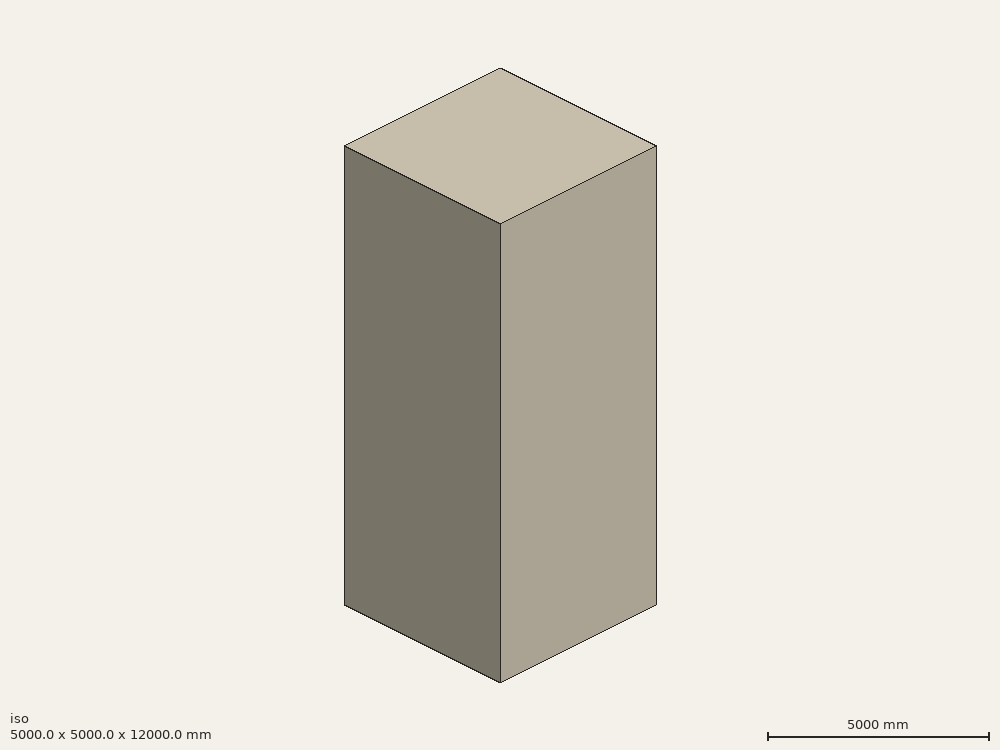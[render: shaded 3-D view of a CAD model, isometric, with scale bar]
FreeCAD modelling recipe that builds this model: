
FCSTD DOCUMENT  (FreeCAD 0.21R33694 (Git))
Label: revolveTester-7_scaled
License: All rights reserved
LicenseURL: http://en.wikipedia.org/wiki/All_rights_reserved
objects: App::DocumentObjectGroupPython×1248, Part::FeaturePython×2, App::Part×2, Sketcher::SketchObject×1, Part::Revolution×1, Part::Cylinder×1, Part::Cut×1
note: 6 computed .brp shape members not serialized (recipe doc carries the construction recipe); baked Part::Feature solids carry a one-line shape summary decoded from their .brp

FEATURE [App::DocumentObjectGroupPython] HALFPI  # scripted group (container) (typed FeaturePython)
  name = HALFPI
  value = pi/2.
FEATURE [App::DocumentObjectGroupPython] PI  # scripted group (container) (typed FeaturePython)
  name = PI
  value = 1.*pi
FEATURE [App::DocumentObjectGroupPython] TWOPI  # scripted group (container) (typed FeaturePython)
  name = TWOPI
  value = 2.*pi
FEATURE [App::DocumentObjectGroupPython] Constants  # scripted group (container) (typed FeaturePython)
  Group = -> [HALFPI,PI,TWOPI]
FEATURE [App::DocumentObjectGroupPython] Variables  # scripted group (container) (typed FeaturePython)
FEATURE [App::DocumentObjectGroupPython] Quantities  # scripted group (container) (typed FeaturePython)
FEATURE [App::DocumentObjectGroupPython] Isotopes  # scripted group (container) (typed FeaturePython)
FEATURE [App::DocumentObjectGroupPython] Elements  # scripted group (container) (typed FeaturePython)
FEATURE [App::DocumentObjectGroupPython] G4Isotopes  # scripted group (container) (typed FeaturePython)
FEATURE [App::DocumentObjectGroupPython] H_element  # scripted group (container) (typed FeaturePython)
  Z = 1
  atom_value = 1.008
  formula = H
  name = H_element
FEATURE [App::DocumentObjectGroupPython] He_element  # scripted group (container) (typed FeaturePython)
  Z = 2
  atom_value = 4.0026
  formula = He
  name = He_element
FEATURE [App::DocumentObjectGroupPython] Li_element  # scripted group (container) (typed FeaturePython)
  Z = 3
  atom_value = 6.94
  formula = Li
  name = Li_element
FEATURE [App::DocumentObjectGroupPython] Be_element  # scripted group (container) (typed FeaturePython)
  Z = 4
  atom_value = 9.01218
  formula = Be
  name = Be_element
FEATURE [App::DocumentObjectGroupPython] B_element  # scripted group (container) (typed FeaturePython)
  Z = 5
  atom_value = 10.81
  formula = B
  name = B_element
FEATURE [App::DocumentObjectGroupPython] C_element  # scripted group (container) (typed FeaturePython)
  Z = 6
  atom_value = 12.011
  formula = C
  name = C_element
FEATURE [App::DocumentObjectGroupPython] N_element  # scripted group (container) (typed FeaturePython)
  Z = 7
  atom_value = 14.007
  formula = N
  name = N_element
FEATURE [App::DocumentObjectGroupPython] O_element  # scripted group (container) (typed FeaturePython)
  Z = 8
  atom_value = 15.999
  formula = O
  name = O_element
FEATURE [App::DocumentObjectGroupPython] F_element  # scripted group (container) (typed FeaturePython)
  Z = 9
  atom_value = 18.9984
  formula = F
  name = F_element
FEATURE [App::DocumentObjectGroupPython] Ne_element  # scripted group (container) (typed FeaturePython)
  Z = 10
  atom_value = 20.1797
  formula = Ne
  name = Ne_element
FEATURE [App::DocumentObjectGroupPython] Na_element  # scripted group (container) (typed FeaturePython)
  Z = 11
  atom_value = 22.9898
  formula = Na
  name = Na_element
FEATURE [App::DocumentObjectGroupPython] Mg_element  # scripted group (container) (typed FeaturePython)
  Z = 12
  atom_value = 24.305
  formula = Mg
  name = Mg_element
FEATURE [App::DocumentObjectGroupPython] Al_element  # scripted group (container) (typed FeaturePython)
  Z = 13
  atom_value = 26.9815
  formula = Al
  name = Al_element
FEATURE [App::DocumentObjectGroupPython] Si_element  # scripted group (container) (typed FeaturePython)
  Z = 14
  atom_value = 28.085
  formula = Si
  name = Si_element
FEATURE [App::DocumentObjectGroupPython] P_element  # scripted group (container) (typed FeaturePython)
  Z = 15
  atom_value = 30.9738
  formula = P
  name = P_element
FEATURE [App::DocumentObjectGroupPython] S_element  # scripted group (container) (typed FeaturePython)
  Z = 16
  atom_value = 32.06
  formula = S
  name = S_element
FEATURE [App::DocumentObjectGroupPython] Cl_element  # scripted group (container) (typed FeaturePython)
  Z = 17
  atom_value = 35.45
  formula = Cl
  name = Cl_element
FEATURE [App::DocumentObjectGroupPython] Ar_element  # scripted group (container) (typed FeaturePython)
  Z = 18
  atom_value = 39.95
  formula = Ar
  name = Ar_element
FEATURE [App::DocumentObjectGroupPython] K_element  # scripted group (container) (typed FeaturePython)
  Z = 19
  atom_value = 39.0983
  formula = K
  name = K_element
FEATURE [App::DocumentObjectGroupPython] Ca_element  # scripted group (container) (typed FeaturePython)
  Z = 20
  atom_value = 40.078
  formula = Ca
  name = Ca_element
FEATURE [App::DocumentObjectGroupPython] Sc_element  # scripted group (container) (typed FeaturePython)
  Z = 21
  atom_value = 44.9559
  formula = Sc
  name = Sc_element
FEATURE [App::DocumentObjectGroupPython] Ti_element  # scripted group (container) (typed FeaturePython)
  Z = 22
  atom_value = 47.867
  formula = Ti
  name = Ti_element
FEATURE [App::DocumentObjectGroupPython] V_element  # scripted group (container) (typed FeaturePython)
  Z = 23
  atom_value = 50.9415
  formula = V
  name = V_element
FEATURE [App::DocumentObjectGroupPython] Cr_element  # scripted group (container) (typed FeaturePython)
  Z = 24
  atom_value = 51.9961
  formula = Cr
  name = Cr_element
FEATURE [App::DocumentObjectGroupPython] Mn_element  # scripted group (container) (typed FeaturePython)
  Z = 25
  atom_value = 54.938
  formula = Mn
  name = Mn_element
FEATURE [App::DocumentObjectGroupPython] Fe_element  # scripted group (container) (typed FeaturePython)
  Z = 26
  atom_value = 55.845
  formula = Fe
  name = Fe_element
FEATURE [App::DocumentObjectGroupPython] Co_element  # scripted group (container) (typed FeaturePython)
  Z = 27
  atom_value = 58.9332
  formula = Co
  name = Co_element
FEATURE [App::DocumentObjectGroupPython] Ni_element  # scripted group (container) (typed FeaturePython)
  Z = 28
  atom_value = 58.6934
  formula = Ni
  name = Ni_element
FEATURE [App::DocumentObjectGroupPython] Cu_element  # scripted group (container) (typed FeaturePython)
  Z = 29
  atom_value = 63.546
  formula = Cu
  name = Cu_element
FEATURE [App::DocumentObjectGroupPython] Zn_element  # scripted group (container) (typed FeaturePython)
  Z = 30
  atom_value = 65.38
  formula = Zn
  name = Zn_element
FEATURE [App::DocumentObjectGroupPython] Ga_element  # scripted group (container) (typed FeaturePython)
  Z = 31
  atom_value = 69.723
  formula = Ga
  name = Ga_element
FEATURE [App::DocumentObjectGroupPython] Ge_element  # scripted group (container) (typed FeaturePython)
  Z = 32
  atom_value = 72.63
  formula = Ge
  name = Ge_element
FEATURE [App::DocumentObjectGroupPython] As_element  # scripted group (container) (typed FeaturePython)
  Z = 33
  atom_value = 74.9216
  formula = As
  name = As_element
FEATURE [App::DocumentObjectGroupPython] Se_element  # scripted group (container) (typed FeaturePython)
  Z = 34
  atom_value = 78.971
  formula = Se
  name = Se_element
FEATURE [App::DocumentObjectGroupPython] Br_element  # scripted group (container) (typed FeaturePython)
  Z = 35
  atom_value = 79.904
  formula = Br
  name = Br_element
FEATURE [App::DocumentObjectGroupPython] Kr_element  # scripted group (container) (typed FeaturePython)
  Z = 36
  atom_value = 83.798
  formula = Kr
  name = Kr_element
FEATURE [App::DocumentObjectGroupPython] Rb_element  # scripted group (container) (typed FeaturePython)
  Z = 37
  atom_value = 85.4678
  formula = Rb
  name = Rb_element
FEATURE [App::DocumentObjectGroupPython] Sr_element  # scripted group (container) (typed FeaturePython)
  Z = 38
  atom_value = 87.62
  formula = Sr
  name = Sr_element
FEATURE [App::DocumentObjectGroupPython] Y_element  # scripted group (container) (typed FeaturePython)
  Z = 39
  atom_value = 88.9058
  formula = Y
  name = Y_element
FEATURE [App::DocumentObjectGroupPython] Zr_element  # scripted group (container) (typed FeaturePython)
  Z = 40
  atom_value = 91.224
  formula = Zr
  name = Zr_element
FEATURE [App::DocumentObjectGroupPython] Nb_element  # scripted group (container) (typed FeaturePython)
  Z = 41
  atom_value = 92.9064
  formula = Nb
  name = Nb_element
FEATURE [App::DocumentObjectGroupPython] Mo_element  # scripted group (container) (typed FeaturePython)
  Z = 42
  atom_value = 95.95
  formula = Mo
  name = Mo_element
FEATURE [App::DocumentObjectGroupPython] Tc_element  # scripted group (container) (typed FeaturePython)
  Z = 43
  atom_value = 97
  formula = Tc
  name = Tc_element
FEATURE [App::DocumentObjectGroupPython] Ru_element  # scripted group (container) (typed FeaturePython)
  Z = 44
  atom_value = 101.07
  formula = Ru
  name = Ru_element
FEATURE [App::DocumentObjectGroupPython] Rh_element  # scripted group (container) (typed FeaturePython)
  Z = 45
  atom_value = 102.905
  formula = Rh
  name = Rh_element
FEATURE [App::DocumentObjectGroupPython] Pd_element  # scripted group (container) (typed FeaturePython)
  Z = 46
  atom_value = 106.42
  formula = Pd
  name = Pd_element
FEATURE [App::DocumentObjectGroupPython] Ag_element  # scripted group (container) (typed FeaturePython)
  Z = 47
  atom_value = 107.868
  formula = Ag
  name = Ag_element
FEATURE [App::DocumentObjectGroupPython] Cd_element  # scripted group (container) (typed FeaturePython)
  Z = 48
  atom_value = 112.414
  formula = Cd
  name = Cd_element
FEATURE [App::DocumentObjectGroupPython] In_element  # scripted group (container) (typed FeaturePython)
  Z = 49
  atom_value = 114.818
  formula = In
  name = In_element
FEATURE [App::DocumentObjectGroupPython] Sn_element  # scripted group (container) (typed FeaturePython)
  Z = 50
  atom_value = 118.71
  formula = Sn
  name = Sn_element
FEATURE [App::DocumentObjectGroupPython] Sb_element  # scripted group (container) (typed FeaturePython)
  Z = 51
  atom_value = 121.76
  formula = Sb
  name = Sb_element
FEATURE [App::DocumentObjectGroupPython] Te_element  # scripted group (container) (typed FeaturePython)
  Z = 52
  atom_value = 127.6
  formula = Te
  name = Te_element
FEATURE [App::DocumentObjectGroupPython] I_element  # scripted group (container) (typed FeaturePython)
  Z = 53
  atom_value = 126.904
  formula = I
  name = I_element
FEATURE [App::DocumentObjectGroupPython] Xe_element  # scripted group (container) (typed FeaturePython)
  Z = 54
  atom_value = 131.293
  formula = Xe
  name = Xe_element
FEATURE [App::DocumentObjectGroupPython] Cs_element  # scripted group (container) (typed FeaturePython)
  Z = 55
  atom_value = 132.905
  formula = Cs
  name = Cs_element
FEATURE [App::DocumentObjectGroupPython] Ba_element  # scripted group (container) (typed FeaturePython)
  Z = 56
  atom_value = 137.327
  formula = Ba
  name = Ba_element
FEATURE [App::DocumentObjectGroupPython] La_element  # scripted group (container) (typed FeaturePython)
  Z = 57
  atom_value = 138.905
  formula = La
  name = La_element
FEATURE [App::DocumentObjectGroupPython] Ce_element  # scripted group (container) (typed FeaturePython)
  Z = 58
  atom_value = 140.116
  formula = Ce
  name = Ce_element
FEATURE [App::DocumentObjectGroupPython] Pr_element  # scripted group (container) (typed FeaturePython)
  Z = 59
  atom_value = 140.908
  formula = Pr
  name = Pr_element
FEATURE [App::DocumentObjectGroupPython] Nd_element  # scripted group (container) (typed FeaturePython)
  Z = 60
  atom_value = 144.242
  formula = Nd
  name = Nd_element
FEATURE [App::DocumentObjectGroupPython] Pm_element  # scripted group (container) (typed FeaturePython)
  Z = 61
  atom_value = 145
  formula = Pm
  name = Pm_element
FEATURE [App::DocumentObjectGroupPython] Sm_element  # scripted group (container) (typed FeaturePython)
  Z = 62
  atom_value = 150.36
  formula = Sm
  name = Sm_element
FEATURE [App::DocumentObjectGroupPython] Eu_element  # scripted group (container) (typed FeaturePython)
  Z = 63
  atom_value = 151.964
  formula = Eu
  name = Eu_element
FEATURE [App::DocumentObjectGroupPython] Gd_element  # scripted group (container) (typed FeaturePython)
  Z = 64
  atom_value = 157.25
  formula = Gd
  name = Gd_element
FEATURE [App::DocumentObjectGroupPython] Tb_element  # scripted group (container) (typed FeaturePython)
  Z = 65
  atom_value = 158.925
  formula = Tb
  name = Tb_element
FEATURE [App::DocumentObjectGroupPython] Dy_element  # scripted group (container) (typed FeaturePython)
  Z = 66
  atom_value = 162.5
  formula = Dy
  name = Dy_element
FEATURE [App::DocumentObjectGroupPython] Ho_element  # scripted group (container) (typed FeaturePython)
  Z = 67
  atom_value = 164.93
  formula = Ho
  name = Ho_element
FEATURE [App::DocumentObjectGroupPython] Er_element  # scripted group (container) (typed FeaturePython)
  Z = 68
  atom_value = 167.259
  formula = Er
  name = Er_element
FEATURE [App::DocumentObjectGroupPython] Tm_element  # scripted group (container) (typed FeaturePython)
  Z = 69
  atom_value = 168.934
  formula = Tm
  name = Tm_element
FEATURE [App::DocumentObjectGroupPython] Yb_element  # scripted group (container) (typed FeaturePython)
  Z = 70
  atom_value = 173.045
  formula = Yb
  name = Yb_element
FEATURE [App::DocumentObjectGroupPython] Lu_element  # scripted group (container) (typed FeaturePython)
  Z = 71
  atom_value = 174.967
  formula = Lu
  name = Lu_element
FEATURE [App::DocumentObjectGroupPython] Hf_element  # scripted group (container) (typed FeaturePython)
  Z = 72
  atom_value = 178.49
  formula = Hf
  name = Hf_element
FEATURE [App::DocumentObjectGroupPython] Ta_element  # scripted group (container) (typed FeaturePython)
  Z = 73
  atom_value = 180.948
  formula = Ta
  name = Ta_element
FEATURE [App::DocumentObjectGroupPython] W_element  # scripted group (container) (typed FeaturePython)
  Z = 74
  atom_value = 183.84
  formula = W
  name = W_element
FEATURE [App::DocumentObjectGroupPython] Re_element  # scripted group (container) (typed FeaturePython)
  Z = 75
  atom_value = 186.207
  formula = Re
  name = Re_element
FEATURE [App::DocumentObjectGroupPython] Os_element  # scripted group (container) (typed FeaturePython)
  Z = 76
  atom_value = 190.23
  formula = Os
  name = Os_element
FEATURE [App::DocumentObjectGroupPython] Ir_element  # scripted group (container) (typed FeaturePython)
  Z = 77
  atom_value = 192.217
  formula = Ir
  name = Ir_element
FEATURE [App::DocumentObjectGroupPython] Pt_element  # scripted group (container) (typed FeaturePython)
  Z = 78
  atom_value = 195.084
  formula = Pt
  name = Pt_element
FEATURE [App::DocumentObjectGroupPython] Au_element  # scripted group (container) (typed FeaturePython)
  Z = 79
  atom_value = 196.967
  formula = Au
  name = Au_element
FEATURE [App::DocumentObjectGroupPython] Hg_element  # scripted group (container) (typed FeaturePython)
  Z = 80
  atom_value = 200.592
  formula = Hg
  name = Hg_element
FEATURE [App::DocumentObjectGroupPython] Tl_element  # scripted group (container) (typed FeaturePython)
  Z = 81
  atom_value = 204.38
  formula = Tl
  name = Tl_element
FEATURE [App::DocumentObjectGroupPython] Pb_element  # scripted group (container) (typed FeaturePython)
  Z = 82
  atom_value = 207.2
  formula = Pb
  name = Pb_element
FEATURE [App::DocumentObjectGroupPython] Bi_element  # scripted group (container) (typed FeaturePython)
  Z = 83
  atom_value = 208.98
  formula = Bi
  name = Bi_element
FEATURE [App::DocumentObjectGroupPython] Po_element  # scripted group (container) (typed FeaturePython)
  Z = 84
  atom_value = 209
  formula = Po
  name = Po_element
FEATURE [App::DocumentObjectGroupPython] At_element  # scripted group (container) (typed FeaturePython)
  Z = 85
  atom_value = 210
  formula = At
  name = At_element
FEATURE [App::DocumentObjectGroupPython] Rn_element  # scripted group (container) (typed FeaturePython)
  Z = 86
  atom_value = 222
  formula = Rn
  name = Rn_element
FEATURE [App::DocumentObjectGroupPython] Fr_element  # scripted group (container) (typed FeaturePython)
  Z = 87
  atom_value = 223
  formula = Fr
  name = Fr_element
FEATURE [App::DocumentObjectGroupPython] Ra_element  # scripted group (container) (typed FeaturePython)
  Z = 88
  atom_value = 226
  formula = Ra
  name = Ra_element
FEATURE [App::DocumentObjectGroupPython] Ac_element  # scripted group (container) (typed FeaturePython)
  Z = 89
  atom_value = 227
  formula = Ac
  name = Ac_element
FEATURE [App::DocumentObjectGroupPython] Th_element  # scripted group (container) (typed FeaturePython)
  Z = 90
  atom_value = 232.038
  formula = Th
  name = Th_element
FEATURE [App::DocumentObjectGroupPython] Pa_element  # scripted group (container) (typed FeaturePython)
  Z = 91
  atom_value = 231.036
  formula = Pa
  name = Pa_element
FEATURE [App::DocumentObjectGroupPython] U_element  # scripted group (container) (typed FeaturePython)
  Z = 92
  atom_value = 238.029
  formula = U
  name = U_element
FEATURE [App::DocumentObjectGroupPython] Np_element  # scripted group (container) (typed FeaturePython)
  Z = 93
  atom_value = 237
  formula = Np
  name = Np_element
FEATURE [App::DocumentObjectGroupPython] Pu_element  # scripted group (container) (typed FeaturePython)
  Z = 94
  atom_value = 244
  formula = Pu
  name = Pu_element
FEATURE [App::DocumentObjectGroupPython] Am_element  # scripted group (container) (typed FeaturePython)
  Z = 95
  atom_value = 243
  formula = Am
  name = Am_element
FEATURE [App::DocumentObjectGroupPython] Cm_element  # scripted group (container) (typed FeaturePython)
  Z = 96
  atom_value = 247
  formula = Cm
  name = Cm_element
FEATURE [App::DocumentObjectGroupPython] Bk_element  # scripted group (container) (typed FeaturePython)
  Z = 97
  atom_value = 247
  formula = Bk
  name = Bk_element
FEATURE [App::DocumentObjectGroupPython] Cf_element  # scripted group (container) (typed FeaturePython)
  Z = 98
  atom_value = 251
  formula = Cf
  name = Cf_element
FEATURE [App::DocumentObjectGroupPython] G4Elements  # scripted group (container) (typed FeaturePython)
  Group = -> [H_element,He_element,Li_element,Be_element,B_element,C_element,N_element,O_element,F_element,Ne_element,Na_element,Mg_element,Al_element,Si_element,P_element,S_element,Cl_element,Ar_element,K_element,Ca_element,Sc_element,Ti_element,V_element,Cr_element,Mn_element,Fe_element,Co_element,Ni_element,Cu_element,Zn_element,Ga_element,Ge_element,As_element,Se_element,Br_element,Kr_element,Rb_element,+61 more]
FEATURE [App::DocumentObjectGroupPython] H_element001  label="H_element : 0.101"  # scripted group (container) (typed FeaturePython)
  n = 0.101327
FEATURE [App::DocumentObjectGroupPython] C_element001  label="C_element : 0.775"  # scripted group (container) (typed FeaturePython)
  n = 0.7755
FEATURE [App::DocumentObjectGroupPython] N_element001  label="N_element : 0.035"  # scripted group (container) (typed FeaturePython)
  n = 0.035057
FEATURE [App::DocumentObjectGroupPython] O_element001  label="O_element : 0.052"  # scripted group (container) (typed FeaturePython)
  n = 0.0523159
FEATURE [App::DocumentObjectGroupPython] F_element001  label="F_element : 0.017"  # scripted group (container) (typed FeaturePython)
  n = 0.017422
FEATURE [App::DocumentObjectGroupPython] Ca_element001  label="Ca_element : 0.018"  # scripted group (container) (typed FeaturePython)
  n = 0.018378
FEATURE [App::DocumentObjectGroupPython] G4_A_150_TISSUE  label="G4_A-150_TISSUE"  # scripted group (container) (typed FeaturePython)
  Dunit = g/cm3
  Dvalue = 1.127
  Group = -> [H_element001,C_element001,N_element001,O_element001,F_element001,Ca_element001]
  conduct = 2
  density = 1
  expand = 3
  formula = G4_A-150_TISSUE
  name = G4_A-150_TISSUE
  specific = 4
FEATURE [App::DocumentObjectGroupPython] C_element002  label="C_element : 3"  # scripted group (container) (typed FeaturePython)
  n = 3
  ref = C_element
FEATURE [App::DocumentObjectGroupPython] H_element002  label="H_element : 6"  # scripted group (container) (typed FeaturePython)
  n = 6
  ref = H_element
FEATURE [App::DocumentObjectGroupPython] O_element002  label="O_element : 1"  # scripted group (container) (typed FeaturePython)
  n = 1
  ref = O_element
FEATURE [App::DocumentObjectGroupPython] G4_ACETONE  # scripted group (container) (typed FeaturePython)
  Dunit = g/cm3
  Dvalue = 0.7899
  Group = -> [C_element002,H_element002,O_element002]
  conduct = 2
  density = 1
  expand = 3
  formula = G4_ACETONE
  name = G4_ACETONE
  specific = 4
FEATURE [App::DocumentObjectGroupPython] C_element003  label="C_element : 2"  # scripted group (container) (typed FeaturePython)
  n = 2
  ref = C_element
FEATURE [App::DocumentObjectGroupPython] H_element003  label="H_element : 2"  # scripted group (container) (typed FeaturePython)
  n = 2
  ref = H_element
FEATURE [App::DocumentObjectGroupPython] G4_ACETYLENE  # scripted group (container) (typed FeaturePython)
  Dunit = g/cm3
  Dvalue = 0.0010967
  Group = -> [C_element003,H_element003]
  conduct = 2
  density = 1
  expand = 3
  formula = G4_ACETYLENE
  name = G4_ACETYLENE
  specific = 4
FEATURE [App::DocumentObjectGroupPython] C_element004  label="C_element : 5"  # scripted group (container) (typed FeaturePython)
  n = 5
  ref = C_element
FEATURE [App::DocumentObjectGroupPython] H_element004  label="H_element : 5"  # scripted group (container) (typed FeaturePython)
  n = 5
  ref = H_element
FEATURE [App::DocumentObjectGroupPython] N_element002  label="N_element : 5"  # scripted group (container) (typed FeaturePython)
  n = 5
  ref = N_element
FEATURE [App::DocumentObjectGroupPython] G4_ADENINE  # scripted group (container) (typed FeaturePython)
  Dunit = g/cm3
  Dvalue = 1.6
  Group = -> [C_element004,H_element004,N_element002]
  conduct = 2
  density = 1
  expand = 3
  formula = G4_ADENINE
  name = G4_ADENINE
  specific = 4
FEATURE [App::DocumentObjectGroupPython] H_element005  label="H_element : 0.114"  # scripted group (container) (typed FeaturePython)
  n = 0.114
FEATURE [App::DocumentObjectGroupPython] C_element005  label="C_element : 0.598"  # scripted group (container) (typed FeaturePython)
  n = 0.598
FEATURE [App::DocumentObjectGroupPython] N_element003  label="N_element : 0.007"  # scripted group (container) (typed FeaturePython)
  n = 0.007
FEATURE [App::DocumentObjectGroupPython] O_element003  label="O_element : 0.278"  # scripted group (container) (typed FeaturePython)
  n = 0.278
FEATURE [App::DocumentObjectGroupPython] Na_element001  label="Na_element : 0.001"  # scripted group (container) (typed FeaturePython)
  n = 0.001
FEATURE [App::DocumentObjectGroupPython] S_element001  label="S_element : 0.001"  # scripted group (container) (typed FeaturePython)
  n = 0.001
FEATURE [App::DocumentObjectGroupPython] Cl_element001  label="Cl_element : 0.001"  # scripted group (container) (typed FeaturePython)
  n = 0.001
FEATURE [App::DocumentObjectGroupPython] G4_ADIPOSE_TISSUE_ICRP  # scripted group (container) (typed FeaturePython)
  Dunit = g/cm3
  Dvalue = 0.95
  Group = -> [H_element005,C_element005,N_element003,O_element003,Na_element001,S_element001,Cl_element001]
  conduct = 2
  density = 1
  expand = 3
  formula = G4_ADIPOSE_TISSUE_ICRP
  name = G4_ADIPOSE_TISSUE_ICRP
  specific = 4
FEATURE [App::DocumentObjectGroupPython] C_element006  label="C_element : 0.000"  # scripted group (container) (typed FeaturePython)
  n = 0.000124
FEATURE [App::DocumentObjectGroupPython] N_element004  label="N_element : 0.755"  # scripted group (container) (typed FeaturePython)
  n = 0.755268
FEATURE [App::DocumentObjectGroupPython] O_element004  label="O_element : 0.232"  # scripted group (container) (typed FeaturePython)
  n = 0.231781
FEATURE [App::DocumentObjectGroupPython] Ar_element001  label="Ar_element : 0.013"  # scripted group (container) (typed FeaturePython)
  n = 0.012827
FEATURE [App::DocumentObjectGroupPython] G4_AIR  # scripted group (container) (typed FeaturePython)
  Dunit = g/cm3
  Dvalue = 0.00120479
  Group = -> [C_element006,N_element004,O_element004,Ar_element001]
  conduct = 2
  density = 1
  expand = 3
  formula = G4_AIR
  name = G4_AIR
  specific = 4
FEATURE [App::DocumentObjectGroupPython] C_element007  label="C_element : 006"  # scripted group (container) (typed FeaturePython)
  n = 3
  ref = C_element
FEATURE [App::DocumentObjectGroupPython] H_element006  label="H_element : 7"  # scripted group (container) (typed FeaturePython)
  n = 7
  ref = H_element
FEATURE [App::DocumentObjectGroupPython] N_element005  label="N_element : 1"  # scripted group (container) (typed FeaturePython)
  n = 1
  ref = N_element
FEATURE [App::DocumentObjectGroupPython] O_element005  label="O_element : 2"  # scripted group (container) (typed FeaturePython)
  n = 2
  ref = O_element
FEATURE [App::DocumentObjectGroupPython] G4_ALANINE  # scripted group (container) (typed FeaturePython)
  Dunit = g/cm3
  Dvalue = 1.42
  Group = -> [C_element007,H_element006,N_element005,O_element005]
  conduct = 2
  density = 1
  expand = 3
  formula = G4_ALANINE
  name = G4_ALANINE
  specific = 4
FEATURE [App::DocumentObjectGroupPython] Al_element001  label="Al_element : 2"  # scripted group (container) (typed FeaturePython)
  n = 2
  ref = Al_element
FEATURE [App::DocumentObjectGroupPython] O_element006  label="O_element : 3"  # scripted group (container) (typed FeaturePython)
  n = 3
  ref = O_element
FEATURE [App::DocumentObjectGroupPython] G4_ALUMINUM_OXIDE  # scripted group (container) (typed FeaturePython)
  Dunit = g/cm3
  Dvalue = 3.97
  Group = -> [Al_element001,O_element006]
  conduct = 2
  density = 1
  expand = 3
  formula = G4_ALUMINUM_OXIDE
  name = G4_ALUMINUM_OXIDE
  specific = 4
FEATURE [App::DocumentObjectGroupPython] H_element007  label="H_element : 0.106"  # scripted group (container) (typed FeaturePython)
  n = 0.10593
FEATURE [App::DocumentObjectGroupPython] C_element008  label="C_element : 0.789"  # scripted group (container) (typed FeaturePython)
  n = 0.788974
FEATURE [App::DocumentObjectGroupPython] O_element007  label="O_element : 0.105"  # scripted group (container) (typed FeaturePython)
  n = 0.105096
FEATURE [App::DocumentObjectGroupPython] G4_AMBER  # scripted group (container) (typed FeaturePython)
  Dunit = g/cm3
  Dvalue = 1.1
  Group = -> [H_element007,C_element008,O_element007]
  conduct = 2
  density = 1
  expand = 3
  formula = G4_AMBER
  name = G4_AMBER
  specific = 4
FEATURE [App::DocumentObjectGroupPython] N_element006  label="N_element : 006"  # scripted group (container) (typed FeaturePython)
  n = 1
  ref = N_element
FEATURE [App::DocumentObjectGroupPython] H_element008  label="H_element : 3"  # scripted group (container) (typed FeaturePython)
  n = 3
  ref = H_element
FEATURE [App::DocumentObjectGroupPython] G4_AMMONIA  # scripted group (container) (typed FeaturePython)
  Dunit = g/cm3
  Dvalue = 0.000826019
  Group = -> [N_element006,H_element008]
  conduct = 2
  density = 1
  expand = 3
  formula = G4_AMMONIA
  name = G4_AMMONIA
  specific = 4
FEATURE [App::DocumentObjectGroupPython] C_element009  label="C_element : 6"  # scripted group (container) (typed FeaturePython)
  n = 6
  ref = C_element
FEATURE [App::DocumentObjectGroupPython] H_element009  label="H_element : 008"  # scripted group (container) (typed FeaturePython)
  n = 7
  ref = H_element
FEATURE [App::DocumentObjectGroupPython] N_element007  label="N_element : 007"  # scripted group (container) (typed FeaturePython)
  n = 1
  ref = N_element
FEATURE [App::DocumentObjectGroupPython] G4_ANILINE  # scripted group (container) (typed FeaturePython)
  Dunit = g/cm3
  Dvalue = 1.0235
  Group = -> [C_element009,H_element009,N_element007]
  conduct = 2
  density = 1
  expand = 3
  formula = G4_ANILINE
  name = G4_ANILINE
  specific = 4
FEATURE [App::DocumentObjectGroupPython] C_element010  label="C_element : 14"  # scripted group (container) (typed FeaturePython)
  n = 14
  ref = C_element
FEATURE [App::DocumentObjectGroupPython] H_element010  label="H_element : 10"  # scripted group (container) (typed FeaturePython)
  n = 10
  ref = H_element
FEATURE [App::DocumentObjectGroupPython] G4_ANTHRACENE  # scripted group (container) (typed FeaturePython)
  Dunit = g/cm3
  Dvalue = 1.283
  Group = -> [C_element010,H_element010]
  conduct = 2
  density = 1
  expand = 3
  formula = G4_ANTHRACENE
  name = G4_ANTHRACENE
  specific = 4
FEATURE [App::DocumentObjectGroupPython] H_element011  label="H_element : 0.065"  # scripted group (container) (typed FeaturePython)
  n = 0.0654709
FEATURE [App::DocumentObjectGroupPython] C_element011  label="C_element : 0.537"  # scripted group (container) (typed FeaturePython)
  n = 0.536944
FEATURE [App::DocumentObjectGroupPython] N_element008  label="N_element : 0.021"  # scripted group (container) (typed FeaturePython)
  n = 0.0215
FEATURE [App::DocumentObjectGroupPython] O_element008  label="O_element : 0.032"  # scripted group (container) (typed FeaturePython)
  n = 0.032085
FEATURE [App::DocumentObjectGroupPython] F_element002  label="F_element : 0.167"  # scripted group (container) (typed FeaturePython)
  n = 0.167411
FEATURE [App::DocumentObjectGroupPython] Ca_element002  label="Ca_element : 0.177"  # scripted group (container) (typed FeaturePython)
  n = 0.176589
FEATURE [App::DocumentObjectGroupPython] G4_B_100_BONE  label="G4_B-100_BONE"  # scripted group (container) (typed FeaturePython)
  Dunit = g/cm3
  Dvalue = 1.45
  Group = -> [H_element011,C_element011,N_element008,O_element008,F_element002,Ca_element002]
  conduct = 2
  density = 1
  expand = 3
  formula = G4_B-100_BONE
  name = G4_B-100_BONE
  specific = 4
FEATURE [App::DocumentObjectGroupPython] H_element012  label="H_element : 0.057"  # scripted group (container) (typed FeaturePython)
  n = 0.057441
FEATURE [App::DocumentObjectGroupPython] C_element012  label="C_element : 0.790"  # scripted group (container) (typed FeaturePython)
  n = 0.774591
FEATURE [App::DocumentObjectGroupPython] O_element009  label="O_element : 0.168"  # scripted group (container) (typed FeaturePython)
  n = 0.167968
FEATURE [App::DocumentObjectGroupPython] G4_BAKELITE  # scripted group (container) (typed FeaturePython)
  Dunit = g/cm3
  Dvalue = 1.25
  Group = -> [H_element012,C_element012,O_element009]
  conduct = 2
  density = 1
  expand = 3
  formula = G4_BAKELITE
  name = G4_BAKELITE
  specific = 4
FEATURE [App::DocumentObjectGroupPython] Ba_element001  label="Ba_element : 1"  # scripted group (container) (typed FeaturePython)
  n = 1
  ref = Ba_element
FEATURE [App::DocumentObjectGroupPython] F_element003  label="F_element : 2"  # scripted group (container) (typed FeaturePython)
  n = 2
  ref = F_element
FEATURE [App::DocumentObjectGroupPython] G4_BARIUM_FLUORIDE  # scripted group (container) (typed FeaturePython)
  Dunit = g/cm3
  Dvalue = 4.89
  Group = -> [Ba_element001,F_element003]
  conduct = 2
  density = 1
  expand = 3
  formula = G4_BARIUM_FLUORIDE
  name = G4_BARIUM_FLUORIDE
  specific = 4
FEATURE [App::DocumentObjectGroupPython] Ba_element002  label="Ba_element : 002"  # scripted group (container) (typed FeaturePython)
  n = 1
  ref = Ba_element
FEATURE [App::DocumentObjectGroupPython] S_element002  label="S_element : 1"  # scripted group (container) (typed FeaturePython)
  n = 1
  ref = S_element
FEATURE [App::DocumentObjectGroupPython] O_element010  label="O_element : 4"  # scripted group (container) (typed FeaturePython)
  n = 4
  ref = O_element
FEATURE [App::DocumentObjectGroupPython] G4_BARIUM_SULFATE  # scripted group (container) (typed FeaturePython)
  Dunit = g/cm3
  Dvalue = 4.5
  Group = -> [Ba_element002,S_element002,O_element010]
  conduct = 2
  density = 1
  expand = 3
  formula = G4_BARIUM_SULFATE
  name = G4_BARIUM_SULFATE
  specific = 4
FEATURE [App::DocumentObjectGroupPython] C_element013  label="C_element : 007"  # scripted group (container) (typed FeaturePython)
  n = 6
  ref = C_element
FEATURE [App::DocumentObjectGroupPython] H_element013  label="H_element : 009"  # scripted group (container) (typed FeaturePython)
  n = 6
  ref = H_element
FEATURE [App::DocumentObjectGroupPython] G4_BENZENE  # scripted group (container) (typed FeaturePython)
  Dunit = g/cm3
  Dvalue = 0.87865
  Group = -> [C_element013,H_element013]
  conduct = 2
  density = 1
  expand = 3
  formula = G4_BENZENE
  name = G4_BENZENE
  specific = 4
FEATURE [App::DocumentObjectGroupPython] Be_element001  label="Be_element : 1"  # scripted group (container) (typed FeaturePython)
  n = 1
  ref = Be_element
FEATURE [App::DocumentObjectGroupPython] O_element011  label="O_element : 005"  # scripted group (container) (typed FeaturePython)
  n = 1
  ref = O_element
FEATURE [App::DocumentObjectGroupPython] G4_BERYLLIUM_OXIDE  # scripted group (container) (typed FeaturePython)
  Dunit = g/cm3
  Dvalue = 3.01
  Group = -> [Be_element001,O_element011]
  conduct = 2
  density = 1
  expand = 3
  formula = G4_BERYLLIUM_OXIDE
  name = G4_BERYLLIUM_OXIDE
  specific = 4
FEATURE [App::DocumentObjectGroupPython] Bi_element001  label="Bi_element : 4"  # scripted group (container) (typed FeaturePython)
  n = 4
  ref = Bi_element
FEATURE [App::DocumentObjectGroupPython] Ge_element001  label="Ge_element : 3"  # scripted group (container) (typed FeaturePython)
  n = 3
  ref = Ge_element
FEATURE [App::DocumentObjectGroupPython] O_element012  label="O_element : 12"  # scripted group (container) (typed FeaturePython)
  n = 12
  ref = O_element
FEATURE [App::DocumentObjectGroupPython] G4_BGO  # scripted group (container) (typed FeaturePython)
  Dunit = g/cm3
  Dvalue = 7.13
  Group = -> [Bi_element001,Ge_element001,O_element012]
  conduct = 2
  density = 1
  expand = 3
  formula = G4_BGO
  name = G4_BGO
  specific = 4
FEATURE [App::DocumentObjectGroupPython] H_element014  label="H_element : 0.102"  # scripted group (container) (typed FeaturePython)
  n = 0.102
FEATURE [App::DocumentObjectGroupPython] C_element014  label="C_element : 0.110"  # scripted group (container) (typed FeaturePython)
  n = 0.11
FEATURE [App::DocumentObjectGroupPython] N_element009  label="N_element : 0.033"  # scripted group (container) (typed FeaturePython)
  n = 0.033
FEATURE [App::DocumentObjectGroupPython] O_element013  label="O_element : 0.745"  # scripted group (container) (typed FeaturePython)
  n = 0.745
FEATURE [App::DocumentObjectGroupPython] Na_element002  label="Na_element : 0.002"  # scripted group (container) (typed FeaturePython)
  n = 0.001
FEATURE [App::DocumentObjectGroupPython] P_element001  label="P_element : 0.001"  # scripted group (container) (typed FeaturePython)
  n = 0.001
FEATURE [App::DocumentObjectGroupPython] S_element003  label="S_element : 0.002"  # scripted group (container) (typed FeaturePython)
  n = 0.002
FEATURE [App::DocumentObjectGroupPython] Cl_element002  label="Cl_element : 0.003"  # scripted group (container) (typed FeaturePython)
  n = 0.003
FEATURE [App::DocumentObjectGroupPython] K_element001  label="K_element : 0.002"  # scripted group (container) (typed FeaturePython)
  n = 0.002
FEATURE [App::DocumentObjectGroupPython] Fe_element001  label="Fe_element : 0.001"  # scripted group (container) (typed FeaturePython)
  n = 0.001
FEATURE [App::DocumentObjectGroupPython] G4_BLOOD_ICRP  # scripted group (container) (typed FeaturePython)
  Dunit = g/cm3
  Dvalue = 1.06
  Group = -> [H_element014,C_element014,N_element009,O_element013,Na_element002,P_element001,S_element003,Cl_element002,K_element001,Fe_element001]
  conduct = 2
  density = 1
  expand = 3
  formula = G4_BLOOD_ICRP
  name = G4_BLOOD_ICRP
  specific = 4
FEATURE [App::DocumentObjectGroupPython] H_element015  label="H_element : 0.064"  # scripted group (container) (typed FeaturePython)
  n = 0.064
FEATURE [App::DocumentObjectGroupPython] C_element015  label="C_element : 0.278"  # scripted group (container) (typed FeaturePython)
  n = 0.278
FEATURE [App::DocumentObjectGroupPython] N_element010  label="N_element : 0.027"  # scripted group (container) (typed FeaturePython)
  n = 0.027
FEATURE [App::DocumentObjectGroupPython] O_element014  label="O_element : 0.410"  # scripted group (container) (typed FeaturePython)
  n = 0.41
FEATURE [App::DocumentObjectGroupPython] Mg_element001  label="Mg_element : 0.002"  # scripted group (container) (typed FeaturePython)
  n = 0.002
FEATURE [App::DocumentObjectGroupPython] P_element002  label="P_element : 0.070"  # scripted group (container) (typed FeaturePython)
  n = 0.07
FEATURE [App::DocumentObjectGroupPython] S_element004  label="S_element : 0.003"  # scripted group (container) (typed FeaturePython)
  n = 0.002
FEATURE [App::DocumentObjectGroupPython] Ca_element003  label="Ca_element : 0.147"  # scripted group (container) (typed FeaturePython)
  n = 0.147
FEATURE [App::DocumentObjectGroupPython] G4_BONE_COMPACT_ICRU  # scripted group (container) (typed FeaturePython)
  Dunit = g/cm3
  Dvalue = 1.85
  Group = -> [H_element015,C_element015,N_element010,O_element014,Mg_element001,P_element002,S_element004,Ca_element003]
  conduct = 2
  density = 1
  expand = 3
  formula = G4_BONE_COMPACT_ICRU
  name = G4_BONE_COMPACT_ICRU
  specific = 4
FEATURE [App::DocumentObjectGroupPython] H_element016  label="H_element : 0.034"  # scripted group (container) (typed FeaturePython)
  n = 0.034
FEATURE [App::DocumentObjectGroupPython] C_element016  label="C_element : 0.155"  # scripted group (container) (typed FeaturePython)
  n = 0.155
FEATURE [App::DocumentObjectGroupPython] N_element011  label="N_element : 0.042"  # scripted group (container) (typed FeaturePython)
  n = 0.042
FEATURE [App::DocumentObjectGroupPython] O_element015  label="O_element : 0.435"  # scripted group (container) (typed FeaturePython)
  n = 0.435
FEATURE [App::DocumentObjectGroupPython] Na_element003  label="Na_element : 0.003"  # scripted group (container) (typed FeaturePython)
  n = 0.001
FEATURE [App::DocumentObjectGroupPython] Mg_element002  label="Mg_element : 0.003"  # scripted group (container) (typed FeaturePython)
  n = 0.002
FEATURE [App::DocumentObjectGroupPython] P_element003  label="P_element : 0.103"  # scripted group (container) (typed FeaturePython)
  n = 0.103
FEATURE [App::DocumentObjectGroupPython] S_element005  label="S_element : 0.004"  # scripted group (container) (typed FeaturePython)
  n = 0.003
FEATURE [App::DocumentObjectGroupPython] Ca_element004  label="Ca_element : 0.225"  # scripted group (container) (typed FeaturePython)
  n = 0.225
FEATURE [App::DocumentObjectGroupPython] G4_BONE_CORTICAL_ICRP  # scripted group (container) (typed FeaturePython)
  Dunit = g/cm3
  Dvalue = 1.92
  Group = -> [H_element016,C_element016,N_element011,O_element015,Na_element003,Mg_element002,P_element003,S_element005,Ca_element004]
  conduct = 2
  density = 1
  expand = 3
  formula = G4_BONE_CORTICAL_ICRP
  name = G4_BONE_CORTICAL_ICRP
  specific = 4
FEATURE [App::DocumentObjectGroupPython] B_element001  label="B_element : 4"  # scripted group (container) (typed FeaturePython)
  n = 4
  ref = B_element
FEATURE [App::DocumentObjectGroupPython] C_element017  label="C_element : 1"  # scripted group (container) (typed FeaturePython)
  n = 1
  ref = C_element
FEATURE [App::DocumentObjectGroupPython] G4_BORON_CARBIDE  # scripted group (container) (typed FeaturePython)
  Dunit = g/cm3
  Dvalue = 2.52
  Group = -> [B_element001,C_element017]
  conduct = 2
  density = 1
  expand = 3
  formula = G4_BORON_CARBIDE
  name = G4_BORON_CARBIDE
  specific = 4
FEATURE [App::DocumentObjectGroupPython] B_element002  label="B_element : 2"  # scripted group (container) (typed FeaturePython)
  n = 2
  ref = B_element
FEATURE [App::DocumentObjectGroupPython] O_element016  label="O_element : 006"  # scripted group (container) (typed FeaturePython)
  n = 3
  ref = O_element
FEATURE [App::DocumentObjectGroupPython] G4_BORON_OXIDE  # scripted group (container) (typed FeaturePython)
  Dunit = g/cm3
  Dvalue = 1.812
  Group = -> [B_element002,O_element016]
  conduct = 2
  density = 1
  expand = 3
  formula = G4_BORON_OXIDE
  name = G4_BORON_OXIDE
  specific = 4
FEATURE [App::DocumentObjectGroupPython] H_element017  label="H_element : 0.107"  # scripted group (container) (typed FeaturePython)
  n = 0.107
FEATURE [App::DocumentObjectGroupPython] C_element018  label="C_element : 0.145"  # scripted group (container) (typed FeaturePython)
  n = 0.145
FEATURE [App::DocumentObjectGroupPython] N_element012  label="N_element : 0.022"  # scripted group (container) (typed FeaturePython)
  n = 0.022
FEATURE [App::DocumentObjectGroupPython] O_element017  label="O_element : 0.712"  # scripted group (container) (typed FeaturePython)
  n = 0.712
FEATURE [App::DocumentObjectGroupPython] Na_element004  label="Na_element : 0.004"  # scripted group (container) (typed FeaturePython)
  n = 0.002
FEATURE [App::DocumentObjectGroupPython] P_element004  label="P_element : 0.004"  # scripted group (container) (typed FeaturePython)
  n = 0.004
FEATURE [App::DocumentObjectGroupPython] S_element006  label="S_element : 0.005"  # scripted group (container) (typed FeaturePython)
  n = 0.002
FEATURE [App::DocumentObjectGroupPython] Cl_element003  label="Cl_element : 0.004"  # scripted group (container) (typed FeaturePython)
  n = 0.003
FEATURE [App::DocumentObjectGroupPython] K_element002  label="K_element : 0.003"  # scripted group (container) (typed FeaturePython)
  n = 0.003
FEATURE [App::DocumentObjectGroupPython] G4_BRAIN_ICRP  # scripted group (container) (typed FeaturePython)
  Dunit = g/cm3
  Dvalue = 1.04
  Group = -> [H_element017,C_element018,N_element012,O_element017,Na_element004,P_element004,S_element006,Cl_element003,K_element002]
  conduct = 2
  density = 1
  expand = 3
  formula = G4_BRAIN_ICRP
  name = G4_BRAIN_ICRP
  specific = 4
FEATURE [App::DocumentObjectGroupPython] C_element019  label="C_element : 4"  # scripted group (container) (typed FeaturePython)
  n = 4
  ref = C_element
FEATURE [App::DocumentObjectGroupPython] H_element018  label="H_element : 010"  # scripted group (container) (typed FeaturePython)
  n = 10
  ref = H_element
FEATURE [App::DocumentObjectGroupPython] G4_BUTANE  # scripted group (container) (typed FeaturePython)
  Dunit = g/cm3
  Dvalue = 0.00249343
  Group = -> [C_element019,H_element018]
  conduct = 2
  density = 1
  expand = 3
  formula = G4_BUTANE
  name = G4_BUTANE
  specific = 4
FEATURE [App::DocumentObjectGroupPython] C_element020  label="C_element : 008"  # scripted group (container) (typed FeaturePython)
  n = 4
  ref = C_element
FEATURE [App::DocumentObjectGroupPython] H_element019  label="H_element : 011"  # scripted group (container) (typed FeaturePython)
  n = 10
  ref = H_element
FEATURE [App::DocumentObjectGroupPython] O_element018  label="O_element : 007"  # scripted group (container) (typed FeaturePython)
  n = 1
  ref = O_element
FEATURE [App::DocumentObjectGroupPython] G4_N_BUTYL_ALCOHOL  label="G4_N-BUTYL_ALCOHOL"  # scripted group (container) (typed FeaturePython)
  Dunit = g/cm3
  Dvalue = 0.8098
  Group = -> [C_element020,H_element019,O_element018]
  conduct = 2
  density = 1
  expand = 3
  formula = G4_N-BUTYL_ALCOHOL
  name = G4_N-BUTYL_ALCOHOL
  specific = 4
FEATURE [App::DocumentObjectGroupPython] H_element020  label="H_element : 0.025"  # scripted group (container) (typed FeaturePython)
  n = 0.02468
FEATURE [App::DocumentObjectGroupPython] C_element021  label="C_element : 0.502"  # scripted group (container) (typed FeaturePython)
  n = 0.501611
FEATURE [App::DocumentObjectGroupPython] O_element019  label="O_element : 0.005"  # scripted group (container) (typed FeaturePython)
  n = 0.004527
FEATURE [App::DocumentObjectGroupPython] F_element004  label="F_element : 0.465"  # scripted group (container) (typed FeaturePython)
  n = 0.465209
FEATURE [App::DocumentObjectGroupPython] Si_element001  label="Si_element : 0.004"  # scripted group (container) (typed FeaturePython)
  n = 0.003973
FEATURE [App::DocumentObjectGroupPython] G4_C_552  label="G4_C-552"  # scripted group (container) (typed FeaturePython)
  Dunit = g/cm3
  Dvalue = 1.76
  Group = -> [H_element020,C_element021,O_element019,F_element004,Si_element001]
  conduct = 2
  density = 1
  expand = 3
  formula = G4_C-552
  name = G4_C-552
  specific = 4
FEATURE [App::DocumentObjectGroupPython] Cd_element001  label="Cd_element : 1"  # scripted group (container) (typed FeaturePython)
  n = 1
  ref = Cd_element
FEATURE [App::DocumentObjectGroupPython] Te_element001  label="Te_element : 1"  # scripted group (container) (typed FeaturePython)
  n = 1
  ref = Te_element
FEATURE [App::DocumentObjectGroupPython] G4_CADMIUM_TELLURIDE  # scripted group (container) (typed FeaturePython)
  Dunit = g/cm3
  Dvalue = 6.2
  Group = -> [Cd_element001,Te_element001]
  conduct = 2
  density = 1
  expand = 3
  formula = G4_CADMIUM_TELLURIDE
  name = G4_CADMIUM_TELLURIDE
  specific = 4
FEATURE [App::DocumentObjectGroupPython] Cd_element002  label="Cd_element : 002"  # scripted group (container) (typed FeaturePython)
  n = 1
  ref = Cd_element
FEATURE [App::DocumentObjectGroupPython] W_element001  label="W_element : 1"  # scripted group (container) (typed FeaturePython)
  n = 1
  ref = W_element
FEATURE [App::DocumentObjectGroupPython] O_element020  label="O_element : 008"  # scripted group (container) (typed FeaturePython)
  n = 4
  ref = O_element
FEATURE [App::DocumentObjectGroupPython] G4_CADMIUM_TUNGSTATE  # scripted group (container) (typed FeaturePython)
  Dunit = g/cm3
  Dvalue = 7.9
  Group = -> [Cd_element002,W_element001,O_element020]
  conduct = 2
  density = 1
  expand = 3
  formula = G4_CADMIUM_TUNGSTATE
  name = G4_CADMIUM_TUNGSTATE
  specific = 4
FEATURE [App::DocumentObjectGroupPython] Ca_element005  label="Ca_element : 1"  # scripted group (container) (typed FeaturePython)
  n = 1
  ref = Ca_element
FEATURE [App::DocumentObjectGroupPython] C_element022  label="C_element : 009"  # scripted group (container) (typed FeaturePython)
  n = 1
  ref = C_element
FEATURE [App::DocumentObjectGroupPython] O_element021  label="O_element : 009"  # scripted group (container) (typed FeaturePython)
  n = 3
  ref = O_element
FEATURE [App::DocumentObjectGroupPython] G4_CALCIUM_CARBONATE  # scripted group (container) (typed FeaturePython)
  Dunit = g/cm3
  Dvalue = 2.8
  Group = -> [Ca_element005,C_element022,O_element021]
  conduct = 2
  density = 1
  expand = 3
  formula = G4_CALCIUM_CARBONATE
  name = G4_CALCIUM_CARBONATE
  specific = 4
FEATURE [App::DocumentObjectGroupPython] Ca_element006  label="Ca_element : 002"  # scripted group (container) (typed FeaturePython)
  n = 1
  ref = Ca_element
FEATURE [App::DocumentObjectGroupPython] F_element005  label="F_element : 003"  # scripted group (container) (typed FeaturePython)
  n = 2
  ref = F_element
FEATURE [App::DocumentObjectGroupPython] G4_CALCIUM_FLUORIDE  # scripted group (container) (typed FeaturePython)
  Dunit = g/cm3
  Dvalue = 3.18
  Group = -> [Ca_element006,F_element005]
  conduct = 2
  density = 1
  expand = 3
  formula = G4_CALCIUM_FLUORIDE
  name = G4_CALCIUM_FLUORIDE
  specific = 4
FEATURE [App::DocumentObjectGroupPython] Ca_element007  label="Ca_element : 003"  # scripted group (container) (typed FeaturePython)
  n = 1
  ref = Ca_element
FEATURE [App::DocumentObjectGroupPython] O_element022  label="O_element : 010"  # scripted group (container) (typed FeaturePython)
  n = 1
  ref = O_element
FEATURE [App::DocumentObjectGroupPython] G4_CALCIUM_OXIDE  # scripted group (container) (typed FeaturePython)
  Dunit = g/cm3
  Dvalue = 3.3
  Group = -> [Ca_element007,O_element022]
  conduct = 2
  density = 1
  expand = 3
  formula = G4_CALCIUM_OXIDE
  name = G4_CALCIUM_OXIDE
  specific = 4
FEATURE [App::DocumentObjectGroupPython] Ca_element008  label="Ca_element : 004"  # scripted group (container) (typed FeaturePython)
  n = 1
  ref = Ca_element
FEATURE [App::DocumentObjectGroupPython] S_element007  label="S_element : 002"  # scripted group (container) (typed FeaturePython)
  n = 1
  ref = S_element
FEATURE [App::DocumentObjectGroupPython] O_element023  label="O_element : 011"  # scripted group (container) (typed FeaturePython)
  n = 4
  ref = O_element
FEATURE [App::DocumentObjectGroupPython] G4_CALCIUM_SULFATE  # scripted group (container) (typed FeaturePython)
  Dunit = g/cm3
  Dvalue = 2.96
  Group = -> [Ca_element008,S_element007,O_element023]
  conduct = 2
  density = 1
  expand = 3
  formula = G4_CALCIUM_SULFATE
  name = G4_CALCIUM_SULFATE
  specific = 4
FEATURE [App::DocumentObjectGroupPython] Ca_element009  label="Ca_element : 005"  # scripted group (container) (typed FeaturePython)
  n = 1
  ref = Ca_element
FEATURE [App::DocumentObjectGroupPython] W_element002  label="W_element : 002"  # scripted group (container) (typed FeaturePython)
  n = 1
  ref = W_element
FEATURE [App::DocumentObjectGroupPython] O_element024  label="O_element : 012"  # scripted group (container) (typed FeaturePython)
  n = 4
  ref = O_element
FEATURE [App::DocumentObjectGroupPython] G4_CALCIUM_TUNGSTATE  # scripted group (container) (typed FeaturePython)
  Dunit = g/cm3
  Dvalue = 6.062
  Group = -> [Ca_element009,W_element002,O_element024]
  conduct = 2
  density = 1
  expand = 3
  formula = G4_CALCIUM_TUNGSTATE
  name = G4_CALCIUM_TUNGSTATE
  specific = 4
FEATURE [App::DocumentObjectGroupPython] C_element023  label="C_element : 010"  # scripted group (container) (typed FeaturePython)
  n = 1
  ref = C_element
FEATURE [App::DocumentObjectGroupPython] O_element025  label="O_element : 013"  # scripted group (container) (typed FeaturePython)
  n = 2
  ref = O_element
FEATURE [App::DocumentObjectGroupPython] G4_CARBON_DIOXIDE  # scripted group (container) (typed FeaturePython)
  Dunit = g/cm3
  Dvalue = 0.00184212
  Group = -> [C_element023,O_element025]
  conduct = 2
  density = 1
  expand = 3
  formula = G4_CARBON_DIOXIDE
  name = G4_CARBON_DIOXIDE
  specific = 4
FEATURE [App::DocumentObjectGroupPython] C_element024  label="C_element : 011"  # scripted group (container) (typed FeaturePython)
  n = 1
  ref = C_element
FEATURE [App::DocumentObjectGroupPython] Cl_element004  label="Cl_element : 4"  # scripted group (container) (typed FeaturePython)
  n = 4
  ref = Cl_element
FEATURE [App::DocumentObjectGroupPython] G4_CARBON_TETRACHLORIDE  # scripted group (container) (typed FeaturePython)
  Dunit = g/cm3
  Dvalue = 1.594
  Group = -> [C_element024,Cl_element004]
  conduct = 2
  density = 1
  expand = 3
  formula = G4_CARBON_TETRACHLORIDE
  name = G4_CARBON_TETRACHLORIDE
  specific = 4
FEATURE [App::DocumentObjectGroupPython] C_element025  label="C_element : 012"  # scripted group (container) (typed FeaturePython)
  n = 6
  ref = C_element
FEATURE [App::DocumentObjectGroupPython] H_element021  label="H_element : 012"  # scripted group (container) (typed FeaturePython)
  n = 10
  ref = H_element
FEATURE [App::DocumentObjectGroupPython] O_element026  label="O_element : 5"  # scripted group (container) (typed FeaturePython)
  n = 5
  ref = O_element
FEATURE [App::DocumentObjectGroupPython] G4_CELLULOSE_CELLOPHANE  # scripted group (container) (typed FeaturePython)
  Dunit = g/cm3
  Dvalue = 1.42
  Group = -> [C_element025,H_element021,O_element026]
  conduct = 2
  density = 1
  expand = 3
  formula = G4_CELLULOSE_CELLOPHANE
  name = G4_CELLULOSE_CELLOPHANE
  specific = 4
FEATURE [App::DocumentObjectGroupPython] H_element022  label="H_element : 0.067"  # scripted group (container) (typed FeaturePython)
  n = 0.067125
FEATURE [App::DocumentObjectGroupPython] C_element026  label="C_element : 0.545"  # scripted group (container) (typed FeaturePython)
  n = 0.545403
FEATURE [App::DocumentObjectGroupPython] O_element027  label="O_element : 0.387"  # scripted group (container) (typed FeaturePython)
  n = 0.387472
FEATURE [App::DocumentObjectGroupPython] G4_CELLULOSE_BUTYRATE  # scripted group (container) (typed FeaturePython)
  Dunit = g/cm3
  Dvalue = 1.2
  Group = -> [H_element022,C_element026,O_element027]
  conduct = 2
  density = 1
  expand = 3
  formula = G4_CELLULOSE_BUTYRATE
  name = G4_CELLULOSE_BUTYRATE
  specific = 4
FEATURE [App::DocumentObjectGroupPython] H_element023  label="H_element : 0.029"  # scripted group (container) (typed FeaturePython)
  n = 0.029216
FEATURE [App::DocumentObjectGroupPython] C_element027  label="C_element : 0.271"  # scripted group (container) (typed FeaturePython)
  n = 0.271296
FEATURE [App::DocumentObjectGroupPython] N_element013  label="N_element : 0.121"  # scripted group (container) (typed FeaturePython)
  n = 0.121276
FEATURE [App::DocumentObjectGroupPython] O_element028  label="O_element : 0.578"  # scripted group (container) (typed FeaturePython)
  n = 0.578212
FEATURE [App::DocumentObjectGroupPython] G4_CELLULOSE_NITRATE  # scripted group (container) (typed FeaturePython)
  Dunit = g/cm3
  Dvalue = 1.49
  Group = -> [H_element023,C_element027,N_element013,O_element028]
  conduct = 2
  density = 1
  expand = 3
  formula = G4_CELLULOSE_NITRATE
  name = G4_CELLULOSE_NITRATE
  specific = 4
FEATURE [App::DocumentObjectGroupPython] H_element024  label="H_element : 0.108"  # scripted group (container) (typed FeaturePython)
  n = 0.107596
FEATURE [App::DocumentObjectGroupPython] N_element014  label="N_element : 0.001"  # scripted group (container) (typed FeaturePython)
  n = 0.0008
FEATURE [App::DocumentObjectGroupPython] O_element029  label="O_element : 0.875"  # scripted group (container) (typed FeaturePython)
  n = 0.874976
FEATURE [App::DocumentObjectGroupPython] S_element008  label="S_element : 0.015"  # scripted group (container) (typed FeaturePython)
  n = 0.014627
FEATURE [App::DocumentObjectGroupPython] Ce_element001  label="Ce_element : 0.002"  # scripted group (container) (typed FeaturePython)
  n = 0.002001
FEATURE [App::DocumentObjectGroupPython] G4_CERIC_SULFATE  # scripted group (container) (typed FeaturePython)
  Dunit = g/cm3
  Dvalue = 1.03
  Group = -> [H_element024,N_element014,O_element029,S_element008,Ce_element001]
  conduct = 2
  density = 1
  expand = 3
  formula = G4_CERIC_SULFATE
  name = G4_CERIC_SULFATE
  specific = 4
FEATURE [App::DocumentObjectGroupPython] Cs_element001  label="Cs_element : 1"  # scripted group (container) (typed FeaturePython)
  n = 1
  ref = Cs_element
FEATURE [App::DocumentObjectGroupPython] F_element006  label="F_element : 1"  # scripted group (container) (typed FeaturePython)
  n = 1
  ref = F_element
FEATURE [App::DocumentObjectGroupPython] G4_CESIUM_FLUORIDE  # scripted group (container) (typed FeaturePython)
  Dunit = g/cm3
  Dvalue = 4.115
  Group = -> [Cs_element001,F_element006]
  conduct = 2
  density = 1
  expand = 3
  formula = G4_CESIUM_FLUORIDE
  name = G4_CESIUM_FLUORIDE
  specific = 4
FEATURE [App::DocumentObjectGroupPython] Cs_element002  label="Cs_element : 002"  # scripted group (container) (typed FeaturePython)
  n = 1
  ref = Cs_element
FEATURE [App::DocumentObjectGroupPython] I_element001  label="I_element : 1"  # scripted group (container) (typed FeaturePython)
  n = 1
  ref = I_element
FEATURE [App::DocumentObjectGroupPython] G4_CESIUM_IODIDE  # scripted group (container) (typed FeaturePython)
  Dunit = g/cm3
  Dvalue = 4.51
  Group = -> [Cs_element002,I_element001]
  conduct = 2
  density = 1
  expand = 3
  formula = G4_CESIUM_IODIDE
  name = G4_CESIUM_IODIDE
  specific = 4
FEATURE [App::DocumentObjectGroupPython] C_element028  label="C_element : 013"  # scripted group (container) (typed FeaturePython)
  n = 6
  ref = C_element
FEATURE [App::DocumentObjectGroupPython] H_element025  label="H_element : 013"  # scripted group (container) (typed FeaturePython)
  n = 5
  ref = H_element
FEATURE [App::DocumentObjectGroupPython] Cl_element005  label="Cl_element : 1"  # scripted group (container) (typed FeaturePython)
  n = 1
  ref = Cl_element
FEATURE [App::DocumentObjectGroupPython] G4_CHLOROBENZENE  # scripted group (container) (typed FeaturePython)
  Dunit = g/cm3
  Dvalue = 1.1058
  Group = -> [C_element028,H_element025,Cl_element005]
  conduct = 2
  density = 1
  expand = 3
  formula = G4_CHLOROBENZENE
  name = G4_CHLOROBENZENE
  specific = 4
FEATURE [App::DocumentObjectGroupPython] C_element029  label="C_element : 014"  # scripted group (container) (typed FeaturePython)
  n = 1
  ref = C_element
FEATURE [App::DocumentObjectGroupPython] H_element026  label="H_element : 1"  # scripted group (container) (typed FeaturePython)
  n = 1
  ref = H_element
FEATURE [App::DocumentObjectGroupPython] Cl_element006  label="Cl_element : 3"  # scripted group (container) (typed FeaturePython)
  n = 3
  ref = Cl_element
FEATURE [App::DocumentObjectGroupPython] G4_CHLOROFORM  # scripted group (container) (typed FeaturePython)
  Dunit = g/cm3
  Dvalue = 1.4832
  Group = -> [C_element029,H_element026,Cl_element006]
  conduct = 2
  density = 1
  expand = 3
  formula = G4_CHLOROFORM
  name = G4_CHLOROFORM
  specific = 4
FEATURE [App::DocumentObjectGroupPython] H_element027  label="H_element : 0.010"  # scripted group (container) (typed FeaturePython)
  n = 0.01
FEATURE [App::DocumentObjectGroupPython] C_element030  label="C_element : 0.001"  # scripted group (container) (typed FeaturePython)
  n = 0.001
FEATURE [App::DocumentObjectGroupPython] O_element030  label="O_element : 0.529"  # scripted group (container) (typed FeaturePython)
  n = 0.529107
FEATURE [App::DocumentObjectGroupPython] Na_element005  label="Na_element : 0.016"  # scripted group (container) (typed FeaturePython)
  n = 0.016
FEATURE [App::DocumentObjectGroupPython] Mg_element003  label="Mg_element : 0.004"  # scripted group (container) (typed FeaturePython)
  n = 0.002
FEATURE [App::DocumentObjectGroupPython] Al_element002  label="Al_element : 0.034"  # scripted group (container) (typed FeaturePython)
  n = 0.033872
FEATURE [App::DocumentObjectGroupPython] Si_element002  label="Si_element : 0.337"  # scripted group (container) (typed FeaturePython)
  n = 0.337021
FEATURE [App::DocumentObjectGroupPython] K_element003  label="K_element : 0.013"  # scripted group (container) (typed FeaturePython)
  n = 0.013
FEATURE [App::DocumentObjectGroupPython] Ca_element010  label="Ca_element : 0.044"  # scripted group (container) (typed FeaturePython)
  n = 0.044
FEATURE [App::DocumentObjectGroupPython] Fe_element002  label="Fe_element : 0.014"  # scripted group (container) (typed FeaturePython)
  n = 0.014
FEATURE [App::DocumentObjectGroupPython] G4_CONCRETE  # scripted group (container) (typed FeaturePython)
  Dunit = g/cm3
  Dvalue = 2.3
  Group = -> [H_element027,C_element030,O_element030,Na_element005,Mg_element003,Al_element002,Si_element002,K_element003,Ca_element010,Fe_element002]
  conduct = 2
  density = 1
  expand = 3
  formula = G4_CONCRETE
  name = G4_CONCRETE
  specific = 4
FEATURE [App::DocumentObjectGroupPython] C_element031  label="C_element : 015"  # scripted group (container) (typed FeaturePython)
  n = 6
  ref = C_element
FEATURE [App::DocumentObjectGroupPython] H_element028  label="H_element : 12"  # scripted group (container) (typed FeaturePython)
  n = 12
  ref = H_element
FEATURE [App::DocumentObjectGroupPython] G4_CYCLOHEXANE  # scripted group (container) (typed FeaturePython)
  Dunit = g/cm3
  Dvalue = 0.779
  Group = -> [C_element031,H_element028]
  conduct = 2
  density = 1
  expand = 3
  formula = G4_CYCLOHEXANE
  name = G4_CYCLOHEXANE
  specific = 4
FEATURE [App::DocumentObjectGroupPython] C_element032  label="C_element : 016"  # scripted group (container) (typed FeaturePython)
  n = 6
  ref = C_element
FEATURE [App::DocumentObjectGroupPython] H_element029  label="H_element : 4"  # scripted group (container) (typed FeaturePython)
  n = 4
  ref = H_element
FEATURE [App::DocumentObjectGroupPython] Cl_element007  label="Cl_element : 2"  # scripted group (container) (typed FeaturePython)
  n = 2
  ref = Cl_element
FEATURE [App::DocumentObjectGroupPython] G4_1_2_DICHLOROBENZENE  label="G4_1.2-DICHLOROBENZENE"  # scripted group (container) (typed FeaturePython)
  Dunit = g/cm3
  Dvalue = 1.3048
  Group = -> [C_element032,H_element029,Cl_element007]
  conduct = 2
  density = 1
  expand = 3
  formula = G4_1.2-DICHLOROBENZENE
  name = G4_1.2-DICHLOROBENZENE
  specific = 4
FEATURE [App::DocumentObjectGroupPython] C_element033  label="C_element : 017"  # scripted group (container) (typed FeaturePython)
  n = 4
  ref = C_element
FEATURE [App::DocumentObjectGroupPython] H_element030  label="H_element : 8"  # scripted group (container) (typed FeaturePython)
  n = 8
  ref = H_element
FEATURE [App::DocumentObjectGroupPython] O_element031  label="O_element : 014"  # scripted group (container) (typed FeaturePython)
  n = 1
  ref = O_element
FEATURE [App::DocumentObjectGroupPython] Cl_element008  label="Cl_element : 005"  # scripted group (container) (typed FeaturePython)
  n = 2
  ref = Cl_element
FEATURE [App::DocumentObjectGroupPython] G4_DICHLORODIETHYL_ETHER  # scripted group (container) (typed FeaturePython)
  Dunit = g/cm3
  Dvalue = 1.2199
  Group = -> [C_element033,H_element030,O_element031,Cl_element008]
  conduct = 2
  density = 1
  expand = 3
  formula = G4_DICHLORODIETHYL_ETHER
  name = G4_DICHLORODIETHYL_ETHER
  specific = 4
FEATURE [App::DocumentObjectGroupPython] C_element034  label="C_element : 018"  # scripted group (container) (typed FeaturePython)
  n = 2
  ref = C_element
FEATURE [App::DocumentObjectGroupPython] H_element031  label="H_element : 014"  # scripted group (container) (typed FeaturePython)
  n = 4
  ref = H_element
FEATURE [App::DocumentObjectGroupPython] Cl_element009  label="Cl_element : 006"  # scripted group (container) (typed FeaturePython)
  n = 2
  ref = Cl_element
FEATURE [App::DocumentObjectGroupPython] G4_1_2_DICHLOROETHANE  label="G4_1.2-DICHLOROETHANE"  # scripted group (container) (typed FeaturePython)
  Dunit = g/cm3
  Dvalue = 1.2351
  Group = -> [C_element034,H_element031,Cl_element009]
  conduct = 2
  density = 1
  expand = 3
  formula = G4_1.2-DICHLOROETHANE
  name = G4_1.2-DICHLOROETHANE
  specific = 4
FEATURE [App::DocumentObjectGroupPython] C_element035  label="C_element : 019"  # scripted group (container) (typed FeaturePython)
  n = 4
  ref = C_element
FEATURE [App::DocumentObjectGroupPython] H_element032  label="H_element : 015"  # scripted group (container) (typed FeaturePython)
  n = 10
  ref = H_element
FEATURE [App::DocumentObjectGroupPython] O_element032  label="O_element : 015"  # scripted group (container) (typed FeaturePython)
  n = 1
  ref = O_element
FEATURE [App::DocumentObjectGroupPython] G4_DIETHYL_ETHER  # scripted group (container) (typed FeaturePython)
  Dunit = g/cm3
  Dvalue = 0.71378
  Group = -> [C_element035,H_element032,O_element032]
  conduct = 2
  density = 1
  expand = 3
  formula = G4_DIETHYL_ETHER
  name = G4_DIETHYL_ETHER
  specific = 4
FEATURE [App::DocumentObjectGroupPython] C_element036  label="C_element : 020"  # scripted group (container) (typed FeaturePython)
  n = 3
  ref = C_element
FEATURE [App::DocumentObjectGroupPython] H_element033  label="H_element : 016"  # scripted group (container) (typed FeaturePython)
  n = 7
  ref = H_element
FEATURE [App::DocumentObjectGroupPython] N_element015  label="N_element : 008"  # scripted group (container) (typed FeaturePython)
  n = 1
  ref = N_element
FEATURE [App::DocumentObjectGroupPython] O_element033  label="O_element : 016"  # scripted group (container) (typed FeaturePython)
  n = 1
  ref = O_element
FEATURE [App::DocumentObjectGroupPython] G4_N_N_DIMETHYL_FORMAMIDE  label="G4_N.N-DIMETHYL_FORMAMIDE"  # scripted group (container) (typed FeaturePython)
  Dunit = g/cm3
  Dvalue = 0.9487
  Group = -> [C_element036,H_element033,N_element015,O_element033]
  conduct = 2
  density = 1
  expand = 3
  formula = G4_N.N-DIMETHYL_FORMAMIDE
  name = G4_N.N-DIMETHYL_FORMAMIDE
  specific = 4
FEATURE [App::DocumentObjectGroupPython] C_element037  label="C_element : 021"  # scripted group (container) (typed FeaturePython)
  n = 2
  ref = C_element
FEATURE [App::DocumentObjectGroupPython] H_element034  label="H_element : 017"  # scripted group (container) (typed FeaturePython)
  n = 6
  ref = H_element
FEATURE [App::DocumentObjectGroupPython] O_element034  label="O_element : 017"  # scripted group (container) (typed FeaturePython)
  n = 1
  ref = O_element
FEATURE [App::DocumentObjectGroupPython] S_element009  label="S_element : 003"  # scripted group (container) (typed FeaturePython)
  n = 1
  ref = S_element
FEATURE [App::DocumentObjectGroupPython] G4_DIMETHYL_SULFOXIDE  # scripted group (container) (typed FeaturePython)
  Dunit = g/cm3
  Dvalue = 1.1014
  Group = -> [C_element037,H_element034,O_element034,S_element009]
  conduct = 2
  density = 1
  expand = 3
  formula = G4_DIMETHYL_SULFOXIDE
  name = G4_DIMETHYL_SULFOXIDE
  specific = 4
FEATURE [App::DocumentObjectGroupPython] C_element038  label="C_element : 022"  # scripted group (container) (typed FeaturePython)
  n = 2
  ref = C_element
FEATURE [App::DocumentObjectGroupPython] H_element035  label="H_element : 018"  # scripted group (container) (typed FeaturePython)
  n = 6
  ref = H_element
FEATURE [App::DocumentObjectGroupPython] G4_ETHANE  # scripted group (container) (typed FeaturePython)
  Dunit = g/cm3
  Dvalue = 0.00125324
  Group = -> [C_element038,H_element035]
  conduct = 2
  density = 1
  expand = 3
  formula = G4_ETHANE
  name = G4_ETHANE
  specific = 4
FEATURE [App::DocumentObjectGroupPython] C_element039  label="C_element : 023"  # scripted group (container) (typed FeaturePython)
  n = 2
  ref = C_element
FEATURE [App::DocumentObjectGroupPython] H_element036  label="H_element : 019"  # scripted group (container) (typed FeaturePython)
  n = 6
  ref = H_element
FEATURE [App::DocumentObjectGroupPython] O_element035  label="O_element : 018"  # scripted group (container) (typed FeaturePython)
  n = 1
  ref = O_element
FEATURE [App::DocumentObjectGroupPython] G4_ETHYL_ALCOHOL  # scripted group (container) (typed FeaturePython)
  Dunit = g/cm3
  Dvalue = 0.7893
  Group = -> [C_element039,H_element036,O_element035]
  conduct = 2
  density = 1
  expand = 3
  formula = G4_ETHYL_ALCOHOL
  name = G4_ETHYL_ALCOHOL
  specific = 4
FEATURE [App::DocumentObjectGroupPython] H_element037  label="H_element : 0.090"  # scripted group (container) (typed FeaturePython)
  n = 0.090027
FEATURE [App::DocumentObjectGroupPython] C_element040  label="C_element : 0.585"  # scripted group (container) (typed FeaturePython)
  n = 0.585182
FEATURE [App::DocumentObjectGroupPython] O_element036  label="O_element : 0.325"  # scripted group (container) (typed FeaturePython)
  n = 0.324791
FEATURE [App::DocumentObjectGroupPython] G4_ETHYL_CELLULOSE  # scripted group (container) (typed FeaturePython)
  Dunit = g/cm3
  Dvalue = 1.13
  Group = -> [H_element037,C_element040,O_element036]
  conduct = 2
  density = 1
  expand = 3
  formula = G4_ETHYL_CELLULOSE
  name = G4_ETHYL_CELLULOSE
  specific = 4
FEATURE [App::DocumentObjectGroupPython] C_element041  label="C_element : 024"  # scripted group (container) (typed FeaturePython)
  n = 2
  ref = C_element
FEATURE [App::DocumentObjectGroupPython] H_element038  label="H_element : 020"  # scripted group (container) (typed FeaturePython)
  n = 4
  ref = H_element
FEATURE [App::DocumentObjectGroupPython] G4_ETHYLENE  # scripted group (container) (typed FeaturePython)
  Dunit = g/cm3
  Dvalue = 0.00117497
  Group = -> [C_element041,H_element038]
  conduct = 2
  density = 1
  expand = 3
  formula = G4_ETHYLENE
  name = G4_ETHYLENE
  specific = 4
FEATURE [App::DocumentObjectGroupPython] H_element039  label="H_element : 0.096"  # scripted group (container) (typed FeaturePython)
  n = 0.096
FEATURE [App::DocumentObjectGroupPython] C_element042  label="C_element : 0.195"  # scripted group (container) (typed FeaturePython)
  n = 0.195
FEATURE [App::DocumentObjectGroupPython] N_element016  label="N_element : 0.057"  # scripted group (container) (typed FeaturePython)
  n = 0.057
FEATURE [App::DocumentObjectGroupPython] O_element037  label="O_element : 0.646"  # scripted group (container) (typed FeaturePython)
  n = 0.646
FEATURE [App::DocumentObjectGroupPython] Na_element006  label="Na_element : 0.017"  # scripted group (container) (typed FeaturePython)
  n = 0.001
FEATURE [App::DocumentObjectGroupPython] P_element005  label="P_element : 0.104"  # scripted group (container) (typed FeaturePython)
  n = 0.001
FEATURE [App::DocumentObjectGroupPython] S_element010  label="S_element : 0.016"  # scripted group (container) (typed FeaturePython)
  n = 0.003
FEATURE [App::DocumentObjectGroupPython] Cl_element010  label="Cl_element : 0.005"  # scripted group (container) (typed FeaturePython)
  n = 0.001
FEATURE [App::DocumentObjectGroupPython] G4_EYE_LENS_ICRP  # scripted group (container) (typed FeaturePython)
  Dunit = g/cm3
  Dvalue = 1.07
  Group = -> [H_element039,C_element042,N_element016,O_element037,Na_element006,P_element005,S_element010,Cl_element010]
  conduct = 2
  density = 1
  expand = 3
  formula = G4_EYE_LENS_ICRP
  name = G4_EYE_LENS_ICRP
  specific = 4
FEATURE [App::DocumentObjectGroupPython] Fe_element003  label="Fe_element : 2"  # scripted group (container) (typed FeaturePython)
  n = 2
  ref = Fe_element
FEATURE [App::DocumentObjectGroupPython] O_element038  label="O_element : 019"  # scripted group (container) (typed FeaturePython)
  n = 3
  ref = O_element
FEATURE [App::DocumentObjectGroupPython] G4_FERRIC_OXIDE  # scripted group (container) (typed FeaturePython)
  Dunit = g/cm3
  Dvalue = 5.2
  Group = -> [Fe_element003,O_element038]
  conduct = 2
  density = 1
  expand = 3
  formula = G4_FERRIC_OXIDE
  name = G4_FERRIC_OXIDE
  specific = 4
FEATURE [App::DocumentObjectGroupPython] Fe_element004  label="Fe_element : 1"  # scripted group (container) (typed FeaturePython)
  n = 1
  ref = Fe_element
FEATURE [App::DocumentObjectGroupPython] B_element003  label="B_element : 1"  # scripted group (container) (typed FeaturePython)
  n = 1
  ref = B_element
FEATURE [App::DocumentObjectGroupPython] G4_FERROBORIDE  # scripted group (container) (typed FeaturePython)
  Dunit = g/cm3
  Dvalue = 7.15
  Group = -> [Fe_element004,B_element003]
  conduct = 2
  density = 1
  expand = 3
  formula = G4_FERROBORIDE
  name = G4_FERROBORIDE
  specific = 4
FEATURE [App::DocumentObjectGroupPython] Fe_element005  label="Fe_element : 003"  # scripted group (container) (typed FeaturePython)
  n = 1
  ref = Fe_element
FEATURE [App::DocumentObjectGroupPython] O_element039  label="O_element : 020"  # scripted group (container) (typed FeaturePython)
  n = 1
  ref = O_element
FEATURE [App::DocumentObjectGroupPython] G4_FERROUS_OXIDE  # scripted group (container) (typed FeaturePython)
  Dunit = g/cm3
  Dvalue = 5.7
  Group = -> [Fe_element005,O_element039]
  conduct = 2
  density = 1
  expand = 3
  formula = G4_FERROUS_OXIDE
  name = G4_FERROUS_OXIDE
  specific = 4
FEATURE [App::DocumentObjectGroupPython] H_element040  label="H_element : 0.115"  # scripted group (container) (typed FeaturePython)
  n = 0.108259
FEATURE [App::DocumentObjectGroupPython] N_element017  label="N_element : 0.000"  # scripted group (container) (typed FeaturePython)
  n = 2.7e-05
FEATURE [App::DocumentObjectGroupPython] O_element040  label="O_element : 0.879"  # scripted group (container) (typed FeaturePython)
  n = 0.878636
FEATURE [App::DocumentObjectGroupPython] Na_element007  label="Na_element : 0.000"  # scripted group (container) (typed FeaturePython)
  n = 2.2e-05
FEATURE [App::DocumentObjectGroupPython] S_element011  label="S_element : 0.013"  # scripted group (container) (typed FeaturePython)
  n = 0.012968
FEATURE [App::DocumentObjectGroupPython] Cl_element011  label="Cl_element : 0.000"  # scripted group (container) (typed FeaturePython)
  n = 3.4e-05
FEATURE [App::DocumentObjectGroupPython] Fe_element006  label="Fe_element : 0.000"  # scripted group (container) (typed FeaturePython)
  n = 5.4e-05
FEATURE [App::DocumentObjectGroupPython] G4_FERROUS_SULFATE  # scripted group (container) (typed FeaturePython)
  Dunit = g/cm3
  Dvalue = 1.024
  Group = -> [H_element040,N_element017,O_element040,Na_element007,S_element011,Cl_element011,Fe_element006]
  conduct = 2
  density = 1
  expand = 3
  formula = G4_FERROUS_SULFATE
  name = G4_FERROUS_SULFATE
  specific = 4
FEATURE [App::DocumentObjectGroupPython] C_element043  label="C_element : 0.099"  # scripted group (container) (typed FeaturePython)
  n = 0.099335
FEATURE [App::DocumentObjectGroupPython] F_element007  label="F_element : 0.314"  # scripted group (container) (typed FeaturePython)
  n = 0.314247
FEATURE [App::DocumentObjectGroupPython] Cl_element012  label="Cl_element : 0.586"  # scripted group (container) (typed FeaturePython)
  n = 0.586418
FEATURE [App::DocumentObjectGroupPython] G4_FREON_12  label="G4_FREON-12"  # scripted group (container) (typed FeaturePython)
  Dunit = g/cm3
  Dvalue = 1.12
  Group = -> [C_element043,F_element007,Cl_element012]
  conduct = 2
  density = 1
  expand = 3
  formula = G4_FREON-12
  name = G4_FREON-12
  specific = 4
FEATURE [App::DocumentObjectGroupPython] C_element044  label="C_element : 0.057"  # scripted group (container) (typed FeaturePython)
  n = 0.057245
FEATURE [App::DocumentObjectGroupPython] F_element008  label="F_element : 0.181"  # scripted group (container) (typed FeaturePython)
  n = 0.181096
FEATURE [App::DocumentObjectGroupPython] Br_element001  label="Br_element : 0.762"  # scripted group (container) (typed FeaturePython)
  n = 0.761659
FEATURE [App::DocumentObjectGroupPython] G4_FREON_12B2  label="G4_FREON-12B2"  # scripted group (container) (typed FeaturePython)
  Dunit = g/cm3
  Dvalue = 1.8
  Group = -> [C_element044,F_element008,Br_element001]
  conduct = 2
  density = 1
  expand = 3
  formula = G4_FREON-12B2
  name = G4_FREON-12B2
  specific = 4
FEATURE [App::DocumentObjectGroupPython] C_element045  label="C_element : 0.115"  # scripted group (container) (typed FeaturePython)
  n = 0.114983
FEATURE [App::DocumentObjectGroupPython] F_element009  label="F_element : 0.546"  # scripted group (container) (typed FeaturePython)
  n = 0.545621
FEATURE [App::DocumentObjectGroupPython] Cl_element013  label="Cl_element : 0.339"  # scripted group (container) (typed FeaturePython)
  n = 0.339396
FEATURE [App::DocumentObjectGroupPython] G4_FREON_13  label="G4_FREON-13"  # scripted group (container) (typed FeaturePython)
  Dunit = g/cm3
  Dvalue = 0.95
  Group = -> [C_element045,F_element009,Cl_element013]
  conduct = 2
  density = 1
  expand = 3
  formula = G4_FREON-13
  name = G4_FREON-13
  specific = 4
FEATURE [App::DocumentObjectGroupPython] C_element046  label="C_element : 025"  # scripted group (container) (typed FeaturePython)
  n = 1
  ref = C_element
FEATURE [App::DocumentObjectGroupPython] F_element010  label="F_element : 3"  # scripted group (container) (typed FeaturePython)
  n = 3
  ref = F_element
FEATURE [App::DocumentObjectGroupPython] Br_element002  label="Br_element : 1"  # scripted group (container) (typed FeaturePython)
  n = 1
  ref = Br_element
FEATURE [App::DocumentObjectGroupPython] G4_FREON_13B1  label="G4_FREON-13B1"  # scripted group (container) (typed FeaturePython)
  Dunit = g/cm3
  Dvalue = 1.5
  Group = -> [C_element046,F_element010,Br_element002]
  conduct = 2
  density = 1
  expand = 3
  formula = G4_FREON-13B1
  name = G4_FREON-13B1
  specific = 4
FEATURE [App::DocumentObjectGroupPython] C_element047  label="C_element : 0.061"  # scripted group (container) (typed FeaturePython)
  n = 0.061309
FEATURE [App::DocumentObjectGroupPython] F_element011  label="F_element : 0.291"  # scripted group (container) (typed FeaturePython)
  n = 0.290924
FEATURE [App::DocumentObjectGroupPython] I_element002  label="I_element : 0.648"  # scripted group (container) (typed FeaturePython)
  n = 0.647767
FEATURE [App::DocumentObjectGroupPython] G4_FREON_13I1  label="G4_FREON-13I1"  # scripted group (container) (typed FeaturePython)
  Dunit = g/cm3
  Dvalue = 1.8
  Group = -> [C_element047,F_element011,I_element002]
  conduct = 2
  density = 1
  expand = 3
  formula = G4_FREON-13I1
  name = G4_FREON-13I1
  specific = 4
FEATURE [App::DocumentObjectGroupPython] Gd_element001  label="Gd_element : 2"  # scripted group (container) (typed FeaturePython)
  n = 2
  ref = Gd_element
FEATURE [App::DocumentObjectGroupPython] O_element041  label="O_element : 021"  # scripted group (container) (typed FeaturePython)
  n = 2
  ref = O_element
FEATURE [App::DocumentObjectGroupPython] S_element012  label="S_element : 004"  # scripted group (container) (typed FeaturePython)
  n = 1
  ref = S_element
FEATURE [App::DocumentObjectGroupPython] G4_GADOLINIUM_OXYSULFIDE  # scripted group (container) (typed FeaturePython)
  Dunit = g/cm3
  Dvalue = 7.44
  Group = -> [Gd_element001,O_element041,S_element012]
  conduct = 2
  density = 1
  expand = 3
  formula = G4_GADOLINIUM_OXYSULFIDE
  name = G4_GADOLINIUM_OXYSULFIDE
  specific = 4
FEATURE [App::DocumentObjectGroupPython] Ga_element001  label="Ga_element : 1"  # scripted group (container) (typed FeaturePython)
  n = 1
  ref = Ga_element
FEATURE [App::DocumentObjectGroupPython] As_element001  label="As_element : 1"  # scripted group (container) (typed FeaturePython)
  n = 1
  ref = As_element
FEATURE [App::DocumentObjectGroupPython] G4_GALLIUM_ARSENIDE  # scripted group (container) (typed FeaturePython)
  Dunit = g/cm3
  Dvalue = 5.31
  Group = -> [Ga_element001,As_element001]
  conduct = 2
  density = 1
  expand = 3
  formula = G4_GALLIUM_ARSENIDE
  name = G4_GALLIUM_ARSENIDE
  specific = 4
FEATURE [App::DocumentObjectGroupPython] H_element041  label="H_element : 0.081"  # scripted group (container) (typed FeaturePython)
  n = 0.08118
FEATURE [App::DocumentObjectGroupPython] C_element048  label="C_element : 0.416"  # scripted group (container) (typed FeaturePython)
  n = 0.41606
FEATURE [App::DocumentObjectGroupPython] N_element018  label="N_element : 0.111"  # scripted group (container) (typed FeaturePython)
  n = 0.11124
FEATURE [App::DocumentObjectGroupPython] O_element042  label="O_element : 0.381"  # scripted group (container) (typed FeaturePython)
  n = 0.38064
FEATURE [App::DocumentObjectGroupPython] S_element013  label="S_element : 0.011"  # scripted group (container) (typed FeaturePython)
  n = 0.01088
FEATURE [App::DocumentObjectGroupPython] G4_GEL_PHOTO_EMULSION  # scripted group (container) (typed FeaturePython)
  Dunit = g/cm3
  Dvalue = 1.2914
  Group = -> [H_element041,C_element048,N_element018,O_element042,S_element013]
  conduct = 2
  density = 1
  expand = 3
  formula = G4_GEL_PHOTO_EMULSION
  name = G4_GEL_PHOTO_EMULSION
  specific = 4
FEATURE [App::DocumentObjectGroupPython] B_element004  label="B_element : 0.040"  # scripted group (container) (typed FeaturePython)
  n = 0.0400639
FEATURE [App::DocumentObjectGroupPython] O_element043  label="O_element : 0.540"  # scripted group (container) (typed FeaturePython)
  n = 0.539561
FEATURE [App::DocumentObjectGroupPython] Na_element008  label="Na_element : 0.028"  # scripted group (container) (typed FeaturePython)
  n = 0.0281909
FEATURE [App::DocumentObjectGroupPython] Al_element003  label="Al_element : 0.012"  # scripted group (container) (typed FeaturePython)
  n = 0.011644
FEATURE [App::DocumentObjectGroupPython] Si_element003  label="Si_element : 0.377"  # scripted group (container) (typed FeaturePython)
  n = 0.377219
FEATURE [App::DocumentObjectGroupPython] K_element004  label="K_element : 0.014"  # scripted group (container) (typed FeaturePython)
  n = 0.00332099
FEATURE [App::DocumentObjectGroupPython] G4_Pyrex_Glass  # scripted group (container) (typed FeaturePython)
  Dunit = g/cm3
  Dvalue = 2.23
  Group = -> [B_element004,O_element043,Na_element008,Al_element003,Si_element003,K_element004]
  conduct = 2
  density = 1
  expand = 3
  formula = G4_Pyrex_Glass
  name = G4_Pyrex_Glass
  specific = 4
FEATURE [App::DocumentObjectGroupPython] O_element044  label="O_element : 0.156"  # scripted group (container) (typed FeaturePython)
  n = 0.156453
FEATURE [App::DocumentObjectGroupPython] Si_element004  label="Si_element : 0.081"  # scripted group (container) (typed FeaturePython)
  n = 0.080866
FEATURE [App::DocumentObjectGroupPython] Ti_element001  label="Ti_element : 0.008"  # scripted group (container) (typed FeaturePython)
  n = 0.008092
FEATURE [App::DocumentObjectGroupPython] As_element002  label="As_element : 0.003"  # scripted group (container) (typed FeaturePython)
  n = 0.002651
FEATURE [App::DocumentObjectGroupPython] Pb_element001  label="Pb_element : 0.752"  # scripted group (container) (typed FeaturePython)
  n = 0.751938
FEATURE [App::DocumentObjectGroupPython] G4_GLASS_LEAD  # scripted group (container) (typed FeaturePython)
  Dunit = g/cm3
  Dvalue = 6.22
  Group = -> [O_element044,Si_element004,Ti_element001,As_element002,Pb_element001]
  conduct = 2
  density = 1
  expand = 3
  formula = G4_GLASS_LEAD
  name = G4_GLASS_LEAD
  specific = 4
FEATURE [App::DocumentObjectGroupPython] O_element045  label="O_element : 0.460"  # scripted group (container) (typed FeaturePython)
  n = 0.4598
FEATURE [App::DocumentObjectGroupPython] Na_element009  label="Na_element : 0.096"  # scripted group (container) (typed FeaturePython)
  n = 0.0964411
FEATURE [App::DocumentObjectGroupPython] Si_element005  label="Si_element : 0.378"  # scripted group (container) (typed FeaturePython)
  n = 0.336553
FEATURE [App::DocumentObjectGroupPython] Ca_element011  label="Ca_element : 0.107"  # scripted group (container) (typed FeaturePython)
  n = 0.107205
FEATURE [App::DocumentObjectGroupPython] G4_GLASS_PLATE  # scripted group (container) (typed FeaturePython)
  Dunit = g/cm3
  Dvalue = 2.4
  Group = -> [O_element045,Na_element009,Si_element005,Ca_element011]
  conduct = 2
  density = 1
  expand = 3
  formula = G4_GLASS_PLATE
  name = G4_GLASS_PLATE
  specific = 4
FEATURE [App::DocumentObjectGroupPython] C_element049  label="C_element : 026"  # scripted group (container) (typed FeaturePython)
  n = 5
  ref = C_element
FEATURE [App::DocumentObjectGroupPython] H_element042  label="H_element : 021"  # scripted group (container) (typed FeaturePython)
  n = 10
  ref = H_element
FEATURE [App::DocumentObjectGroupPython] N_element019  label="N_element : 2"  # scripted group (container) (typed FeaturePython)
  n = 2
  ref = N_element
FEATURE [App::DocumentObjectGroupPython] O_element046  label="O_element : 022"  # scripted group (container) (typed FeaturePython)
  n = 3
  ref = O_element
FEATURE [App::DocumentObjectGroupPython] G4_GLUTAMINE  # scripted group (container) (typed FeaturePython)
  Dunit = g/cm3
  Dvalue = 1.46
  Group = -> [C_element049,H_element042,N_element019,O_element046]
  conduct = 2
  density = 1
  expand = 3
  formula = G4_GLUTAMINE
  name = G4_GLUTAMINE
  specific = 4
FEATURE [App::DocumentObjectGroupPython] C_element050  label="C_element : 027"  # scripted group (container) (typed FeaturePython)
  n = 3
  ref = C_element
FEATURE [App::DocumentObjectGroupPython] H_element043  label="H_element : 022"  # scripted group (container) (typed FeaturePython)
  n = 8
  ref = H_element
FEATURE [App::DocumentObjectGroupPython] O_element047  label="O_element : 023"  # scripted group (container) (typed FeaturePython)
  n = 3
  ref = O_element
FEATURE [App::DocumentObjectGroupPython] G4_GLYCEROL  # scripted group (container) (typed FeaturePython)
  Dunit = g/cm3
  Dvalue = 1.2613
  Group = -> [C_element050,H_element043,O_element047]
  conduct = 2
  density = 1
  expand = 3
  formula = G4_GLYCEROL
  name = G4_GLYCEROL
  specific = 4
FEATURE [App::DocumentObjectGroupPython] C_element051  label="C_element : 028"  # scripted group (container) (typed FeaturePython)
  n = 5
  ref = C_element
FEATURE [App::DocumentObjectGroupPython] H_element044  label="H_element : 023"  # scripted group (container) (typed FeaturePython)
  n = 5
  ref = H_element
FEATURE [App::DocumentObjectGroupPython] N_element020  label="N_element : 009"  # scripted group (container) (typed FeaturePython)
  n = 5
  ref = N_element
FEATURE [App::DocumentObjectGroupPython] O_element048  label="O_element : 024"  # scripted group (container) (typed FeaturePython)
  n = 1
  ref = O_element
FEATURE [App::DocumentObjectGroupPython] G4_GUANINE  # scripted group (container) (typed FeaturePython)
  Dunit = g/cm3
  Dvalue = 2.2
  Group = -> [C_element051,H_element044,N_element020,O_element048]
  conduct = 2
  density = 1
  expand = 3
  formula = G4_GUANINE
  name = G4_GUANINE
  specific = 4
FEATURE [App::DocumentObjectGroupPython] Ca_element012  label="Ca_element : 006"  # scripted group (container) (typed FeaturePython)
  n = 1
  ref = Ca_element
FEATURE [App::DocumentObjectGroupPython] S_element014  label="S_element : 005"  # scripted group (container) (typed FeaturePython)
  n = 1
  ref = S_element
FEATURE [App::DocumentObjectGroupPython] O_element049  label="O_element : 6"  # scripted group (container) (typed FeaturePython)
  n = 6
  ref = O_element
FEATURE [App::DocumentObjectGroupPython] H_element045  label="H_element : 024"  # scripted group (container) (typed FeaturePython)
  n = 4
  ref = H_element
FEATURE [App::DocumentObjectGroupPython] G4_GYPSUM  # scripted group (container) (typed FeaturePython)
  Dunit = g/cm3
  Dvalue = 2.32
  Group = -> [Ca_element012,S_element014,O_element049,H_element045]
  conduct = 2
  density = 1
  expand = 3
  formula = G4_GYPSUM
  name = G4_GYPSUM
  specific = 4
FEATURE [App::DocumentObjectGroupPython] C_element052  label="C_element : 7"  # scripted group (container) (typed FeaturePython)
  n = 7
  ref = C_element
FEATURE [App::DocumentObjectGroupPython] H_element046  label="H_element : 16"  # scripted group (container) (typed FeaturePython)
  n = 16
  ref = H_element
FEATURE [App::DocumentObjectGroupPython] G4_N_HEPTANE  label="G4_N-HEPTANE"  # scripted group (container) (typed FeaturePython)
  Dunit = g/cm3
  Dvalue = 0.68376
  Group = -> [C_element052,H_element046]
  conduct = 2
  density = 1
  expand = 3
  formula = G4_N-HEPTANE
  name = G4_N-HEPTANE
  specific = 4
FEATURE [App::DocumentObjectGroupPython] C_element053  label="C_element : 029"  # scripted group (container) (typed FeaturePython)
  n = 6
  ref = C_element
FEATURE [App::DocumentObjectGroupPython] H_element047  label="H_element : 14"  # scripted group (container) (typed FeaturePython)
  n = 14
  ref = H_element
FEATURE [App::DocumentObjectGroupPython] G4_N_HEXANE  label="G4_N-HEXANE"  # scripted group (container) (typed FeaturePython)
  Dunit = g/cm3
  Dvalue = 0.6603
  Group = -> [C_element053,H_element047]
  conduct = 2
  density = 1
  expand = 3
  formula = G4_N-HEXANE
  name = G4_N-HEXANE
  specific = 4
FEATURE [App::DocumentObjectGroupPython] C_element054  label="C_element : 22"  # scripted group (container) (typed FeaturePython)
  n = 22
  ref = C_element
FEATURE [App::DocumentObjectGroupPython] H_element048  label="H_element : 025"  # scripted group (container) (typed FeaturePython)
  n = 10
  ref = H_element
FEATURE [App::DocumentObjectGroupPython] N_element021  label="N_element : 010"  # scripted group (container) (typed FeaturePython)
  n = 2
  ref = N_element
FEATURE [App::DocumentObjectGroupPython] O_element050  label="O_element : 025"  # scripted group (container) (typed FeaturePython)
  n = 5
  ref = O_element
FEATURE [App::DocumentObjectGroupPython] G4_KAPTON  # scripted group (container) (typed FeaturePython)
  Dunit = g/cm3
  Dvalue = 1.42
  Group = -> [C_element054,H_element048,N_element021,O_element050]
  conduct = 2
  density = 1
  expand = 3
  formula = G4_KAPTON
  name = G4_KAPTON
  specific = 4
FEATURE [App::DocumentObjectGroupPython] La_element001  label="La_element : 1"  # scripted group (container) (typed FeaturePython)
  n = 1
  ref = La_element
FEATURE [App::DocumentObjectGroupPython] Br_element003  label="Br_element : 002"  # scripted group (container) (typed FeaturePython)
  n = 1
  ref = Br_element
FEATURE [App::DocumentObjectGroupPython] O_element051  label="O_element : 026"  # scripted group (container) (typed FeaturePython)
  n = 1
  ref = O_element
FEATURE [App::DocumentObjectGroupPython] G4_LANTHANUM_OXYBROMIDE  # scripted group (container) (typed FeaturePython)
  Dunit = g/cm3
  Dvalue = 6.28
  Group = -> [La_element001,Br_element003,O_element051]
  conduct = 2
  density = 1
  expand = 3
  formula = G4_LANTHANUM_OXYBROMIDE
  name = G4_LANTHANUM_OXYBROMIDE
  specific = 4
FEATURE [App::DocumentObjectGroupPython] La_element002  label="La_element : 2"  # scripted group (container) (typed FeaturePython)
  n = 2
  ref = La_element
FEATURE [App::DocumentObjectGroupPython] O_element052  label="O_element : 027"  # scripted group (container) (typed FeaturePython)
  n = 2
  ref = O_element
FEATURE [App::DocumentObjectGroupPython] S_element015  label="S_element : 006"  # scripted group (container) (typed FeaturePython)
  n = 1
  ref = S_element
FEATURE [App::DocumentObjectGroupPython] G4_LANTHANUM_OXYSULFIDE  # scripted group (container) (typed FeaturePython)
  Dunit = g/cm3
  Dvalue = 5.86
  Group = -> [La_element002,O_element052,S_element015]
  conduct = 2
  density = 1
  expand = 3
  formula = G4_LANTHANUM_OXYSULFIDE
  name = G4_LANTHANUM_OXYSULFIDE
  specific = 4
FEATURE [App::DocumentObjectGroupPython] O_element053  label="O_element : 0.072"  # scripted group (container) (typed FeaturePython)
  n = 0.071682
FEATURE [App::DocumentObjectGroupPython] Pb_element002  label="Pb_element : 0.928"  # scripted group (container) (typed FeaturePython)
  n = 0.928318
FEATURE [App::DocumentObjectGroupPython] G4_LEAD_OXIDE  # scripted group (container) (typed FeaturePython)
  Dunit = g/cm3
  Dvalue = 9.53
  Group = -> [O_element053,Pb_element002]
  conduct = 2
  density = 1
  expand = 3
  formula = G4_LEAD_OXIDE
  name = G4_LEAD_OXIDE
  specific = 4
FEATURE [App::DocumentObjectGroupPython] Li_element001  label="Li_element : 1"  # scripted group (container) (typed FeaturePython)
  n = 1
  ref = Li_element
FEATURE [App::DocumentObjectGroupPython] N_element022  label="N_element : 011"  # scripted group (container) (typed FeaturePython)
  n = 1
  ref = N_element
FEATURE [App::DocumentObjectGroupPython] H_element049  label="H_element : 026"  # scripted group (container) (typed FeaturePython)
  n = 2
  ref = H_element
FEATURE [App::DocumentObjectGroupPython] G4_LITHIUM_AMIDE  # scripted group (container) (typed FeaturePython)
  Dunit = g/cm3
  Dvalue = 1.178
  Group = -> [Li_element001,N_element022,H_element049]
  conduct = 2
  density = 1
  expand = 3
  formula = G4_LITHIUM_AMIDE
  name = G4_LITHIUM_AMIDE
  specific = 4
FEATURE [App::DocumentObjectGroupPython] Li_element002  label="Li_element : 2"  # scripted group (container) (typed FeaturePython)
  n = 2
  ref = Li_element
FEATURE [App::DocumentObjectGroupPython] C_element055  label="C_element : 030"  # scripted group (container) (typed FeaturePython)
  n = 1
  ref = C_element
FEATURE [App::DocumentObjectGroupPython] O_element054  label="O_element : 028"  # scripted group (container) (typed FeaturePython)
  n = 3
  ref = O_element
FEATURE [App::DocumentObjectGroupPython] G4_LITHIUM_CARBONATE  # scripted group (container) (typed FeaturePython)
  Dunit = g/cm3
  Dvalue = 2.11
  Group = -> [Li_element002,C_element055,O_element054]
  conduct = 2
  density = 1
  expand = 3
  formula = G4_LITHIUM_CARBONATE
  name = G4_LITHIUM_CARBONATE
  specific = 4
FEATURE [App::DocumentObjectGroupPython] Li_element003  label="Li_element : 003"  # scripted group (container) (typed FeaturePython)
  n = 1
  ref = Li_element
FEATURE [App::DocumentObjectGroupPython] F_element012  label="F_element : 004"  # scripted group (container) (typed FeaturePython)
  n = 1
  ref = F_element
FEATURE [App::DocumentObjectGroupPython] G4_LITHIUM_FLUORIDE  # scripted group (container) (typed FeaturePython)
  Dunit = g/cm3
  Dvalue = 2.635
  Group = -> [Li_element003,F_element012]
  conduct = 2
  density = 1
  expand = 3
  formula = G4_LITHIUM_FLUORIDE
  name = G4_LITHIUM_FLUORIDE
  specific = 4
FEATURE [App::DocumentObjectGroupPython] Li_element004  label="Li_element : 004"  # scripted group (container) (typed FeaturePython)
  n = 1
  ref = Li_element
FEATURE [App::DocumentObjectGroupPython] H_element050  label="H_element : 027"  # scripted group (container) (typed FeaturePython)
  n = 1
  ref = H_element
FEATURE [App::DocumentObjectGroupPython] G4_LITHIUM_HYDRIDE  # scripted group (container) (typed FeaturePython)
  Dunit = g/cm3
  Dvalue = 0.82
  Group = -> [Li_element004,H_element050]
  conduct = 2
  density = 1
  expand = 3
  formula = G4_LITHIUM_HYDRIDE
  name = G4_LITHIUM_HYDRIDE
  specific = 4
FEATURE [App::DocumentObjectGroupPython] Li_element005  label="Li_element : 005"  # scripted group (container) (typed FeaturePython)
  n = 1
  ref = Li_element
FEATURE [App::DocumentObjectGroupPython] I_element003  label="I_element : 002"  # scripted group (container) (typed FeaturePython)
  n = 1
  ref = I_element
FEATURE [App::DocumentObjectGroupPython] G4_LITHIUM_IODIDE  # scripted group (container) (typed FeaturePython)
  Dunit = g/cm3
  Dvalue = 3.494
  Group = -> [Li_element005,I_element003]
  conduct = 2
  density = 1
  expand = 3
  formula = G4_LITHIUM_IODIDE
  name = G4_LITHIUM_IODIDE
  specific = 4
FEATURE [App::DocumentObjectGroupPython] Li_element006  label="Li_element : 006"  # scripted group (container) (typed FeaturePython)
  n = 2
  ref = Li_element
FEATURE [App::DocumentObjectGroupPython] O_element055  label="O_element : 029"  # scripted group (container) (typed FeaturePython)
  n = 1
  ref = O_element
FEATURE [App::DocumentObjectGroupPython] G4_LITHIUM_OXIDE  # scripted group (container) (typed FeaturePython)
  Dunit = g/cm3
  Dvalue = 2.013
  Group = -> [Li_element006,O_element055]
  conduct = 2
  density = 1
  expand = 3
  formula = G4_LITHIUM_OXIDE
  name = G4_LITHIUM_OXIDE
  specific = 4
FEATURE [App::DocumentObjectGroupPython] Li_element007  label="Li_element : 007"  # scripted group (container) (typed FeaturePython)
  n = 2
  ref = Li_element
FEATURE [App::DocumentObjectGroupPython] B_element005  label="B_element : 005"  # scripted group (container) (typed FeaturePython)
  n = 4
  ref = B_element
FEATURE [App::DocumentObjectGroupPython] O_element056  label="O_element : 7"  # scripted group (container) (typed FeaturePython)
  n = 7
  ref = O_element
FEATURE [App::DocumentObjectGroupPython] G4_LITHIUM_TETRABORATE  # scripted group (container) (typed FeaturePython)
  Dunit = g/cm3
  Dvalue = 2.44
  Group = -> [Li_element007,B_element005,O_element056]
  conduct = 2
  density = 1
  expand = 3
  formula = G4_LITHIUM_TETRABORATE
  name = G4_LITHIUM_TETRABORATE
  specific = 4
FEATURE [App::DocumentObjectGroupPython] H_element051  label="H_element : 0.105"  # scripted group (container) (typed FeaturePython)
  n = 0.105
FEATURE [App::DocumentObjectGroupPython] C_element056  label="C_element : 0.083"  # scripted group (container) (typed FeaturePython)
  n = 0.083
FEATURE [App::DocumentObjectGroupPython] N_element023  label="N_element : 0.023"  # scripted group (container) (typed FeaturePython)
  n = 0.023
FEATURE [App::DocumentObjectGroupPython] O_element057  label="O_element : 0.779"  # scripted group (container) (typed FeaturePython)
  n = 0.779
FEATURE [App::DocumentObjectGroupPython] Na_element010  label="Na_element : 0.097"  # scripted group (container) (typed FeaturePython)
  n = 0.002
FEATURE [App::DocumentObjectGroupPython] P_element006  label="P_element : 0.105"  # scripted group (container) (typed FeaturePython)
  n = 0.001
FEATURE [App::DocumentObjectGroupPython] S_element016  label="S_element : 0.017"  # scripted group (container) (typed FeaturePython)
  n = 0.002
FEATURE [App::DocumentObjectGroupPython] Cl_element014  label="Cl_element : 0.587"  # scripted group (container) (typed FeaturePython)
  n = 0.003
FEATURE [App::DocumentObjectGroupPython] K_element005  label="K_element : 0.015"  # scripted group (container) (typed FeaturePython)
  n = 0.002
FEATURE [App::DocumentObjectGroupPython] G4_LUNG_ICRP  # scripted group (container) (typed FeaturePython)
  Dunit = g/cm3
  Dvalue = 1.04
  Group = -> [H_element051,C_element056,N_element023,O_element057,Na_element010,P_element006,S_element016,Cl_element014,K_element005]
  conduct = 2
  density = 1
  expand = 3
  formula = G4_LUNG_ICRP
  name = G4_LUNG_ICRP
  specific = 4
FEATURE [App::DocumentObjectGroupPython] H_element052  label="H_element : 0.116"  # scripted group (container) (typed FeaturePython)
  n = 0.114318
FEATURE [App::DocumentObjectGroupPython] C_element057  label="C_element : 0.656"  # scripted group (container) (typed FeaturePython)
  n = 0.655824
FEATURE [App::DocumentObjectGroupPython] O_element058  label="O_element : 0.092"  # scripted group (container) (typed FeaturePython)
  n = 0.0921831
FEATURE [App::DocumentObjectGroupPython] Mg_element004  label="Mg_element : 0.135"  # scripted group (container) (typed FeaturePython)
  n = 0.134792
FEATURE [App::DocumentObjectGroupPython] Ca_element013  label="Ca_element : 0.003"  # scripted group (container) (typed FeaturePython)
  n = 0.002883
FEATURE [App::DocumentObjectGroupPython] G4_M3_WAX  # scripted group (container) (typed FeaturePython)
  Dunit = g/cm3
  Dvalue = 1.05
  Group = -> [H_element052,C_element057,O_element058,Mg_element004,Ca_element013]
  conduct = 2
  density = 1
  expand = 3
  formula = G4_M3_WAX
  name = G4_M3_WAX
  specific = 4
FEATURE [App::DocumentObjectGroupPython] Mg_element005  label="Mg_element : 1"  # scripted group (container) (typed FeaturePython)
  n = 1
  ref = Mg_element
FEATURE [App::DocumentObjectGroupPython] C_element058  label="C_element : 031"  # scripted group (container) (typed FeaturePython)
  n = 1
  ref = C_element
FEATURE [App::DocumentObjectGroupPython] O_element059  label="O_element : 030"  # scripted group (container) (typed FeaturePython)
  n = 3
  ref = O_element
FEATURE [App::DocumentObjectGroupPython] G4_MAGNESIUM_CARBONATE  # scripted group (container) (typed FeaturePython)
  Dunit = g/cm3
  Dvalue = 2.958
  Group = -> [Mg_element005,C_element058,O_element059]
  conduct = 2
  density = 1
  expand = 3
  formula = G4_MAGNESIUM_CARBONATE
  name = G4_MAGNESIUM_CARBONATE
  specific = 4
FEATURE [App::DocumentObjectGroupPython] Mg_element006  label="Mg_element : 002"  # scripted group (container) (typed FeaturePython)
  n = 1
  ref = Mg_element
FEATURE [App::DocumentObjectGroupPython] F_element013  label="F_element : 005"  # scripted group (container) (typed FeaturePython)
  n = 2
  ref = F_element
FEATURE [App::DocumentObjectGroupPython] G4_MAGNESIUM_FLUORIDE  # scripted group (container) (typed FeaturePython)
  Dunit = g/cm3
  Dvalue = 3
  Group = -> [Mg_element006,F_element013]
  conduct = 2
  density = 1
  expand = 3
  formula = G4_MAGNESIUM_FLUORIDE
  name = G4_MAGNESIUM_FLUORIDE
  specific = 4
FEATURE [App::DocumentObjectGroupPython] Mg_element007  label="Mg_element : 003"  # scripted group (container) (typed FeaturePython)
  n = 1
  ref = Mg_element
FEATURE [App::DocumentObjectGroupPython] O_element060  label="O_element : 031"  # scripted group (container) (typed FeaturePython)
  n = 1
  ref = O_element
FEATURE [App::DocumentObjectGroupPython] G4_MAGNESIUM_OXIDE  # scripted group (container) (typed FeaturePython)
  Dunit = g/cm3
  Dvalue = 3.58
  Group = -> [Mg_element007,O_element060]
  conduct = 2
  density = 1
  expand = 3
  formula = G4_MAGNESIUM_OXIDE
  name = G4_MAGNESIUM_OXIDE
  specific = 4
FEATURE [App::DocumentObjectGroupPython] Mg_element008  label="Mg_element : 004"  # scripted group (container) (typed FeaturePython)
  n = 1
  ref = Mg_element
FEATURE [App::DocumentObjectGroupPython] B_element006  label="B_element : 006"  # scripted group (container) (typed FeaturePython)
  n = 4
  ref = B_element
FEATURE [App::DocumentObjectGroupPython] O_element061  label="O_element : 032"  # scripted group (container) (typed FeaturePython)
  n = 7
  ref = O_element
FEATURE [App::DocumentObjectGroupPython] G4_MAGNESIUM_TETRABORATE  # scripted group (container) (typed FeaturePython)
  Dunit = g/cm3
  Dvalue = 2.53
  Group = -> [Mg_element008,B_element006,O_element061]
  conduct = 2
  density = 1
  expand = 3
  formula = G4_MAGNESIUM_TETRABORATE
  name = G4_MAGNESIUM_TETRABORATE
  specific = 4
FEATURE [App::DocumentObjectGroupPython] Hg_element001  label="Hg_element : 1"  # scripted group (container) (typed FeaturePython)
  n = 1
  ref = Hg_element
FEATURE [App::DocumentObjectGroupPython] I_element004  label="I_element : 2"  # scripted group (container) (typed FeaturePython)
  n = 2
  ref = I_element
FEATURE [App::DocumentObjectGroupPython] G4_MERCURIC_IODIDE  # scripted group (container) (typed FeaturePython)
  Dunit = g/cm3
  Dvalue = 6.36
  Group = -> [Hg_element001,I_element004]
  conduct = 2
  density = 1
  expand = 3
  formula = G4_MERCURIC_IODIDE
  name = G4_MERCURIC_IODIDE
  specific = 4
FEATURE [App::DocumentObjectGroupPython] C_element059  label="C_element : 032"  # scripted group (container) (typed FeaturePython)
  n = 1
  ref = C_element
FEATURE [App::DocumentObjectGroupPython] H_element053  label="H_element : 028"  # scripted group (container) (typed FeaturePython)
  n = 4
  ref = H_element
FEATURE [App::DocumentObjectGroupPython] G4_METHANE  # scripted group (container) (typed FeaturePython)
  Dunit = g/cm3
  Dvalue = 0.000667151
  Group = -> [C_element059,H_element053]
  conduct = 2
  density = 1
  expand = 3
  formula = G4_METHANE
  name = G4_METHANE
  specific = 4
FEATURE [App::DocumentObjectGroupPython] C_element060  label="C_element : 033"  # scripted group (container) (typed FeaturePython)
  n = 1
  ref = C_element
FEATURE [App::DocumentObjectGroupPython] H_element054  label="H_element : 029"  # scripted group (container) (typed FeaturePython)
  n = 4
  ref = H_element
FEATURE [App::DocumentObjectGroupPython] O_element062  label="O_element : 033"  # scripted group (container) (typed FeaturePython)
  n = 1
  ref = O_element
FEATURE [App::DocumentObjectGroupPython] G4_METHANOL  # scripted group (container) (typed FeaturePython)
  Dunit = g/cm3
  Dvalue = 0.7914
  Group = -> [C_element060,H_element054,O_element062]
  conduct = 2
  density = 1
  expand = 3
  formula = G4_METHANOL
  name = G4_METHANOL
  specific = 4
FEATURE [App::DocumentObjectGroupPython] H_element055  label="H_element : 0.134"  # scripted group (container) (typed FeaturePython)
  n = 0.13404
FEATURE [App::DocumentObjectGroupPython] C_element061  label="C_element : 0.778"  # scripted group (container) (typed FeaturePython)
  n = 0.77796
FEATURE [App::DocumentObjectGroupPython] O_element063  label="O_element : 0.035"  # scripted group (container) (typed FeaturePython)
  n = 0.03502
FEATURE [App::DocumentObjectGroupPython] Mg_element009  label="Mg_element : 0.039"  # scripted group (container) (typed FeaturePython)
  n = 0.038594
FEATURE [App::DocumentObjectGroupPython] Ti_element002  label="Ti_element : 0.014"  # scripted group (container) (typed FeaturePython)
  n = 0.014386
FEATURE [App::DocumentObjectGroupPython] G4_MIX_D_WAX  # scripted group (container) (typed FeaturePython)
  Dunit = g/cm3
  Dvalue = 0.99
  Group = -> [H_element055,C_element061,O_element063,Mg_element009,Ti_element002]
  conduct = 2
  density = 1
  expand = 3
  formula = G4_MIX_D_WAX
  name = G4_MIX_D_WAX
  specific = 4
FEATURE [App::DocumentObjectGroupPython] H_element056  label="H_element : 0.135"  # scripted group (container) (typed FeaturePython)
  n = 0.081192
FEATURE [App::DocumentObjectGroupPython] C_element062  label="C_element : 0.583"  # scripted group (container) (typed FeaturePython)
  n = 0.583442
FEATURE [App::DocumentObjectGroupPython] N_element024  label="N_element : 0.018"  # scripted group (container) (typed FeaturePython)
  n = 0.017798
FEATURE [App::DocumentObjectGroupPython] O_element064  label="O_element : 0.186"  # scripted group (container) (typed FeaturePython)
  n = 0.186381
FEATURE [App::DocumentObjectGroupPython] Mg_element010  label="Mg_element : 0.130"  # scripted group (container) (typed FeaturePython)
  n = 0.130287
FEATURE [App::DocumentObjectGroupPython] Cl_element015  label="Cl_element : 0.588"  # scripted group (container) (typed FeaturePython)
  n = 0.0009
FEATURE [App::DocumentObjectGroupPython] G4_MS20_TISSUE  # scripted group (container) (typed FeaturePython)
  Dunit = g/cm3
  Dvalue = 1
  Group = -> [H_element056,C_element062,N_element024,O_element064,Mg_element010,Cl_element015]
  conduct = 2
  density = 1
  expand = 3
  formula = G4_MS20_TISSUE
  name = G4_MS20_TISSUE
  specific = 4
FEATURE [App::DocumentObjectGroupPython] H_element057  label="H_element : 0.136"  # scripted group (container) (typed FeaturePython)
  n = 0.102
FEATURE [App::DocumentObjectGroupPython] C_element063  label="C_element : 0.143"  # scripted group (container) (typed FeaturePython)
  n = 0.143
FEATURE [App::DocumentObjectGroupPython] N_element025  label="N_element : 0.034"  # scripted group (container) (typed FeaturePython)
  n = 0.034
FEATURE [App::DocumentObjectGroupPython] O_element065  label="O_element : 0.710"  # scripted group (container) (typed FeaturePython)
  n = 0.71
FEATURE [App::DocumentObjectGroupPython] Na_element011  label="Na_element : 0.098"  # scripted group (container) (typed FeaturePython)
  n = 0.001
FEATURE [App::DocumentObjectGroupPython] P_element007  label="P_element : 0.002"  # scripted group (container) (typed FeaturePython)
  n = 0.002
FEATURE [App::DocumentObjectGroupPython] S_element017  label="S_element : 0.018"  # scripted group (container) (typed FeaturePython)
  n = 0.003
FEATURE [App::DocumentObjectGroupPython] Cl_element016  label="Cl_element : 0.589"  # scripted group (container) (typed FeaturePython)
  n = 0.001
FEATURE [App::DocumentObjectGroupPython] K_element006  label="K_element : 0.004"  # scripted group (container) (typed FeaturePython)
  n = 0.004
FEATURE [App::DocumentObjectGroupPython] G4_MUSCLE_SKELETAL_ICRP  # scripted group (container) (typed FeaturePython)
  Dunit = g/cm3
  Dvalue = 1.05
  Group = -> [H_element057,C_element063,N_element025,O_element065,Na_element011,P_element007,S_element017,Cl_element016,K_element006]
  conduct = 2
  density = 1
  expand = 3
  formula = G4_MUSCLE_SKELETAL_ICRP
  name = G4_MUSCLE_SKELETAL_ICRP
  specific = 4
FEATURE [App::DocumentObjectGroupPython] H_element058  label="H_element : 0.137"  # scripted group (container) (typed FeaturePython)
  n = 0.102102
FEATURE [App::DocumentObjectGroupPython] C_element064  label="C_element : 0.123"  # scripted group (container) (typed FeaturePython)
  n = 0.123123
FEATURE [App::DocumentObjectGroupPython] N_element026  label="N_element : 0.756"  # scripted group (container) (typed FeaturePython)
  n = 0.035035
FEATURE [App::DocumentObjectGroupPython] O_element066  label="O_element : 0.730"  # scripted group (container) (typed FeaturePython)
  n = 0.72973
FEATURE [App::DocumentObjectGroupPython] Na_element012  label="Na_element : 0.099"  # scripted group (container) (typed FeaturePython)
  n = 0.001001
FEATURE [App::DocumentObjectGroupPython] P_element008  label="P_element : 0.106"  # scripted group (container) (typed FeaturePython)
  n = 0.002002
FEATURE [App::DocumentObjectGroupPython] S_element018  label="S_element : 0.019"  # scripted group (container) (typed FeaturePython)
  n = 0.004004
FEATURE [App::DocumentObjectGroupPython] K_element007  label="K_element : 0.016"  # scripted group (container) (typed FeaturePython)
  n = 0.003003
FEATURE [App::DocumentObjectGroupPython] G4_MUSCLE_STRIATED_ICRU  # scripted group (container) (typed FeaturePython)
  Dunit = g/cm3
  Dvalue = 1.04
  Group = -> [H_element058,C_element064,N_element026,O_element066,Na_element012,P_element008,S_element018,K_element007]
  conduct = 2
  density = 1
  expand = 3
  formula = G4_MUSCLE_STRIATED_ICRU
  name = G4_MUSCLE_STRIATED_ICRU
  specific = 4
FEATURE [App::DocumentObjectGroupPython] H_element059  label="H_element : 0.098"  # scripted group (container) (typed FeaturePython)
  n = 0.0982341
FEATURE [App::DocumentObjectGroupPython] C_element065  label="C_element : 0.156"  # scripted group (container) (typed FeaturePython)
  n = 0.156214
FEATURE [App::DocumentObjectGroupPython] N_element027  label="N_element : 0.757"  # scripted group (container) (typed FeaturePython)
  n = 0.035451
FEATURE [App::DocumentObjectGroupPython] O_element067  label="O_element : 0.880"  # scripted group (container) (typed FeaturePython)
  n = 0.710101
FEATURE [App::DocumentObjectGroupPython] G4_MUSCLE_WITH_SUCROSE  # scripted group (container) (typed FeaturePython)
  Dunit = g/cm3
  Dvalue = 1.11
  Group = -> [H_element059,C_element065,N_element027,O_element067]
  conduct = 2
  density = 1
  expand = 3
  formula = G4_MUSCLE_WITH_SUCROSE
  name = G4_MUSCLE_WITH_SUCROSE
  specific = 4
FEATURE [App::DocumentObjectGroupPython] H_element060  label="H_element : 0.138"  # scripted group (container) (typed FeaturePython)
  n = 0.101969
FEATURE [App::DocumentObjectGroupPython] C_element066  label="C_element : 0.120"  # scripted group (container) (typed FeaturePython)
  n = 0.120058
FEATURE [App::DocumentObjectGroupPython] N_element028  label="N_element : 0.758"  # scripted group (container) (typed FeaturePython)
  n = 0.035451
FEATURE [App::DocumentObjectGroupPython] O_element068  label="O_element : 0.743"  # scripted group (container) (typed FeaturePython)
  n = 0.742522
FEATURE [App::DocumentObjectGroupPython] G4_MUSCLE_WITHOUT_SUCROSE  # scripted group (container) (typed FeaturePython)
  Dunit = g/cm3
  Dvalue = 1.07
  Group = -> [H_element060,C_element066,N_element028,O_element068]
  conduct = 2
  density = 1
  expand = 3
  formula = G4_MUSCLE_WITHOUT_SUCROSE
  name = G4_MUSCLE_WITHOUT_SUCROSE
  specific = 4
FEATURE [App::DocumentObjectGroupPython] C_element067  label="C_element : 10"  # scripted group (container) (typed FeaturePython)
  n = 10
  ref = C_element
FEATURE [App::DocumentObjectGroupPython] H_element061  label="H_element : 030"  # scripted group (container) (typed FeaturePython)
  n = 8
  ref = H_element
FEATURE [App::DocumentObjectGroupPython] G4_NAPHTHALENE  # scripted group (container) (typed FeaturePython)
  Dunit = g/cm3
  Dvalue = 1.145
  Group = -> [C_element067,H_element061]
  conduct = 2
  density = 1
  expand = 3
  formula = G4_NAPHTHALENE
  name = G4_NAPHTHALENE
  specific = 4
FEATURE [App::DocumentObjectGroupPython] C_element068  label="C_element : 034"  # scripted group (container) (typed FeaturePython)
  n = 6
  ref = C_element
FEATURE [App::DocumentObjectGroupPython] H_element062  label="H_element : 031"  # scripted group (container) (typed FeaturePython)
  n = 5
  ref = H_element
FEATURE [App::DocumentObjectGroupPython] N_element029  label="N_element : 012"  # scripted group (container) (typed FeaturePython)
  n = 1
  ref = N_element
FEATURE [App::DocumentObjectGroupPython] O_element069  label="O_element : 034"  # scripted group (container) (typed FeaturePython)
  n = 2
  ref = O_element
FEATURE [App::DocumentObjectGroupPython] G4_NITROBENZENE  # scripted group (container) (typed FeaturePython)
  Dunit = g/cm3
  Dvalue = 1.19867
  Group = -> [C_element068,H_element062,N_element029,O_element069]
  conduct = 2
  density = 1
  expand = 3
  formula = G4_NITROBENZENE
  name = G4_NITROBENZENE
  specific = 4
FEATURE [App::DocumentObjectGroupPython] N_element030  label="N_element : 013"  # scripted group (container) (typed FeaturePython)
  n = 2
  ref = N_element
FEATURE [App::DocumentObjectGroupPython] O_element070  label="O_element : 035"  # scripted group (container) (typed FeaturePython)
  n = 1
  ref = O_element
FEATURE [App::DocumentObjectGroupPython] G4_NITROUS_OXIDE  # scripted group (container) (typed FeaturePython)
  Dunit = g/cm3
  Dvalue = 0.00183094
  Group = -> [N_element030,O_element070]
  conduct = 2
  density = 1
  expand = 3
  formula = G4_NITROUS_OXIDE
  name = G4_NITROUS_OXIDE
  specific = 4
FEATURE [App::DocumentObjectGroupPython] H_element063  label="H_element : 0.104"  # scripted group (container) (typed FeaturePython)
  n = 0.103509
FEATURE [App::DocumentObjectGroupPython] C_element069  label="C_element : 0.648"  # scripted group (container) (typed FeaturePython)
  n = 0.648416
FEATURE [App::DocumentObjectGroupPython] N_element031  label="N_element : 0.100"  # scripted group (container) (typed FeaturePython)
  n = 0.0995361
FEATURE [App::DocumentObjectGroupPython] O_element071  label="O_element : 0.149"  # scripted group (container) (typed FeaturePython)
  n = 0.148539
FEATURE [App::DocumentObjectGroupPython] G4_NYLON_8062  label="G4_NYLON-8062"  # scripted group (container) (typed FeaturePython)
  Dunit = g/cm3
  Dvalue = 1.08
  Group = -> [H_element063,C_element069,N_element031,O_element071]
  conduct = 2
  density = 1
  expand = 3
  formula = G4_NYLON-8062
  name = G4_NYLON-8062
  specific = 4
FEATURE [App::DocumentObjectGroupPython] C_element070  label="C_element : 035"  # scripted group (container) (typed FeaturePython)
  n = 6
  ref = C_element
FEATURE [App::DocumentObjectGroupPython] H_element064  label="H_element : 11"  # scripted group (container) (typed FeaturePython)
  n = 11
  ref = H_element
FEATURE [App::DocumentObjectGroupPython] N_element032  label="N_element : 014"  # scripted group (container) (typed FeaturePython)
  n = 1
  ref = N_element
FEATURE [App::DocumentObjectGroupPython] O_element072  label="O_element : 036"  # scripted group (container) (typed FeaturePython)
  n = 1
  ref = O_element
FEATURE [App::DocumentObjectGroupPython] G4_NYLON_6_6  label="G4_NYLON-6-6"  # scripted group (container) (typed FeaturePython)
  Dunit = g/cm3
  Dvalue = 1.14
  Group = -> [C_element070,H_element064,N_element032,O_element072]
  conduct = 2
  density = 1
  expand = 3
  formula = G4_NYLON-6-6
  name = G4_NYLON-6-6
  specific = 4
FEATURE [App::DocumentObjectGroupPython] H_element065  label="H_element : 0.139"  # scripted group (container) (typed FeaturePython)
  n = 0.107062
FEATURE [App::DocumentObjectGroupPython] C_element071  label="C_element : 0.680"  # scripted group (container) (typed FeaturePython)
  n = 0.680449
FEATURE [App::DocumentObjectGroupPython] N_element033  label="N_element : 0.099"  # scripted group (container) (typed FeaturePython)
  n = 0.099189
FEATURE [App::DocumentObjectGroupPython] O_element073  label="O_element : 0.113"  # scripted group (container) (typed FeaturePython)
  n = 0.1133
FEATURE [App::DocumentObjectGroupPython] G4_NYLON_6_10  label="G4_NYLON-6-10"  # scripted group (container) (typed FeaturePython)
  Dunit = g/cm3
  Dvalue = 1.14
  Group = -> [H_element065,C_element071,N_element033,O_element073]
  conduct = 2
  density = 1
  expand = 3
  formula = G4_NYLON-6-10
  name = G4_NYLON-6-10
  specific = 4
FEATURE [App::DocumentObjectGroupPython] H_element066  label="H_element : 0.140"  # scripted group (container) (typed FeaturePython)
  n = 0.115476
FEATURE [App::DocumentObjectGroupPython] C_element072  label="C_element : 0.721"  # scripted group (container) (typed FeaturePython)
  n = 0.720818
FEATURE [App::DocumentObjectGroupPython] N_element034  label="N_element : 0.076"  # scripted group (container) (typed FeaturePython)
  n = 0.0764169
FEATURE [App::DocumentObjectGroupPython] O_element074  label="O_element : 0.087"  # scripted group (container) (typed FeaturePython)
  n = 0.0872889
FEATURE [App::DocumentObjectGroupPython] G4_NYLON_11_RILSAN  label="G4_NYLON-11_RILSAN"  # scripted group (container) (typed FeaturePython)
  Dunit = g/cm3
  Dvalue = 1.425
  Group = -> [H_element066,C_element072,N_element034,O_element074]
  conduct = 2
  density = 1
  expand = 3
  formula = G4_NYLON-11_RILSAN
  name = G4_NYLON-11_RILSAN
  specific = 4
FEATURE [App::DocumentObjectGroupPython] C_element073  label="C_element : 8"  # scripted group (container) (typed FeaturePython)
  n = 8
  ref = C_element
FEATURE [App::DocumentObjectGroupPython] H_element067  label="H_element : 18"  # scripted group (container) (typed FeaturePython)
  n = 18
  ref = H_element
FEATURE [App::DocumentObjectGroupPython] G4_OCTANE  # scripted group (container) (typed FeaturePython)
  Dunit = g/cm3
  Dvalue = 0.7026
  Group = -> [C_element073,H_element067]
  conduct = 2
  density = 1
  expand = 3
  formula = G4_OCTANE
  name = G4_OCTANE
  specific = 4
FEATURE [App::DocumentObjectGroupPython] C_element074  label="C_element : 25"  # scripted group (container) (typed FeaturePython)
  n = 25
  ref = C_element
FEATURE [App::DocumentObjectGroupPython] H_element068  label="H_element : 52"  # scripted group (container) (typed FeaturePython)
  n = 52
  ref = H_element
FEATURE [App::DocumentObjectGroupPython] G4_PARAFFIN  # scripted group (container) (typed FeaturePython)
  Dunit = g/cm3
  Dvalue = 0.93
  Group = -> [C_element074,H_element068]
  conduct = 2
  density = 1
  expand = 3
  formula = G4_PARAFFIN
  name = G4_PARAFFIN
  specific = 4
FEATURE [App::DocumentObjectGroupPython] C_element075  label="C_element : 036"  # scripted group (container) (typed FeaturePython)
  n = 5
  ref = C_element
FEATURE [App::DocumentObjectGroupPython] H_element069  label="H_element : 032"  # scripted group (container) (typed FeaturePython)
  n = 12
  ref = H_element
FEATURE [App::DocumentObjectGroupPython] G4_N_PENTANE  label="G4_N-PENTANE"  # scripted group (container) (typed FeaturePython)
  Dunit = g/cm3
  Dvalue = 0.6262
  Group = -> [C_element075,H_element069]
  conduct = 2
  density = 1
  expand = 3
  formula = G4_N-PENTANE
  name = G4_N-PENTANE
  specific = 4
FEATURE [App::DocumentObjectGroupPython] H_element070  label="H_element : 0.014"  # scripted group (container) (typed FeaturePython)
  n = 0.0141
FEATURE [App::DocumentObjectGroupPython] C_element076  label="C_element : 0.072"  # scripted group (container) (typed FeaturePython)
  n = 0.072261
FEATURE [App::DocumentObjectGroupPython] N_element035  label="N_element : 0.019"  # scripted group (container) (typed FeaturePython)
  n = 0.01932
FEATURE [App::DocumentObjectGroupPython] O_element075  label="O_element : 0.066"  # scripted group (container) (typed FeaturePython)
  n = 0.066101
FEATURE [App::DocumentObjectGroupPython] S_element019  label="S_element : 0.020"  # scripted group (container) (typed FeaturePython)
  n = 0.00189
FEATURE [App::DocumentObjectGroupPython] Br_element004  label="Br_element : 0.349"  # scripted group (container) (typed FeaturePython)
  n = 0.349103
FEATURE [App::DocumentObjectGroupPython] Ag_element001  label="Ag_element : 0.474"  # scripted group (container) (typed FeaturePython)
  n = 0.474105
FEATURE [App::DocumentObjectGroupPython] I_element005  label="I_element : 0.003"  # scripted group (container) (typed FeaturePython)
  n = 0.00312
FEATURE [App::DocumentObjectGroupPython] G4_PHOTO_EMULSION  # scripted group (container) (typed FeaturePython)
  Dunit = g/cm3
  Dvalue = 3.815
  Group = -> [H_element070,C_element076,N_element035,O_element075,S_element019,Br_element004,Ag_element001,I_element005]
  conduct = 2
  density = 1
  expand = 3
  formula = G4_PHOTO_EMULSION
  name = G4_PHOTO_EMULSION
  specific = 4
FEATURE [App::DocumentObjectGroupPython] C_element077  label="C_element : 9"  # scripted group (container) (typed FeaturePython)
  n = 9
  ref = C_element
FEATURE [App::DocumentObjectGroupPython] H_element071  label="H_element : 033"  # scripted group (container) (typed FeaturePython)
  n = 10
  ref = H_element
FEATURE [App::DocumentObjectGroupPython] G4_PLASTIC_SC_VINYLTOLUENE  # scripted group (container) (typed FeaturePython)
  Dunit = g/cm3
  Dvalue = 1.032
  Group = -> [C_element077,H_element071]
  conduct = 2
  density = 1
  expand = 3
  formula = G4_PLASTIC_SC_VINYLTOLUENE
  name = G4_PLASTIC_SC_VINYLTOLUENE
  specific = 4
FEATURE [App::DocumentObjectGroupPython] Pu_element001  label="Pu_element : 1"  # scripted group (container) (typed FeaturePython)
  n = 1
  ref = Pu_element
FEATURE [App::DocumentObjectGroupPython] O_element076  label="O_element : 037"  # scripted group (container) (typed FeaturePython)
  n = 2
  ref = O_element
FEATURE [App::DocumentObjectGroupPython] G4_PLUTONIUM_DIOXIDE  # scripted group (container) (typed FeaturePython)
  Dunit = g/cm3
  Dvalue = 11.46
  Group = -> [Pu_element001,O_element076]
  conduct = 2
  density = 1
  expand = 3
  formula = G4_PLUTONIUM_DIOXIDE
  name = G4_PLUTONIUM_DIOXIDE
  specific = 4
FEATURE [App::DocumentObjectGroupPython] C_element078  label="C_element : 037"  # scripted group (container) (typed FeaturePython)
  n = 3
  ref = C_element
FEATURE [App::DocumentObjectGroupPython] H_element072  label="H_element : 034"  # scripted group (container) (typed FeaturePython)
  n = 3
  ref = H_element
FEATURE [App::DocumentObjectGroupPython] N_element036  label="N_element : 015"  # scripted group (container) (typed FeaturePython)
  n = 1
  ref = N_element
FEATURE [App::DocumentObjectGroupPython] G4_POLYACRYLONITRILE  # scripted group (container) (typed FeaturePython)
  Dunit = g/cm3
  Dvalue = 1.17
  Group = -> [C_element078,H_element072,N_element036]
  conduct = 2
  density = 1
  expand = 3
  formula = G4_POLYACRYLONITRILE
  name = G4_POLYACRYLONITRILE
  specific = 4
FEATURE [App::DocumentObjectGroupPython] C_element079  label="C_element : 16"  # scripted group (container) (typed FeaturePython)
  n = 16
  ref = C_element
FEATURE [App::DocumentObjectGroupPython] H_element073  label="H_element : 035"  # scripted group (container) (typed FeaturePython)
  n = 14
  ref = H_element
FEATURE [App::DocumentObjectGroupPython] O_element077  label="O_element : 038"  # scripted group (container) (typed FeaturePython)
  n = 3
  ref = O_element
FEATURE [App::DocumentObjectGroupPython] G4_POLYCARBONATE  # scripted group (container) (typed FeaturePython)
  Dunit = g/cm3
  Dvalue = 1.2
  Group = -> [C_element079,H_element073,O_element077]
  conduct = 2
  density = 1
  expand = 3
  formula = G4_POLYCARBONATE
  name = G4_POLYCARBONATE
  specific = 4
FEATURE [App::DocumentObjectGroupPython] C_element080  label="C_element : 038"  # scripted group (container) (typed FeaturePython)
  n = 8
  ref = C_element
FEATURE [App::DocumentObjectGroupPython] H_element074  label="H_element : 036"  # scripted group (container) (typed FeaturePython)
  n = 7
  ref = H_element
FEATURE [App::DocumentObjectGroupPython] Cl_element017  label="Cl_element : 007"  # scripted group (container) (typed FeaturePython)
  n = 1
  ref = Cl_element
FEATURE [App::DocumentObjectGroupPython] G4_POLYCHLOROSTYRENE  # scripted group (container) (typed FeaturePython)
  Dunit = g/cm3
  Dvalue = 1.3
  Group = -> [C_element080,H_element074,Cl_element017]
  conduct = 2
  density = 1
  expand = 3
  formula = G4_POLYCHLOROSTYRENE
  name = G4_POLYCHLOROSTYRENE
  specific = 4
FEATURE [App::DocumentObjectGroupPython] C_element081  label="C_element : 039"  # scripted group (container) (typed FeaturePython)
  n = 1
  ref = C_element
FEATURE [App::DocumentObjectGroupPython] H_element075  label="H_element : 037"  # scripted group (container) (typed FeaturePython)
  n = 2
  ref = H_element
FEATURE [App::DocumentObjectGroupPython] G4_POLYETHYLENE  # scripted group (container) (typed FeaturePython)
  Dunit = g/cm3
  Dvalue = 0.94
  Group = -> [C_element081,H_element075]
  conduct = 2
  density = 1
  expand = 3
  formula = G4_POLYETHYLENE
  name = G4_POLYETHYLENE
  specific = 4
FEATURE [App::DocumentObjectGroupPython] C_element082  label="C_element : 040"  # scripted group (container) (typed FeaturePython)
  n = 10
  ref = C_element
FEATURE [App::DocumentObjectGroupPython] H_element076  label="H_element : 038"  # scripted group (container) (typed FeaturePython)
  n = 8
  ref = H_element
FEATURE [App::DocumentObjectGroupPython] O_element078  label="O_element : 039"  # scripted group (container) (typed FeaturePython)
  n = 4
  ref = O_element
FEATURE [App::DocumentObjectGroupPython] G4_MYLAR  # scripted group (container) (typed FeaturePython)
  Dunit = g/cm3
  Dvalue = 1.4
  Group = -> [C_element082,H_element076,O_element078]
  conduct = 2
  density = 1
  expand = 3
  formula = G4_MYLAR
  name = G4_MYLAR
  specific = 4
FEATURE [App::DocumentObjectGroupPython] C_element083  label="C_element : 041"  # scripted group (container) (typed FeaturePython)
  n = 5
  ref = C_element
FEATURE [App::DocumentObjectGroupPython] H_element077  label="H_element : 039"  # scripted group (container) (typed FeaturePython)
  n = 8
  ref = H_element
FEATURE [App::DocumentObjectGroupPython] O_element079  label="O_element : 040"  # scripted group (container) (typed FeaturePython)
  n = 2
  ref = O_element
FEATURE [App::DocumentObjectGroupPython] G4_PLEXIGLASS  # scripted group (container) (typed FeaturePython)
  Dunit = g/cm3
  Dvalue = 1.19
  Group = -> [C_element083,H_element077,O_element079]
  conduct = 2
  density = 1
  expand = 3
  formula = G4_PLEXIGLASS
  name = G4_PLEXIGLASS
  specific = 4
FEATURE [App::DocumentObjectGroupPython] C_element084  label="C_element : 042"  # scripted group (container) (typed FeaturePython)
  n = 1
  ref = C_element
FEATURE [App::DocumentObjectGroupPython] H_element078  label="H_element : 040"  # scripted group (container) (typed FeaturePython)
  n = 2
  ref = H_element
FEATURE [App::DocumentObjectGroupPython] O_element080  label="O_element : 041"  # scripted group (container) (typed FeaturePython)
  n = 1
  ref = O_element
FEATURE [App::DocumentObjectGroupPython] G4_POLYOXYMETHYLENE  # scripted group (container) (typed FeaturePython)
  Dunit = g/cm3
  Dvalue = 1.425
  Group = -> [C_element084,H_element078,O_element080]
  conduct = 2
  density = 1
  expand = 3
  formula = G4_POLYOXYMETHYLENE
  name = G4_POLYOXYMETHYLENE
  specific = 4
FEATURE [App::DocumentObjectGroupPython] C_element085  label="C_element : 043"  # scripted group (container) (typed FeaturePython)
  n = 2
  ref = C_element
FEATURE [App::DocumentObjectGroupPython] H_element079  label="H_element : 041"  # scripted group (container) (typed FeaturePython)
  n = 4
  ref = H_element
FEATURE [App::DocumentObjectGroupPython] G4_POLYPROPYLENE  # scripted group (container) (typed FeaturePython)
  Dunit = g/cm3
  Dvalue = 0.9
  Group = -> [C_element085,H_element079]
  conduct = 2
  density = 1
  expand = 3
  formula = G4_POLYPROPYLENE
  name = G4_POLYPROPYLENE
  specific = 4
FEATURE [App::DocumentObjectGroupPython] C_element086  label="C_element : 044"  # scripted group (container) (typed FeaturePython)
  n = 8
  ref = C_element
FEATURE [App::DocumentObjectGroupPython] H_element080  label="H_element : 042"  # scripted group (container) (typed FeaturePython)
  n = 8
  ref = H_element
FEATURE [App::DocumentObjectGroupPython] G4_POLYSTYRENE  # scripted group (container) (typed FeaturePython)
  Dunit = g/cm3
  Dvalue = 1.06
  Group = -> [C_element086,H_element080]
  conduct = 2
  density = 1
  expand = 3
  formula = G4_POLYSTYRENE
  name = G4_POLYSTYRENE
  specific = 4
FEATURE [App::DocumentObjectGroupPython] C_element087  label="C_element : 045"  # scripted group (container) (typed FeaturePython)
  n = 2
  ref = C_element
FEATURE [App::DocumentObjectGroupPython] F_element014  label="F_element : 4"  # scripted group (container) (typed FeaturePython)
  n = 4
  ref = F_element
FEATURE [App::DocumentObjectGroupPython] G4_TEFLON  # scripted group (container) (typed FeaturePython)
  Dunit = g/cm3
  Dvalue = 2.2
  Group = -> [C_element087,F_element014]
  conduct = 2
  density = 1
  expand = 3
  formula = G4_TEFLON
  name = G4_TEFLON
  specific = 4
FEATURE [App::DocumentObjectGroupPython] C_element088  label="C_element : 046"  # scripted group (container) (typed FeaturePython)
  n = 2
  ref = C_element
FEATURE [App::DocumentObjectGroupPython] F_element015  label="F_element : 006"  # scripted group (container) (typed FeaturePython)
  n = 3
  ref = F_element
FEATURE [App::DocumentObjectGroupPython] Cl_element018  label="Cl_element : 008"  # scripted group (container) (typed FeaturePython)
  n = 1
  ref = Cl_element
FEATURE [App::DocumentObjectGroupPython] G4_POLYTRIFLUOROCHLOROETHYLENE  # scripted group (container) (typed FeaturePython)
  Dunit = g/cm3
  Dvalue = 2.1
  Group = -> [C_element088,F_element015,Cl_element018]
  conduct = 2
  density = 1
  expand = 3
  formula = G4_POLYTRIFLUOROCHLOROETHYLENE
  name = G4_POLYTRIFLUOROCHLOROETHYLENE
  specific = 4
FEATURE [App::DocumentObjectGroupPython] C_element089  label="C_element : 047"  # scripted group (container) (typed FeaturePython)
  n = 4
  ref = C_element
FEATURE [App::DocumentObjectGroupPython] H_element081  label="H_element : 043"  # scripted group (container) (typed FeaturePython)
  n = 6
  ref = H_element
FEATURE [App::DocumentObjectGroupPython] O_element081  label="O_element : 042"  # scripted group (container) (typed FeaturePython)
  n = 2
  ref = O_element
FEATURE [App::DocumentObjectGroupPython] G4_POLYVINYL_ACETATE  # scripted group (container) (typed FeaturePython)
  Dunit = g/cm3
  Dvalue = 1.19
  Group = -> [C_element089,H_element081,O_element081]
  conduct = 2
  density = 1
  expand = 3
  formula = G4_POLYVINYL_ACETATE
  name = G4_POLYVINYL_ACETATE
  specific = 4
FEATURE [App::DocumentObjectGroupPython] C_element090  label="C_element : 048"  # scripted group (container) (typed FeaturePython)
  n = 2
  ref = C_element
FEATURE [App::DocumentObjectGroupPython] H_element082  label="H_element : 044"  # scripted group (container) (typed FeaturePython)
  n = 4
  ref = H_element
FEATURE [App::DocumentObjectGroupPython] O_element082  label="O_element : 043"  # scripted group (container) (typed FeaturePython)
  n = 1
  ref = O_element
FEATURE [App::DocumentObjectGroupPython] G4_POLYVINYL_ALCOHOL  # scripted group (container) (typed FeaturePython)
  Dunit = g/cm3
  Dvalue = 1.3
  Group = -> [C_element090,H_element082,O_element082]
  conduct = 2
  density = 1
  expand = 3
  formula = G4_POLYVINYL_ALCOHOL
  name = G4_POLYVINYL_ALCOHOL
  specific = 4
FEATURE [App::DocumentObjectGroupPython] C_element091  label="C_element : 049"  # scripted group (container) (typed FeaturePython)
  n = 8
  ref = C_element
FEATURE [App::DocumentObjectGroupPython] H_element083  label="H_element : 045"  # scripted group (container) (typed FeaturePython)
  n = 14
  ref = H_element
FEATURE [App::DocumentObjectGroupPython] O_element083  label="O_element : 044"  # scripted group (container) (typed FeaturePython)
  n = 2
  ref = O_element
FEATURE [App::DocumentObjectGroupPython] G4_POLYVINYL_BUTYRAL  # scripted group (container) (typed FeaturePython)
  Dunit = g/cm3
  Dvalue = 1.12
  Group = -> [C_element091,H_element083,O_element083]
  conduct = 2
  density = 1
  expand = 3
  formula = G4_POLYVINYL_BUTYRAL
  name = G4_POLYVINYL_BUTYRAL
  specific = 4
FEATURE [App::DocumentObjectGroupPython] C_element092  label="C_element : 050"  # scripted group (container) (typed FeaturePython)
  n = 2
  ref = C_element
FEATURE [App::DocumentObjectGroupPython] H_element084  label="H_element : 046"  # scripted group (container) (typed FeaturePython)
  n = 3
  ref = H_element
FEATURE [App::DocumentObjectGroupPython] Cl_element019  label="Cl_element : 009"  # scripted group (container) (typed FeaturePython)
  n = 1
  ref = Cl_element
FEATURE [App::DocumentObjectGroupPython] G4_POLYVINYL_CHLORIDE  # scripted group (container) (typed FeaturePython)
  Dunit = g/cm3
  Dvalue = 1.3
  Group = -> [C_element092,H_element084,Cl_element019]
  conduct = 2
  density = 1
  expand = 3
  formula = G4_POLYVINYL_CHLORIDE
  name = G4_POLYVINYL_CHLORIDE
  specific = 4
FEATURE [App::DocumentObjectGroupPython] C_element093  label="C_element : 051"  # scripted group (container) (typed FeaturePython)
  n = 2
  ref = C_element
FEATURE [App::DocumentObjectGroupPython] H_element085  label="H_element : 047"  # scripted group (container) (typed FeaturePython)
  n = 2
  ref = H_element
FEATURE [App::DocumentObjectGroupPython] Cl_element020  label="Cl_element : 010"  # scripted group (container) (typed FeaturePython)
  n = 2
  ref = Cl_element
FEATURE [App::DocumentObjectGroupPython] G4_POLYVINYLIDENE_CHLORIDE  # scripted group (container) (typed FeaturePython)
  Dunit = g/cm3
  Dvalue = 1.7
  Group = -> [C_element093,H_element085,Cl_element020]
  conduct = 2
  density = 1
  expand = 3
  formula = G4_POLYVINYLIDENE_CHLORIDE
  name = G4_POLYVINYLIDENE_CHLORIDE
  specific = 4
FEATURE [App::DocumentObjectGroupPython] C_element094  label="C_element : 052"  # scripted group (container) (typed FeaturePython)
  n = 2
  ref = C_element
FEATURE [App::DocumentObjectGroupPython] H_element086  label="H_element : 048"  # scripted group (container) (typed FeaturePython)
  n = 2
  ref = H_element
FEATURE [App::DocumentObjectGroupPython] F_element016  label="F_element : 007"  # scripted group (container) (typed FeaturePython)
  n = 2
  ref = F_element
FEATURE [App::DocumentObjectGroupPython] G4_POLYVINYLIDENE_FLUORIDE  # scripted group (container) (typed FeaturePython)
  Dunit = g/cm3
  Dvalue = 1.76
  Group = -> [C_element094,H_element086,F_element016]
  conduct = 2
  density = 1
  expand = 3
  formula = G4_POLYVINYLIDENE_FLUORIDE
  name = G4_POLYVINYLIDENE_FLUORIDE
  specific = 4
FEATURE [App::DocumentObjectGroupPython] C_element095  label="C_element : 053"  # scripted group (container) (typed FeaturePython)
  n = 6
  ref = C_element
FEATURE [App::DocumentObjectGroupPython] H_element087  label="H_element : 9"  # scripted group (container) (typed FeaturePython)
  n = 9
  ref = H_element
FEATURE [App::DocumentObjectGroupPython] N_element037  label="N_element : 016"  # scripted group (container) (typed FeaturePython)
  n = 1
  ref = N_element
FEATURE [App::DocumentObjectGroupPython] O_element084  label="O_element : 045"  # scripted group (container) (typed FeaturePython)
  n = 1
  ref = O_element
FEATURE [App::DocumentObjectGroupPython] G4_POLYVINYL_PYRROLIDONE  # scripted group (container) (typed FeaturePython)
  Dunit = g/cm3
  Dvalue = 1.25
  Group = -> [C_element095,H_element087,N_element037,O_element084]
  conduct = 2
  density = 1
  expand = 3
  formula = G4_POLYVINYL_PYRROLIDONE
  name = G4_POLYVINYL_PYRROLIDONE
  specific = 4
FEATURE [App::DocumentObjectGroupPython] K_element008  label="K_element : 1"  # scripted group (container) (typed FeaturePython)
  n = 1
  ref = K_element
FEATURE [App::DocumentObjectGroupPython] I_element006  label="I_element : 003"  # scripted group (container) (typed FeaturePython)
  n = 1
  ref = I_element
FEATURE [App::DocumentObjectGroupPython] G4_POTASSIUM_IODIDE  # scripted group (container) (typed FeaturePython)
  Dunit = g/cm3
  Dvalue = 3.13
  Group = -> [K_element008,I_element006]
  conduct = 2
  density = 1
  expand = 3
  formula = G4_POTASSIUM_IODIDE
  name = G4_POTASSIUM_IODIDE
  specific = 4
FEATURE [App::DocumentObjectGroupPython] K_element009  label="K_element : 2"  # scripted group (container) (typed FeaturePython)
  n = 2
  ref = K_element
FEATURE [App::DocumentObjectGroupPython] O_element085  label="O_element : 046"  # scripted group (container) (typed FeaturePython)
  n = 1
  ref = O_element
FEATURE [App::DocumentObjectGroupPython] G4_POTASSIUM_OXIDE  # scripted group (container) (typed FeaturePython)
  Dunit = g/cm3
  Dvalue = 2.32
  Group = -> [K_element009,O_element085]
  conduct = 2
  density = 1
  expand = 3
  formula = G4_POTASSIUM_OXIDE
  name = G4_POTASSIUM_OXIDE
  specific = 4
FEATURE [App::DocumentObjectGroupPython] C_element096  label="C_element : 054"  # scripted group (container) (typed FeaturePython)
  n = 3
  ref = C_element
FEATURE [App::DocumentObjectGroupPython] H_element088  label="H_element : 049"  # scripted group (container) (typed FeaturePython)
  n = 8
  ref = H_element
FEATURE [App::DocumentObjectGroupPython] G4_PROPANE  # scripted group (container) (typed FeaturePython)
  Dunit = g/cm3
  Dvalue = 0.00187939
  Group = -> [C_element096,H_element088]
  conduct = 2
  density = 1
  expand = 3
  formula = G4_PROPANE
  name = G4_PROPANE
  specific = 4
FEATURE [App::DocumentObjectGroupPython] C_element097  label="C_element : 055"  # scripted group (container) (typed FeaturePython)
  n = 3
  ref = C_element
FEATURE [App::DocumentObjectGroupPython] H_element089  label="H_element : 050"  # scripted group (container) (typed FeaturePython)
  n = 8
  ref = H_element
FEATURE [App::DocumentObjectGroupPython] G4_lPROPANE  # scripted group (container) (typed FeaturePython)
  Dunit = g/cm3
  Dvalue = 0.43
  Group = -> [C_element097,H_element089]
  conduct = 2
  density = 1
  expand = 3
  formula = G4_lPROPANE
  name = G4_lPROPANE
  specific = 4
FEATURE [App::DocumentObjectGroupPython] C_element098  label="C_element : 056"  # scripted group (container) (typed FeaturePython)
  n = 3
  ref = C_element
FEATURE [App::DocumentObjectGroupPython] H_element090  label="H_element : 051"  # scripted group (container) (typed FeaturePython)
  n = 8
  ref = H_element
FEATURE [App::DocumentObjectGroupPython] O_element086  label="O_element : 047"  # scripted group (container) (typed FeaturePython)
  n = 1
  ref = O_element
FEATURE [App::DocumentObjectGroupPython] G4_N_PROPYL_ALCOHOL  label="G4_N-PROPYL_ALCOHOL"  # scripted group (container) (typed FeaturePython)
  Dunit = g/cm3
  Dvalue = 0.8035
  Group = -> [C_element098,H_element090,O_element086]
  conduct = 2
  density = 1
  expand = 3
  formula = G4_N-PROPYL_ALCOHOL
  name = G4_N-PROPYL_ALCOHOL
  specific = 4
FEATURE [App::DocumentObjectGroupPython] C_element099  label="C_element : 057"  # scripted group (container) (typed FeaturePython)
  n = 5
  ref = C_element
FEATURE [App::DocumentObjectGroupPython] H_element091  label="H_element : 052"  # scripted group (container) (typed FeaturePython)
  n = 5
  ref = H_element
FEATURE [App::DocumentObjectGroupPython] N_element038  label="N_element : 017"  # scripted group (container) (typed FeaturePython)
  n = 1
  ref = N_element
FEATURE [App::DocumentObjectGroupPython] G4_PYRIDINE  # scripted group (container) (typed FeaturePython)
  Dunit = g/cm3
  Dvalue = 0.9819
  Group = -> [C_element099,H_element091,N_element038]
  conduct = 2
  density = 1
  expand = 3
  formula = G4_PYRIDINE
  name = G4_PYRIDINE
  specific = 4
FEATURE [App::DocumentObjectGroupPython] H_element092  label="H_element : 0.144"  # scripted group (container) (typed FeaturePython)
  n = 0.143711
FEATURE [App::DocumentObjectGroupPython] C_element100  label="C_element : 0.856"  # scripted group (container) (typed FeaturePython)
  n = 0.856289
FEATURE [App::DocumentObjectGroupPython] G4_RUBBER_BUTYL  # scripted group (container) (typed FeaturePython)
  Dunit = g/cm3
  Dvalue = 0.92
  Group = -> [H_element092,C_element100]
  conduct = 2
  density = 1
  expand = 3
  formula = G4_RUBBER_BUTYL
  name = G4_RUBBER_BUTYL
  specific = 4
FEATURE [App::DocumentObjectGroupPython] H_element093  label="H_element : 0.118"  # scripted group (container) (typed FeaturePython)
  n = 0.118371
FEATURE [App::DocumentObjectGroupPython] C_element101  label="C_element : 0.882"  # scripted group (container) (typed FeaturePython)
  n = 0.881629
FEATURE [App::DocumentObjectGroupPython] G4_RUBBER_NATURAL  # scripted group (container) (typed FeaturePython)
  Dunit = g/cm3
  Dvalue = 0.92
  Group = -> [H_element093,C_element101]
  conduct = 2
  density = 1
  expand = 3
  formula = G4_RUBBER_NATURAL
  name = G4_RUBBER_NATURAL
  specific = 4
FEATURE [App::DocumentObjectGroupPython] H_element094  label="H_element : 0.145"  # scripted group (container) (typed FeaturePython)
  n = 0.05692
FEATURE [App::DocumentObjectGroupPython] C_element102  label="C_element : 0.543"  # scripted group (container) (typed FeaturePython)
  n = 0.542646
FEATURE [App::DocumentObjectGroupPython] Cl_element021  label="Cl_element : 0.400"  # scripted group (container) (typed FeaturePython)
  n = 0.400434
FEATURE [App::DocumentObjectGroupPython] G4_RUBBER_NEOPRENE  # scripted group (container) (typed FeaturePython)
  Dunit = g/cm3
  Dvalue = 1.23
  Group = -> [H_element094,C_element102,Cl_element021]
  conduct = 2
  density = 1
  expand = 3
  formula = G4_RUBBER_NEOPRENE
  name = G4_RUBBER_NEOPRENE
  specific = 4
FEATURE [App::DocumentObjectGroupPython] Si_element006  label="Si_element : 1"  # scripted group (container) (typed FeaturePython)
  n = 1
  ref = Si_element
FEATURE [App::DocumentObjectGroupPython] O_element087  label="O_element : 048"  # scripted group (container) (typed FeaturePython)
  n = 2
  ref = O_element
FEATURE [App::DocumentObjectGroupPython] G4_SILICON_DIOXIDE  # scripted group (container) (typed FeaturePython)
  Dunit = g/cm3
  Dvalue = 2.32
  Group = -> [Si_element006,O_element087]
  conduct = 2
  density = 1
  expand = 3
  formula = G4_SILICON_DIOXIDE
  name = G4_SILICON_DIOXIDE
  specific = 4
FEATURE [App::DocumentObjectGroupPython] Ag_element002  label="Ag_element : 1"  # scripted group (container) (typed FeaturePython)
  n = 1
  ref = Ag_element
FEATURE [App::DocumentObjectGroupPython] Br_element005  label="Br_element : 003"  # scripted group (container) (typed FeaturePython)
  n = 1
  ref = Br_element
FEATURE [App::DocumentObjectGroupPython] G4_SILVER_BROMIDE  # scripted group (container) (typed FeaturePython)
  Dunit = g/cm3
  Dvalue = 6.473
  Group = -> [Ag_element002,Br_element005]
  conduct = 2
  density = 1
  expand = 3
  formula = G4_SILVER_BROMIDE
  name = G4_SILVER_BROMIDE
  specific = 4
FEATURE [App::DocumentObjectGroupPython] Ag_element003  label="Ag_element : 002"  # scripted group (container) (typed FeaturePython)
  n = 1
  ref = Ag_element
FEATURE [App::DocumentObjectGroupPython] Cl_element022  label="Cl_element : 011"  # scripted group (container) (typed FeaturePython)
  n = 1
  ref = Cl_element
FEATURE [App::DocumentObjectGroupPython] G4_SILVER_CHLORIDE  # scripted group (container) (typed FeaturePython)
  Dunit = g/cm3
  Dvalue = 5.56
  Group = -> [Ag_element003,Cl_element022]
  conduct = 2
  density = 1
  expand = 3
  formula = G4_SILVER_CHLORIDE
  name = G4_SILVER_CHLORIDE
  specific = 4
FEATURE [App::DocumentObjectGroupPython] Br_element006  label="Br_element : 0.423"  # scripted group (container) (typed FeaturePython)
  n = 0.422895
FEATURE [App::DocumentObjectGroupPython] Ag_element004  label="Ag_element : 0.574"  # scripted group (container) (typed FeaturePython)
  n = 0.573748
FEATURE [App::DocumentObjectGroupPython] I_element007  label="I_element : 0.649"  # scripted group (container) (typed FeaturePython)
  n = 0.003357
FEATURE [App::DocumentObjectGroupPython] G4_SILVER_HALIDES  # scripted group (container) (typed FeaturePython)
  Dunit = g/cm3
  Dvalue = 6.47
  Group = -> [Br_element006,Ag_element004,I_element007]
  conduct = 2
  density = 1
  expand = 3
  formula = G4_SILVER_HALIDES
  name = G4_SILVER_HALIDES
  specific = 4
FEATURE [App::DocumentObjectGroupPython] Ag_element005  label="Ag_element : 003"  # scripted group (container) (typed FeaturePython)
  n = 1
  ref = Ag_element
FEATURE [App::DocumentObjectGroupPython] I_element008  label="I_element : 004"  # scripted group (container) (typed FeaturePython)
  n = 1
  ref = I_element
FEATURE [App::DocumentObjectGroupPython] G4_SILVER_IODIDE  # scripted group (container) (typed FeaturePython)
  Dunit = g/cm3
  Dvalue = 6.01
  Group = -> [Ag_element005,I_element008]
  conduct = 2
  density = 1
  expand = 3
  formula = G4_SILVER_IODIDE
  name = G4_SILVER_IODIDE
  specific = 4
FEATURE [App::DocumentObjectGroupPython] H_element095  label="H_element : 0.100"  # scripted group (container) (typed FeaturePython)
  n = 0.1
FEATURE [App::DocumentObjectGroupPython] C_element103  label="C_element : 0.204"  # scripted group (container) (typed FeaturePython)
  n = 0.204
FEATURE [App::DocumentObjectGroupPython] N_element039  label="N_element : 0.759"  # scripted group (container) (typed FeaturePython)
  n = 0.042
FEATURE [App::DocumentObjectGroupPython] O_element088  label="O_element : 0.645"  # scripted group (container) (typed FeaturePython)
  n = 0.645
FEATURE [App::DocumentObjectGroupPython] Na_element013  label="Na_element : 0.100"  # scripted group (container) (typed FeaturePython)
  n = 0.002
FEATURE [App::DocumentObjectGroupPython] P_element009  label="P_element : 0.107"  # scripted group (container) (typed FeaturePython)
  n = 0.001
FEATURE [App::DocumentObjectGroupPython] S_element020  label="S_element : 0.021"  # scripted group (container) (typed FeaturePython)
  n = 0.002
FEATURE [App::DocumentObjectGroupPython] Cl_element023  label="Cl_element : 0.590"  # scripted group (container) (typed FeaturePython)
  n = 0.003
FEATURE [App::DocumentObjectGroupPython] K_element010  label="K_element : 0.001"  # scripted group (container) (typed FeaturePython)
  n = 0.001
FEATURE [App::DocumentObjectGroupPython] G4_SKIN_ICRP  # scripted group (container) (typed FeaturePython)
  Dunit = g/cm3
  Dvalue = 1.09
  Group = -> [H_element095,C_element103,N_element039,O_element088,Na_element013,P_element009,S_element020,Cl_element023,K_element010]
  conduct = 2
  density = 1
  expand = 3
  formula = G4_SKIN_ICRP
  name = G4_SKIN_ICRP
  specific = 4
FEATURE [App::DocumentObjectGroupPython] Na_element014  label="Na_element : 2"  # scripted group (container) (typed FeaturePython)
  n = 2
  ref = Na_element
FEATURE [App::DocumentObjectGroupPython] C_element104  label="C_element : 058"  # scripted group (container) (typed FeaturePython)
  n = 1
  ref = C_element
FEATURE [App::DocumentObjectGroupPython] O_element089  label="O_element : 049"  # scripted group (container) (typed FeaturePython)
  n = 3
  ref = O_element
FEATURE [App::DocumentObjectGroupPython] G4_SODIUM_CARBONATE  # scripted group (container) (typed FeaturePython)
  Dunit = g/cm3
  Dvalue = 2.532
  Group = -> [Na_element014,C_element104,O_element089]
  conduct = 2
  density = 1
  expand = 3
  formula = G4_SODIUM_CARBONATE
  name = G4_SODIUM_CARBONATE
  specific = 4
FEATURE [App::DocumentObjectGroupPython] Na_element015  label="Na_element : 1"  # scripted group (container) (typed FeaturePython)
  n = 1
  ref = Na_element
FEATURE [App::DocumentObjectGroupPython] I_element009  label="I_element : 005"  # scripted group (container) (typed FeaturePython)
  n = 1
  ref = I_element
FEATURE [App::DocumentObjectGroupPython] G4_SODIUM_IODIDE  # scripted group (container) (typed FeaturePython)
  Dunit = g/cm3
  Dvalue = 3.667
  Group = -> [Na_element015,I_element009]
  conduct = 2
  density = 1
  expand = 3
  formula = G4_SODIUM_IODIDE
  name = G4_SODIUM_IODIDE
  specific = 4
FEATURE [App::DocumentObjectGroupPython] Na_element016  label="Na_element : 003"  # scripted group (container) (typed FeaturePython)
  n = 2
  ref = Na_element
FEATURE [App::DocumentObjectGroupPython] O_element090  label="O_element : 050"  # scripted group (container) (typed FeaturePython)
  n = 1
  ref = O_element
FEATURE [App::DocumentObjectGroupPython] G4_SODIUM_MONOXIDE  # scripted group (container) (typed FeaturePython)
  Dunit = g/cm3
  Dvalue = 2.27
  Group = -> [Na_element016,O_element090]
  conduct = 2
  density = 1
  expand = 3
  formula = G4_SODIUM_MONOXIDE
  name = G4_SODIUM_MONOXIDE
  specific = 4
FEATURE [App::DocumentObjectGroupPython] Na_element017  label="Na_element : 004"  # scripted group (container) (typed FeaturePython)
  n = 1
  ref = Na_element
FEATURE [App::DocumentObjectGroupPython] N_element040  label="N_element : 018"  # scripted group (container) (typed FeaturePython)
  n = 1
  ref = N_element
FEATURE [App::DocumentObjectGroupPython] O_element091  label="O_element : 051"  # scripted group (container) (typed FeaturePython)
  n = 3
  ref = O_element
FEATURE [App::DocumentObjectGroupPython] G4_SODIUM_NITRATE  # scripted group (container) (typed FeaturePython)
  Dunit = g/cm3
  Dvalue = 2.261
  Group = -> [Na_element017,N_element040,O_element091]
  conduct = 2
  density = 1
  expand = 3
  formula = G4_SODIUM_NITRATE
  name = G4_SODIUM_NITRATE
  specific = 4
FEATURE [App::DocumentObjectGroupPython] C_element105  label="C_element : 059"  # scripted group (container) (typed FeaturePython)
  n = 14
  ref = C_element
FEATURE [App::DocumentObjectGroupPython] H_element096  label="H_element : 053"  # scripted group (container) (typed FeaturePython)
  n = 12
  ref = H_element
FEATURE [App::DocumentObjectGroupPython] G4_STILBENE  # scripted group (container) (typed FeaturePython)
  Dunit = g/cm3
  Dvalue = 0.9707
  Group = -> [C_element105,H_element096]
  conduct = 2
  density = 1
  expand = 3
  formula = G4_STILBENE
  name = G4_STILBENE
  specific = 4
FEATURE [App::DocumentObjectGroupPython] C_element106  label="C_element : 12"  # scripted group (container) (typed FeaturePython)
  n = 12
  ref = C_element
FEATURE [App::DocumentObjectGroupPython] H_element097  label="H_element : 22"  # scripted group (container) (typed FeaturePython)
  n = 22
  ref = H_element
FEATURE [App::DocumentObjectGroupPython] O_element092  label="O_element : 11"  # scripted group (container) (typed FeaturePython)
  n = 11
  ref = O_element
FEATURE [App::DocumentObjectGroupPython] G4_SUCROSE  # scripted group (container) (typed FeaturePython)
  Dunit = g/cm3
  Dvalue = 1.5805
  Group = -> [C_element106,H_element097,O_element092]
  conduct = 2
  density = 1
  expand = 3
  formula = G4_SUCROSE
  name = G4_SUCROSE
  specific = 4
FEATURE [App::DocumentObjectGroupPython] C_element107  label="C_element : 18"  # scripted group (container) (typed FeaturePython)
  n = 18
  ref = C_element
FEATURE [App::DocumentObjectGroupPython] H_element098  label="H_element : 054"  # scripted group (container) (typed FeaturePython)
  n = 14
  ref = H_element
FEATURE [App::DocumentObjectGroupPython] G4_TERPHENYL  # scripted group (container) (typed FeaturePython)
  Dunit = g/cm3
  Dvalue = 1.24
  Group = -> [C_element107,H_element098]
  conduct = 2
  density = 1
  expand = 3
  formula = G4_TERPHENYL
  name = G4_TERPHENYL
  specific = 4
FEATURE [App::DocumentObjectGroupPython] H_element099  label="H_element : 0.146"  # scripted group (container) (typed FeaturePython)
  n = 0.106
FEATURE [App::DocumentObjectGroupPython] C_element108  label="C_element : 0.883"  # scripted group (container) (typed FeaturePython)
  n = 0.099
FEATURE [App::DocumentObjectGroupPython] N_element041  label="N_element : 0.020"  # scripted group (container) (typed FeaturePython)
  n = 0.02
FEATURE [App::DocumentObjectGroupPython] O_element093  label="O_element : 0.766"  # scripted group (container) (typed FeaturePython)
  n = 0.766
FEATURE [App::DocumentObjectGroupPython] Na_element018  label="Na_element : 0.101"  # scripted group (container) (typed FeaturePython)
  n = 0.002
FEATURE [App::DocumentObjectGroupPython] P_element010  label="P_element : 0.108"  # scripted group (container) (typed FeaturePython)
  n = 0.001
FEATURE [App::DocumentObjectGroupPython] S_element021  label="S_element : 0.022"  # scripted group (container) (typed FeaturePython)
  n = 0.002
FEATURE [App::DocumentObjectGroupPython] Cl_element024  label="Cl_element : 0.002"  # scripted group (container) (typed FeaturePython)
  n = 0.002
FEATURE [App::DocumentObjectGroupPython] K_element011  label="K_element : 0.017"  # scripted group (container) (typed FeaturePython)
  n = 0.002
FEATURE [App::DocumentObjectGroupPython] G4_TESTIS_ICRP  # scripted group (container) (typed FeaturePython)
  Dunit = g/cm3
  Dvalue = 1.04
  Group = -> [H_element099,C_element108,N_element041,O_element093,Na_element018,P_element010,S_element021,Cl_element024,K_element011]
  conduct = 2
  density = 1
  expand = 3
  formula = G4_TESTIS_ICRP
  name = G4_TESTIS_ICRP
  specific = 4
FEATURE [App::DocumentObjectGroupPython] C_element109  label="C_element : 060"  # scripted group (container) (typed FeaturePython)
  n = 2
  ref = C_element
FEATURE [App::DocumentObjectGroupPython] Cl_element025  label="Cl_element : 012"  # scripted group (container) (typed FeaturePython)
  n = 4
  ref = Cl_element
FEATURE [App::DocumentObjectGroupPython] G4_TETRACHLOROETHYLENE  # scripted group (container) (typed FeaturePython)
  Dunit = g/cm3
  Dvalue = 1.625
  Group = -> [C_element109,Cl_element025]
  conduct = 2
  density = 1
  expand = 3
  formula = G4_TETRACHLOROETHYLENE
  name = G4_TETRACHLOROETHYLENE
  specific = 4
FEATURE [App::DocumentObjectGroupPython] Tl_element001  label="Tl_element : 1"  # scripted group (container) (typed FeaturePython)
  n = 1
  ref = Tl_element
FEATURE [App::DocumentObjectGroupPython] Cl_element026  label="Cl_element : 013"  # scripted group (container) (typed FeaturePython)
  n = 1
  ref = Cl_element
FEATURE [App::DocumentObjectGroupPython] G4_THALLIUM_CHLORIDE  # scripted group (container) (typed FeaturePython)
  Dunit = g/cm3
  Dvalue = 7.004
  Group = -> [Tl_element001,Cl_element026]
  conduct = 2
  density = 1
  expand = 3
  formula = G4_THALLIUM_CHLORIDE
  name = G4_THALLIUM_CHLORIDE
  specific = 4
FEATURE [App::DocumentObjectGroupPython] H_element100  label="H_element : 0.147"  # scripted group (container) (typed FeaturePython)
  n = 0.105
FEATURE [App::DocumentObjectGroupPython] C_element110  label="C_element : 0.256"  # scripted group (container) (typed FeaturePython)
  n = 0.256
FEATURE [App::DocumentObjectGroupPython] N_element042  label="N_element : 0.760"  # scripted group (container) (typed FeaturePython)
  n = 0.027
FEATURE [App::DocumentObjectGroupPython] O_element094  label="O_element : 0.602"  # scripted group (container) (typed FeaturePython)
  n = 0.602
FEATURE [App::DocumentObjectGroupPython] Na_element019  label="Na_element : 0.102"  # scripted group (container) (typed FeaturePython)
  n = 0.001
FEATURE [App::DocumentObjectGroupPython] P_element011  label="P_element : 0.109"  # scripted group (container) (typed FeaturePython)
  n = 0.002
FEATURE [App::DocumentObjectGroupPython] S_element022  label="S_element : 0.023"  # scripted group (container) (typed FeaturePython)
  n = 0.003
FEATURE [App::DocumentObjectGroupPython] Cl_element027  label="Cl_element : 0.591"  # scripted group (container) (typed FeaturePython)
  n = 0.002
FEATURE [App::DocumentObjectGroupPython] K_element012  label="K_element : 0.018"  # scripted group (container) (typed FeaturePython)
  n = 0.002
FEATURE [App::DocumentObjectGroupPython] G4_TISSUE_SOFT_ICRP  # scripted group (container) (typed FeaturePython)
  Dunit = g/cm3
  Dvalue = 1.03
  Group = -> [H_element100,C_element110,N_element042,O_element094,Na_element019,P_element011,S_element022,Cl_element027,K_element012]
  conduct = 2
  density = 1
  expand = 3
  formula = G4_TISSUE_SOFT_ICRP
  name = G4_TISSUE_SOFT_ICRP
  specific = 4
FEATURE [App::DocumentObjectGroupPython] H_element101  label="H_element : 0.148"  # scripted group (container) (typed FeaturePython)
  n = 0.101
FEATURE [App::DocumentObjectGroupPython] C_element111  label="C_element : 0.111"  # scripted group (container) (typed FeaturePython)
  n = 0.111
FEATURE [App::DocumentObjectGroupPython] N_element043  label="N_element : 0.026"  # scripted group (container) (typed FeaturePython)
  n = 0.026
FEATURE [App::DocumentObjectGroupPython] O_element095  label="O_element : 0.762"  # scripted group (container) (typed FeaturePython)
  n = 0.762
FEATURE [App::DocumentObjectGroupPython] G4_TISSUE_SOFT_ICRU_4  label="G4_TISSUE_SOFT_ICRU-4"  # scripted group (container) (typed FeaturePython)
  Dunit = g/cm3
  Dvalue = 1
  Group = -> [H_element101,C_element111,N_element043,O_element095]
  conduct = 2
  density = 1
  expand = 3
  formula = G4_TISSUE_SOFT_ICRU-4
  name = G4_TISSUE_SOFT_ICRU-4
  specific = 4
FEATURE [App::DocumentObjectGroupPython] H_element102  label="H_element : 0.149"  # scripted group (container) (typed FeaturePython)
  n = 0.101869
FEATURE [App::DocumentObjectGroupPython] C_element112  label="C_element : 0.456"  # scripted group (container) (typed FeaturePython)
  n = 0.456179
FEATURE [App::DocumentObjectGroupPython] N_element044  label="N_element : 0.761"  # scripted group (container) (typed FeaturePython)
  n = 0.035172
FEATURE [App::DocumentObjectGroupPython] O_element096  label="O_element : 0.407"  # scripted group (container) (typed FeaturePython)
  n = 0.40678
FEATURE [App::DocumentObjectGroupPython] G4_TISSUE_METHANE  label="G4_TISSUE-METHANE"  # scripted group (container) (typed FeaturePython)
  Dunit = g/cm3
  Dvalue = 0.00106409
  Group = -> [H_element102,C_element112,N_element044,O_element096]
  conduct = 2
  density = 1
  expand = 3
  formula = G4_TISSUE-METHANE
  name = G4_TISSUE-METHANE
  specific = 4
FEATURE [App::DocumentObjectGroupPython] H_element103  label="H_element : 0.103"  # scripted group (container) (typed FeaturePython)
  n = 0.102672
FEATURE [App::DocumentObjectGroupPython] C_element113  label="C_element : 0.569"  # scripted group (container) (typed FeaturePython)
  n = 0.56894
FEATURE [App::DocumentObjectGroupPython] N_element045  label="N_element : 0.762"  # scripted group (container) (typed FeaturePython)
  n = 0.035022
FEATURE [App::DocumentObjectGroupPython] O_element097  label="O_element : 0.293"  # scripted group (container) (typed FeaturePython)
  n = 0.293366
FEATURE [App::DocumentObjectGroupPython] G4_TISSUE_PROPANE  label="G4_TISSUE-PROPANE"  # scripted group (container) (typed FeaturePython)
  Dunit = g/cm3
  Dvalue = 0.00182628
  Group = -> [H_element103,C_element113,N_element045,O_element097]
  conduct = 2
  density = 1
  expand = 3
  formula = G4_TISSUE-PROPANE
  name = G4_TISSUE-PROPANE
  specific = 4
FEATURE [App::DocumentObjectGroupPython] Ti_element003  label="Ti_element : 1"  # scripted group (container) (typed FeaturePython)
  n = 1
  ref = Ti_element
FEATURE [App::DocumentObjectGroupPython] O_element098  label="O_element : 052"  # scripted group (container) (typed FeaturePython)
  n = 2
  ref = O_element
FEATURE [App::DocumentObjectGroupPython] G4_TITANIUM_DIOXIDE  # scripted group (container) (typed FeaturePython)
  Dunit = g/cm3
  Dvalue = 4.26
  Group = -> [Ti_element003,O_element098]
  conduct = 2
  density = 1
  expand = 3
  formula = G4_TITANIUM_DIOXIDE
  name = G4_TITANIUM_DIOXIDE
  specific = 4
FEATURE [App::DocumentObjectGroupPython] C_element114  label="C_element : 061"  # scripted group (container) (typed FeaturePython)
  n = 7
  ref = C_element
FEATURE [App::DocumentObjectGroupPython] H_element104  label="H_element : 055"  # scripted group (container) (typed FeaturePython)
  n = 8
  ref = H_element
FEATURE [App::DocumentObjectGroupPython] G4_TOLUENE  # scripted group (container) (typed FeaturePython)
  Dunit = g/cm3
  Dvalue = 0.8669
  Group = -> [C_element114,H_element104]
  conduct = 2
  density = 1
  expand = 3
  formula = G4_TOLUENE
  name = G4_TOLUENE
  specific = 4
FEATURE [App::DocumentObjectGroupPython] C_element115  label="C_element : 062"  # scripted group (container) (typed FeaturePython)
  n = 2
  ref = C_element
FEATURE [App::DocumentObjectGroupPython] H_element105  label="H_element : 056"  # scripted group (container) (typed FeaturePython)
  n = 1
  ref = H_element
FEATURE [App::DocumentObjectGroupPython] Cl_element028  label="Cl_element : 014"  # scripted group (container) (typed FeaturePython)
  n = 3
  ref = Cl_element
FEATURE [App::DocumentObjectGroupPython] G4_TRICHLOROETHYLENE  # scripted group (container) (typed FeaturePython)
  Dunit = g/cm3
  Dvalue = 1.46
  Group = -> [C_element115,H_element105,Cl_element028]
  conduct = 2
  density = 1
  expand = 3
  formula = G4_TRICHLOROETHYLENE
  name = G4_TRICHLOROETHYLENE
  specific = 4
FEATURE [App::DocumentObjectGroupPython] C_element116  label="C_element : 063"  # scripted group (container) (typed FeaturePython)
  n = 6
  ref = C_element
FEATURE [App::DocumentObjectGroupPython] H_element106  label="H_element : 15"  # scripted group (container) (typed FeaturePython)
  n = 15
  ref = H_element
FEATURE [App::DocumentObjectGroupPython] O_element099  label="O_element : 053"  # scripted group (container) (typed FeaturePython)
  n = 4
  ref = O_element
FEATURE [App::DocumentObjectGroupPython] P_element012  label="P_element : 1"  # scripted group (container) (typed FeaturePython)
  n = 1
  ref = P_element
FEATURE [App::DocumentObjectGroupPython] G4_TRIETHYL_PHOSPHATE  # scripted group (container) (typed FeaturePython)
  Dunit = g/cm3
  Dvalue = 1.07
  Group = -> [C_element116,H_element106,O_element099,P_element012]
  conduct = 2
  density = 1
  expand = 3
  formula = G4_TRIETHYL_PHOSPHATE
  name = G4_TRIETHYL_PHOSPHATE
  specific = 4
FEATURE [App::DocumentObjectGroupPython] W_element003  label="W_element : 003"  # scripted group (container) (typed FeaturePython)
  n = 1
  ref = W_element
FEATURE [App::DocumentObjectGroupPython] F_element017  label="F_element : 6"  # scripted group (container) (typed FeaturePython)
  n = 6
  ref = F_element
FEATURE [App::DocumentObjectGroupPython] G4_TUNGSTEN_HEXAFLUORIDE  # scripted group (container) (typed FeaturePython)
  Dunit = g/cm3
  Dvalue = 2.4
  Group = -> [W_element003,F_element017]
  conduct = 2
  density = 1
  expand = 3
  formula = G4_TUNGSTEN_HEXAFLUORIDE
  name = G4_TUNGSTEN_HEXAFLUORIDE
  specific = 4
FEATURE [App::DocumentObjectGroupPython] U_element001  label="U_element : 1"  # scripted group (container) (typed FeaturePython)
  n = 1
  ref = U_element
FEATURE [App::DocumentObjectGroupPython] C_element117  label="C_element : 064"  # scripted group (container) (typed FeaturePython)
  n = 2
  ref = C_element
FEATURE [App::DocumentObjectGroupPython] G4_URANIUM_DICARBIDE  # scripted group (container) (typed FeaturePython)
  Dunit = g/cm3
  Dvalue = 11.28
  Group = -> [U_element001,C_element117]
  conduct = 2
  density = 1
  expand = 3
  formula = G4_URANIUM_DICARBIDE
  name = G4_URANIUM_DICARBIDE
  specific = 4
FEATURE [App::DocumentObjectGroupPython] U_element002  label="U_element : 002"  # scripted group (container) (typed FeaturePython)
  n = 1
  ref = U_element
FEATURE [App::DocumentObjectGroupPython] C_element118  label="C_element : 065"  # scripted group (container) (typed FeaturePython)
  n = 1
  ref = C_element
FEATURE [App::DocumentObjectGroupPython] G4_URANIUM_MONOCARBIDE  # scripted group (container) (typed FeaturePython)
  Dunit = g/cm3
  Dvalue = 13.63
  Group = -> [U_element002,C_element118]
  conduct = 2
  density = 1
  expand = 3
  formula = G4_URANIUM_MONOCARBIDE
  name = G4_URANIUM_MONOCARBIDE
  specific = 4
FEATURE [App::DocumentObjectGroupPython] U_element003  label="U_element : 003"  # scripted group (container) (typed FeaturePython)
  n = 1
  ref = U_element
FEATURE [App::DocumentObjectGroupPython] O_element100  label="O_element : 054"  # scripted group (container) (typed FeaturePython)
  n = 2
  ref = O_element
FEATURE [App::DocumentObjectGroupPython] G4_URANIUM_OXIDE  # scripted group (container) (typed FeaturePython)
  Dunit = g/cm3
  Dvalue = 10.96
  Group = -> [U_element003,O_element100]
  conduct = 2
  density = 1
  expand = 3
  formula = G4_URANIUM_OXIDE
  name = G4_URANIUM_OXIDE
  specific = 4
FEATURE [App::DocumentObjectGroupPython] C_element119  label="C_element : 066"  # scripted group (container) (typed FeaturePython)
  n = 1
  ref = C_element
FEATURE [App::DocumentObjectGroupPython] H_element107  label="H_element : 057"  # scripted group (container) (typed FeaturePython)
  n = 4
  ref = H_element
FEATURE [App::DocumentObjectGroupPython] N_element046  label="N_element : 019"  # scripted group (container) (typed FeaturePython)
  n = 2
  ref = N_element
FEATURE [App::DocumentObjectGroupPython] O_element101  label="O_element : 055"  # scripted group (container) (typed FeaturePython)
  n = 1
  ref = O_element
FEATURE [App::DocumentObjectGroupPython] G4_UREA  # scripted group (container) (typed FeaturePython)
  Dunit = g/cm3
  Dvalue = 1.323
  Group = -> [C_element119,H_element107,N_element046,O_element101]
  conduct = 2
  density = 1
  expand = 3
  formula = G4_UREA
  name = G4_UREA
  specific = 4
FEATURE [App::DocumentObjectGroupPython] C_element120  label="C_element : 067"  # scripted group (container) (typed FeaturePython)
  n = 5
  ref = C_element
FEATURE [App::DocumentObjectGroupPython] H_element108  label="H_element : 058"  # scripted group (container) (typed FeaturePython)
  n = 11
  ref = H_element
FEATURE [App::DocumentObjectGroupPython] N_element047  label="N_element : 020"  # scripted group (container) (typed FeaturePython)
  n = 1
  ref = N_element
FEATURE [App::DocumentObjectGroupPython] O_element102  label="O_element : 056"  # scripted group (container) (typed FeaturePython)
  n = 2
  ref = O_element
FEATURE [App::DocumentObjectGroupPython] G4_VALINE  # scripted group (container) (typed FeaturePython)
  Dunit = g/cm3
  Dvalue = 1.23
  Group = -> [C_element120,H_element108,N_element047,O_element102]
  conduct = 2
  density = 1
  expand = 3
  formula = G4_VALINE
  name = G4_VALINE
  specific = 4
FEATURE [App::DocumentObjectGroupPython] H_element109  label="H_element : 0.009"  # scripted group (container) (typed FeaturePython)
  n = 0.009417
FEATURE [App::DocumentObjectGroupPython] C_element121  label="C_element : 0.281"  # scripted group (container) (typed FeaturePython)
  n = 0.280555
FEATURE [App::DocumentObjectGroupPython] F_element018  label="F_element : 0.710"  # scripted group (container) (typed FeaturePython)
  n = 0.710028
FEATURE [App::DocumentObjectGroupPython] G4_VITON  # scripted group (container) (typed FeaturePython)
  Dunit = g/cm3
  Dvalue = 1.8
  Group = -> [H_element109,C_element121,F_element018]
  conduct = 2
  density = 1
  expand = 3
  formula = G4_VITON
  name = G4_VITON
  specific = 4
FEATURE [App::DocumentObjectGroupPython] H_element110  label="H_element : 059"  # scripted group (container) (typed FeaturePython)
  n = 2
  ref = H_element
FEATURE [App::DocumentObjectGroupPython] O_element103  label="O_element : 057"  # scripted group (container) (typed FeaturePython)
  n = 1
  ref = O_element
FEATURE [App::DocumentObjectGroupPython] G4_WATER  # scripted group (container) (typed FeaturePython)
  Dunit = g/cm3
  Dvalue = 1
  Group = -> [H_element110,O_element103]
  conduct = 2
  density = 1
  expand = 3
  formula = G4_WATER
  name = G4_WATER
  specific = 4
FEATURE [App::DocumentObjectGroupPython] H_element111  label="H_element : 060"  # scripted group (container) (typed FeaturePython)
  n = 2
  ref = H_element
FEATURE [App::DocumentObjectGroupPython] O_element104  label="O_element : 058"  # scripted group (container) (typed FeaturePython)
  n = 1
  ref = O_element
FEATURE [App::DocumentObjectGroupPython] G4_WATER_VAPOR  # scripted group (container) (typed FeaturePython)
  Dunit = g/cm3
  Dvalue = 0.000756182
  Group = -> [H_element111,O_element104]
  conduct = 2
  density = 1
  expand = 3
  formula = G4_WATER_VAPOR
  name = G4_WATER_VAPOR
  specific = 4
FEATURE [App::DocumentObjectGroupPython] C_element122  label="C_element : 068"  # scripted group (container) (typed FeaturePython)
  n = 8
  ref = C_element
FEATURE [App::DocumentObjectGroupPython] H_element112  label="H_element : 061"  # scripted group (container) (typed FeaturePython)
  n = 10
  ref = H_element
FEATURE [App::DocumentObjectGroupPython] G4_XYLENE  # scripted group (container) (typed FeaturePython)
  Dunit = g/cm3
  Dvalue = 0.87
  Group = -> [C_element122,H_element112]
  conduct = 2
  density = 1
  expand = 3
  formula = G4_XYLENE
  name = G4_XYLENE
  specific = 4
FEATURE [App::DocumentObjectGroupPython] C_element123  label="C_element : 069"  # scripted group (container) (typed FeaturePython)
  n = 1
  ref = C_element
FEATURE [App::DocumentObjectGroupPython] G4_GRAPHITE  # scripted group (container) (typed FeaturePython)
  Dunit = g/cm3
  Dvalue = 2.21
  Group = -> [C_element123]
  conduct = 2
  density = 1
  expand = 3
  formula = G4_GRAPHITE
  name = G4_GRAPHITE
  specific = 4
FEATURE [App::DocumentObjectGroupPython] NIST  # scripted group (container) (typed FeaturePython)
  Group = -> [G4_A_150_TISSUE,G4_ACETONE,G4_ACETYLENE,G4_ADENINE,G4_ADIPOSE_TISSUE_ICRP,G4_AIR,G4_ALANINE,G4_ALUMINUM_OXIDE,G4_AMBER,G4_AMMONIA,G4_ANILINE,G4_ANTHRACENE,G4_B_100_BONE,G4_BAKELITE,G4_BARIUM_FLUORIDE,G4_BARIUM_SULFATE,G4_BENZENE,G4_BERYLLIUM_OXIDE,G4_BGO,G4_BLOOD_ICRP,G4_BONE_COMPACT_ICRU,G4_BONE_CORTICAL_ICRP,G4_BORON_CARBIDE,G4_BORON_OXIDE,G4_BRAIN_ICRP,G4_BUTANE,G4_N_BUTYL_ALCOHOL,G4_C_552,+152 more]
FEATURE [App::DocumentObjectGroupPython] H_element113  label="H_element : 062"  # scripted group (container) (typed FeaturePython)
  n = 1
  ref = H_element
FEATURE [App::DocumentObjectGroupPython] G4_H  # scripted group (container) (typed FeaturePython)
  Dunit = g/cm3
  Dvalue = 8.3748e-05
  Group = -> [H_element113]
  conduct = 2
  density = 1
  expand = 3
  formula = H
  name = G4_H
  specific = 4
FEATURE [App::DocumentObjectGroupPython] He_element001  label="He_element : 1"  # scripted group (container) (typed FeaturePython)
  n = 1
  ref = He_element
FEATURE [App::DocumentObjectGroupPython] G4_He  # scripted group (container) (typed FeaturePython)
  Dunit = g/cm3
  Dvalue = 0.000166322
  Group = -> [He_element001]
  conduct = 2
  density = 1
  expand = 3
  formula = He
  name = G4_He
  specific = 4
FEATURE [App::DocumentObjectGroupPython] Li_element008  label="Li_element : 008"  # scripted group (container) (typed FeaturePython)
  n = 1
  ref = Li_element
FEATURE [App::DocumentObjectGroupPython] G4_Li  # scripted group (container) (typed FeaturePython)
  Dunit = g/cm3
  Dvalue = 0.534
  Group = -> [Li_element008]
  conduct = 2
  density = 1
  expand = 3
  formula = Li
  name = G4_Li
  specific = 4
FEATURE [App::DocumentObjectGroupPython] Be_element002  label="Be_element : 002"  # scripted group (container) (typed FeaturePython)
  n = 1
  ref = Be_element
FEATURE [App::DocumentObjectGroupPython] G4_Be  # scripted group (container) (typed FeaturePython)
  Dunit = g/cm3
  Dvalue = 1.848
  Group = -> [Be_element002]
  conduct = 2
  density = 1
  expand = 3
  formula = Be
  name = G4_Be
  specific = 4
FEATURE [App::DocumentObjectGroupPython] B_element007  label="B_element : 007"  # scripted group (container) (typed FeaturePython)
  n = 1
  ref = B_element
FEATURE [App::DocumentObjectGroupPython] G4_B  # scripted group (container) (typed FeaturePython)
  Dunit = g/cm3
  Dvalue = 2.37
  Group = -> [B_element007]
  conduct = 2
  density = 1
  expand = 3
  formula = B
  name = G4_B
  specific = 4
FEATURE [App::DocumentObjectGroupPython] C_element124  label="C_element : 070"  # scripted group (container) (typed FeaturePython)
  n = 1
  ref = C_element
FEATURE [App::DocumentObjectGroupPython] G4_C  # scripted group (container) (typed FeaturePython)
  Dunit = g/cm3
  Dvalue = 2
  Group = -> [C_element124]
  conduct = 2
  density = 1
  expand = 3
  formula = C
  name = G4_C
  specific = 4
FEATURE [App::DocumentObjectGroupPython] N_element048  label="N_element : 021"  # scripted group (container) (typed FeaturePython)
  n = 1
  ref = N_element
FEATURE [App::DocumentObjectGroupPython] G4_N  # scripted group (container) (typed FeaturePython)
  Dunit = g/cm3
  Dvalue = 0.0011652
  Group = -> [N_element048]
  conduct = 2
  density = 1
  expand = 3
  formula = N
  name = G4_N
  specific = 4
FEATURE [App::DocumentObjectGroupPython] O_element105  label="O_element : 059"  # scripted group (container) (typed FeaturePython)
  n = 1
  ref = O_element
FEATURE [App::DocumentObjectGroupPython] G4_O  # scripted group (container) (typed FeaturePython)
  Dunit = g/cm3
  Dvalue = 0.00133151
  Group = -> [O_element105]
  conduct = 2
  density = 1
  expand = 3
  formula = O
  name = G4_O
  specific = 4
FEATURE [App::DocumentObjectGroupPython] F_element019  label="F_element : 008"  # scripted group (container) (typed FeaturePython)
  n = 1
  ref = F_element
FEATURE [App::DocumentObjectGroupPython] G4_F  # scripted group (container) (typed FeaturePython)
  Dunit = g/cm3
  Dvalue = 0.00158029
  Group = -> [F_element019]
  conduct = 2
  density = 1
  expand = 3
  formula = F
  name = G4_F
  specific = 4
FEATURE [App::DocumentObjectGroupPython] Ne_element001  label="Ne_element : 1"  # scripted group (container) (typed FeaturePython)
  n = 1
  ref = Ne_element
FEATURE [App::DocumentObjectGroupPython] G4_Ne  # scripted group (container) (typed FeaturePython)
  Dunit = g/cm3
  Dvalue = 0.000838505
  Group = -> [Ne_element001]
  conduct = 2
  density = 1
  expand = 3
  formula = Ne
  name = G4_Ne
  specific = 4
FEATURE [App::DocumentObjectGroupPython] Na_element020  label="Na_element : 005"  # scripted group (container) (typed FeaturePython)
  n = 1
  ref = Na_element
FEATURE [App::DocumentObjectGroupPython] G4_Na  # scripted group (container) (typed FeaturePython)
  Dunit = g/cm3
  Dvalue = 0.971
  Group = -> [Na_element020]
  conduct = 2
  density = 1
  expand = 3
  formula = Na
  name = G4_Na
  specific = 4
FEATURE [App::DocumentObjectGroupPython] Mg_element011  label="Mg_element : 005"  # scripted group (container) (typed FeaturePython)
  n = 1
  ref = Mg_element
FEATURE [App::DocumentObjectGroupPython] G4_Mg  # scripted group (container) (typed FeaturePython)
  Dunit = g/cm3
  Dvalue = 1.74
  Group = -> [Mg_element011]
  conduct = 2
  density = 1
  expand = 3
  formula = Mg
  name = G4_Mg
  specific = 4
FEATURE [App::DocumentObjectGroupPython] Al_element004  label="Al_element : 1"  # scripted group (container) (typed FeaturePython)
  n = 1
  ref = Al_element
FEATURE [App::DocumentObjectGroupPython] G4_Al  # scripted group (container) (typed FeaturePython)
  Dunit = g/cm3
  Dvalue = 2.699
  Group = -> [Al_element004]
  conduct = 2
  density = 1
  expand = 3
  formula = Al
  name = G4_Al
  specific = 4
FEATURE [App::DocumentObjectGroupPython] Si_element007  label="Si_element : 002"  # scripted group (container) (typed FeaturePython)
  n = 1
  ref = Si_element
FEATURE [App::DocumentObjectGroupPython] G4_Si  # scripted group (container) (typed FeaturePython)
  Dunit = g/cm3
  Dvalue = 2.33
  Group = -> [Si_element007]
  conduct = 2
  density = 1
  expand = 3
  formula = Si
  name = G4_Si
  specific = 4
FEATURE [App::DocumentObjectGroupPython] P_element013  label="P_element : 002"  # scripted group (container) (typed FeaturePython)
  n = 1
  ref = P_element
FEATURE [App::DocumentObjectGroupPython] G4_P  # scripted group (container) (typed FeaturePython)
  Dunit = g/cm3
  Dvalue = 2.2
  Group = -> [P_element013]
  conduct = 2
  density = 1
  expand = 3
  formula = P
  name = G4_P
  specific = 4
FEATURE [App::DocumentObjectGroupPython] S_element023  label="S_element : 007"  # scripted group (container) (typed FeaturePython)
  n = 1
  ref = S_element
FEATURE [App::DocumentObjectGroupPython] G4_S  # scripted group (container) (typed FeaturePython)
  Dunit = g/cm3
  Dvalue = 2
  Group = -> [S_element023]
  conduct = 2
  density = 1
  expand = 3
  formula = S
  name = G4_S
  specific = 4
FEATURE [App::DocumentObjectGroupPython] Cl_element029  label="Cl_element : 015"  # scripted group (container) (typed FeaturePython)
  n = 1
  ref = Cl_element
FEATURE [App::DocumentObjectGroupPython] G4_Cl  # scripted group (container) (typed FeaturePython)
  Dunit = g/cm3
  Dvalue = 0.00299473
  Group = -> [Cl_element029]
  conduct = 2
  density = 1
  expand = 3
  formula = Cl
  name = G4_Cl
  specific = 4
FEATURE [App::DocumentObjectGroupPython] Ar_element002  label="Ar_element : 1"  # scripted group (container) (typed FeaturePython)
  n = 1
  ref = Ar_element
FEATURE [App::DocumentObjectGroupPython] G4_Ar  # scripted group (container) (typed FeaturePython)
  Dunit = g/cm3
  Dvalue = 0.00166201
  Group = -> [Ar_element002]
  conduct = 2
  density = 1
  expand = 3
  formula = Ar
  name = G4_Ar
  specific = 4
FEATURE [App::DocumentObjectGroupPython] K_element013  label="K_element : 003"  # scripted group (container) (typed FeaturePython)
  n = 1
  ref = K_element
FEATURE [App::DocumentObjectGroupPython] G4_K  # scripted group (container) (typed FeaturePython)
  Dunit = g/cm3
  Dvalue = 0.862
  Group = -> [K_element013]
  conduct = 2
  density = 1
  expand = 3
  formula = K
  name = G4_K
  specific = 4
FEATURE [App::DocumentObjectGroupPython] Ca_element014  label="Ca_element : 007"  # scripted group (container) (typed FeaturePython)
  n = 1
  ref = Ca_element
FEATURE [App::DocumentObjectGroupPython] G4_Ca  # scripted group (container) (typed FeaturePython)
  Dunit = g/cm3
  Dvalue = 1.55
  Group = -> [Ca_element014]
  conduct = 2
  density = 1
  expand = 3
  formula = Ca
  name = G4_Ca
  specific = 4
FEATURE [App::DocumentObjectGroupPython] Sc_element001  label="Sc_element : 1"  # scripted group (container) (typed FeaturePython)
  n = 1
  ref = Sc_element
FEATURE [App::DocumentObjectGroupPython] G4_Sc  # scripted group (container) (typed FeaturePython)
  Dunit = g/cm3
  Dvalue = 2.989
  Group = -> [Sc_element001]
  conduct = 2
  density = 1
  expand = 3
  formula = Sc
  name = G4_Sc
  specific = 4
FEATURE [App::DocumentObjectGroupPython] Ti_element004  label="Ti_element : 002"  # scripted group (container) (typed FeaturePython)
  n = 1
  ref = Ti_element
FEATURE [App::DocumentObjectGroupPython] G4_Ti  # scripted group (container) (typed FeaturePython)
  Dunit = g/cm3
  Dvalue = 4.54
  Group = -> [Ti_element004]
  conduct = 2
  density = 1
  expand = 3
  formula = Ti
  name = G4_Ti
  specific = 4
FEATURE [App::DocumentObjectGroupPython] V_element001  label="V_element : 1"  # scripted group (container) (typed FeaturePython)
  n = 1
  ref = V_element
FEATURE [App::DocumentObjectGroupPython] G4_V  # scripted group (container) (typed FeaturePython)
  Dunit = g/cm3
  Dvalue = 6.11
  Group = -> [V_element001]
  conduct = 2
  density = 1
  expand = 3
  formula = V
  name = G4_V
  specific = 4
FEATURE [App::DocumentObjectGroupPython] Cr_element001  label="Cr_element : 1"  # scripted group (container) (typed FeaturePython)
  n = 1
  ref = Cr_element
FEATURE [App::DocumentObjectGroupPython] G4_Cr  # scripted group (container) (typed FeaturePython)
  Dunit = g/cm3
  Dvalue = 7.18
  Group = -> [Cr_element001]
  conduct = 2
  density = 1
  expand = 3
  formula = Cr
  name = G4_Cr
  specific = 4
FEATURE [App::DocumentObjectGroupPython] Mn_element001  label="Mn_element : 1"  # scripted group (container) (typed FeaturePython)
  n = 1
  ref = Mn_element
FEATURE [App::DocumentObjectGroupPython] G4_Mn  # scripted group (container) (typed FeaturePython)
  Dunit = g/cm3
  Dvalue = 7.44
  Group = -> [Mn_element001]
  conduct = 2
  density = 1
  expand = 3
  formula = Mn
  name = G4_Mn
  specific = 4
FEATURE [App::DocumentObjectGroupPython] Fe_element007  label="Fe_element : 004"  # scripted group (container) (typed FeaturePython)
  n = 1
  ref = Fe_element
FEATURE [App::DocumentObjectGroupPython] G4_Fe  # scripted group (container) (typed FeaturePython)
  Dunit = g/cm3
  Dvalue = 7.874
  Group = -> [Fe_element007]
  conduct = 2
  density = 1
  expand = 3
  formula = Fe
  name = G4_Fe
  specific = 4
FEATURE [App::DocumentObjectGroupPython] Co_element001  label="Co_element : 1"  # scripted group (container) (typed FeaturePython)
  n = 1
  ref = Co_element
FEATURE [App::DocumentObjectGroupPython] G4_Co  # scripted group (container) (typed FeaturePython)
  Dunit = g/cm3
  Dvalue = 8.9
  Group = -> [Co_element001]
  conduct = 2
  density = 1
  expand = 3
  formula = Co
  name = G4_Co
  specific = 4
FEATURE [App::DocumentObjectGroupPython] Ni_element001  label="Ni_element : 1"  # scripted group (container) (typed FeaturePython)
  n = 1
  ref = Ni_element
FEATURE [App::DocumentObjectGroupPython] G4_Ni  # scripted group (container) (typed FeaturePython)
  Dunit = g/cm3
  Dvalue = 8.902
  Group = -> [Ni_element001]
  conduct = 2
  density = 1
  expand = 3
  formula = Ni
  name = G4_Ni
  specific = 4
FEATURE [App::DocumentObjectGroupPython] Cu_element001  label="Cu_element : 1"  # scripted group (container) (typed FeaturePython)
  n = 1
  ref = Cu_element
FEATURE [App::DocumentObjectGroupPython] G4_Cu  # scripted group (container) (typed FeaturePython)
  Dunit = g/cm3
  Dvalue = 8.96
  Group = -> [Cu_element001]
  conduct = 2
  density = 1
  expand = 3
  formula = Cu
  name = G4_Cu
  specific = 4
FEATURE [App::DocumentObjectGroupPython] Zn_element001  label="Zn_element : 1"  # scripted group (container) (typed FeaturePython)
  n = 1
  ref = Zn_element
FEATURE [App::DocumentObjectGroupPython] G4_Zn  # scripted group (container) (typed FeaturePython)
  Dunit = g/cm3
  Dvalue = 7.133
  Group = -> [Zn_element001]
  conduct = 2
  density = 1
  expand = 3
  formula = Zn
  name = G4_Zn
  specific = 4
FEATURE [App::DocumentObjectGroupPython] Ga_element002  label="Ga_element : 002"  # scripted group (container) (typed FeaturePython)
  n = 1
  ref = Ga_element
FEATURE [App::DocumentObjectGroupPython] G4_Ga  # scripted group (container) (typed FeaturePython)
  Dunit = g/cm3
  Dvalue = 5.904
  Group = -> [Ga_element002]
  conduct = 2
  density = 1
  expand = 3
  formula = Ga
  name = G4_Ga
  specific = 4
FEATURE [App::DocumentObjectGroupPython] Ge_element002  label="Ge_element : 1"  # scripted group (container) (typed FeaturePython)
  n = 1
  ref = Ge_element
FEATURE [App::DocumentObjectGroupPython] G4_Ge  # scripted group (container) (typed FeaturePython)
  Dunit = g/cm3
  Dvalue = 5.323
  Group = -> [Ge_element002]
  conduct = 2
  density = 1
  expand = 3
  formula = Ge
  name = G4_Ge
  specific = 4
FEATURE [App::DocumentObjectGroupPython] As_element003  label="As_element : 002"  # scripted group (container) (typed FeaturePython)
  n = 1
  ref = As_element
FEATURE [App::DocumentObjectGroupPython] G4_As  # scripted group (container) (typed FeaturePython)
  Dunit = g/cm3
  Dvalue = 5.73
  Group = -> [As_element003]
  conduct = 2
  density = 1
  expand = 3
  formula = As
  name = G4_As
  specific = 4
FEATURE [App::DocumentObjectGroupPython] Se_element001  label="Se_element : 1"  # scripted group (container) (typed FeaturePython)
  n = 1
  ref = Se_element
FEATURE [App::DocumentObjectGroupPython] G4_Se  # scripted group (container) (typed FeaturePython)
  Dunit = g/cm3
  Dvalue = 4.5
  Group = -> [Se_element001]
  conduct = 2
  density = 1
  expand = 3
  formula = Se
  name = G4_Se
  specific = 4
FEATURE [App::DocumentObjectGroupPython] Br_element007  label="Br_element : 004"  # scripted group (container) (typed FeaturePython)
  n = 1
  ref = Br_element
FEATURE [App::DocumentObjectGroupPython] G4_Br  # scripted group (container) (typed FeaturePython)
  Dunit = g/cm3
  Dvalue = 0.0070721
  Group = -> [Br_element007]
  conduct = 2
  density = 1
  expand = 3
  formula = Br
  name = G4_Br
  specific = 4
FEATURE [App::DocumentObjectGroupPython] Kr_element001  label="Kr_element : 1"  # scripted group (container) (typed FeaturePython)
  n = 1
  ref = Kr_element
FEATURE [App::DocumentObjectGroupPython] G4_Kr  # scripted group (container) (typed FeaturePython)
  Dunit = g/cm3
  Dvalue = 0.00347832
  Group = -> [Kr_element001]
  conduct = 2
  density = 1
  expand = 3
  formula = Kr
  name = G4_Kr
  specific = 4
FEATURE [App::DocumentObjectGroupPython] Rb_element001  label="Rb_element : 1"  # scripted group (container) (typed FeaturePython)
  n = 1
  ref = Rb_element
FEATURE [App::DocumentObjectGroupPython] G4_Rb  # scripted group (container) (typed FeaturePython)
  Dunit = g/cm3
  Dvalue = 1.532
  Group = -> [Rb_element001]
  conduct = 2
  density = 1
  expand = 3
  formula = Rb
  name = G4_Rb
  specific = 4
FEATURE [App::DocumentObjectGroupPython] Sr_element001  label="Sr_element : 1"  # scripted group (container) (typed FeaturePython)
  n = 1
  ref = Sr_element
FEATURE [App::DocumentObjectGroupPython] G4_Sr  # scripted group (container) (typed FeaturePython)
  Dunit = g/cm3
  Dvalue = 2.54
  Group = -> [Sr_element001]
  conduct = 2
  density = 1
  expand = 3
  formula = Sr
  name = G4_Sr
  specific = 4
FEATURE [App::DocumentObjectGroupPython] Y_element001  label="Y_element : 1"  # scripted group (container) (typed FeaturePython)
  n = 1
  ref = Y_element
FEATURE [App::DocumentObjectGroupPython] G4_Y  # scripted group (container) (typed FeaturePython)
  Dunit = g/cm3
  Dvalue = 4.469
  Group = -> [Y_element001]
  conduct = 2
  density = 1
  expand = 3
  formula = Y
  name = G4_Y
  specific = 4
FEATURE [App::DocumentObjectGroupPython] Zr_element001  label="Zr_element : 1"  # scripted group (container) (typed FeaturePython)
  n = 1
  ref = Zr_element
FEATURE [App::DocumentObjectGroupPython] G4_Zr  # scripted group (container) (typed FeaturePython)
  Dunit = g/cm3
  Dvalue = 6.506
  Group = -> [Zr_element001]
  conduct = 2
  density = 1
  expand = 3
  formula = Zr
  name = G4_Zr
  specific = 4
FEATURE [App::DocumentObjectGroupPython] Nb_element001  label="Nb_element : 1"  # scripted group (container) (typed FeaturePython)
  n = 1
  ref = Nb_element
FEATURE [App::DocumentObjectGroupPython] G4_Nb  # scripted group (container) (typed FeaturePython)
  Dunit = g/cm3
  Dvalue = 8.57
  Group = -> [Nb_element001]
  conduct = 2
  density = 1
  expand = 3
  formula = Nb
  name = G4_Nb
  specific = 4
FEATURE [App::DocumentObjectGroupPython] Mo_element001  label="Mo_element : 1"  # scripted group (container) (typed FeaturePython)
  n = 1
  ref = Mo_element
FEATURE [App::DocumentObjectGroupPython] G4_Mo  # scripted group (container) (typed FeaturePython)
  Dunit = g/cm3
  Dvalue = 10.22
  Group = -> [Mo_element001]
  conduct = 2
  density = 1
  expand = 3
  formula = Mo
  name = G4_Mo
  specific = 4
FEATURE [App::DocumentObjectGroupPython] Tc_element001  label="Tc_element : 1"  # scripted group (container) (typed FeaturePython)
  n = 1
  ref = Tc_element
FEATURE [App::DocumentObjectGroupPython] G4_Tc  # scripted group (container) (typed FeaturePython)
  Dunit = g/cm3
  Dvalue = 11.5
  Group = -> [Tc_element001]
  conduct = 2
  density = 1
  expand = 3
  formula = Tc
  name = G4_Tc
  specific = 4
FEATURE [App::DocumentObjectGroupPython] Ru_element001  label="Ru_element : 1"  # scripted group (container) (typed FeaturePython)
  n = 1
  ref = Ru_element
FEATURE [App::DocumentObjectGroupPython] G4_Ru  # scripted group (container) (typed FeaturePython)
  Dunit = g/cm3
  Dvalue = 12.41
  Group = -> [Ru_element001]
  conduct = 2
  density = 1
  expand = 3
  formula = Ru
  name = G4_Ru
  specific = 4
FEATURE [App::DocumentObjectGroupPython] Rh_element001  label="Rh_element : 1"  # scripted group (container) (typed FeaturePython)
  n = 1
  ref = Rh_element
FEATURE [App::DocumentObjectGroupPython] G4_Rh  # scripted group (container) (typed FeaturePython)
  Dunit = g/cm3
  Dvalue = 12.41
  Group = -> [Rh_element001]
  conduct = 2
  density = 1
  expand = 3
  formula = Rh
  name = G4_Rh
  specific = 4
FEATURE [App::DocumentObjectGroupPython] Pd_element001  label="Pd_element : 1"  # scripted group (container) (typed FeaturePython)
  n = 1
  ref = Pd_element
FEATURE [App::DocumentObjectGroupPython] G4_Pd  # scripted group (container) (typed FeaturePython)
  Dunit = g/cm3
  Dvalue = 12.02
  Group = -> [Pd_element001]
  conduct = 2
  density = 1
  expand = 3
  formula = Pd
  name = G4_Pd
  specific = 4
FEATURE [App::DocumentObjectGroupPython] Ag_element006  label="Ag_element : 004"  # scripted group (container) (typed FeaturePython)
  n = 1
  ref = Ag_element
FEATURE [App::DocumentObjectGroupPython] G4_Ag  # scripted group (container) (typed FeaturePython)
  Dunit = g/cm3
  Dvalue = 10.5
  Group = -> [Ag_element006]
  conduct = 2
  density = 1
  expand = 3
  formula = Ag
  name = G4_Ag
  specific = 4
FEATURE [App::DocumentObjectGroupPython] Cd_element003  label="Cd_element : 003"  # scripted group (container) (typed FeaturePython)
  n = 1
  ref = Cd_element
FEATURE [App::DocumentObjectGroupPython] G4_Cd  # scripted group (container) (typed FeaturePython)
  Dunit = g/cm3
  Dvalue = 8.65
  Group = -> [Cd_element003]
  conduct = 2
  density = 1
  expand = 3
  formula = Cd
  name = G4_Cd
  specific = 4
FEATURE [App::DocumentObjectGroupPython] In_element001  label="In_element : 1"  # scripted group (container) (typed FeaturePython)
  n = 1
  ref = In_element
FEATURE [App::DocumentObjectGroupPython] G4_In  # scripted group (container) (typed FeaturePython)
  Dunit = g/cm3
  Dvalue = 7.31
  Group = -> [In_element001]
  conduct = 2
  density = 1
  expand = 3
  formula = In
  name = G4_In
  specific = 4
FEATURE [App::DocumentObjectGroupPython] Sn_element001  label="Sn_element : 1"  # scripted group (container) (typed FeaturePython)
  n = 1
  ref = Sn_element
FEATURE [App::DocumentObjectGroupPython] G4_Sn  # scripted group (container) (typed FeaturePython)
  Dunit = g/cm3
  Dvalue = 7.31
  Group = -> [Sn_element001]
  conduct = 2
  density = 1
  expand = 3
  formula = Sn
  name = G4_Sn
  specific = 4
FEATURE [App::DocumentObjectGroupPython] Sb_element001  label="Sb_element : 1"  # scripted group (container) (typed FeaturePython)
  n = 1
  ref = Sb_element
FEATURE [App::DocumentObjectGroupPython] G4_Sb  # scripted group (container) (typed FeaturePython)
  Dunit = g/cm3
  Dvalue = 6.691
  Group = -> [Sb_element001]
  conduct = 2
  density = 1
  expand = 3
  formula = Sb
  name = G4_Sb
  specific = 4
FEATURE [App::DocumentObjectGroupPython] Te_element002  label="Te_element : 002"  # scripted group (container) (typed FeaturePython)
  n = 1
  ref = Te_element
FEATURE [App::DocumentObjectGroupPython] G4_Te  # scripted group (container) (typed FeaturePython)
  Dunit = g/cm3
  Dvalue = 6.24
  Group = -> [Te_element002]
  conduct = 2
  density = 1
  expand = 3
  formula = Te
  name = G4_Te
  specific = 4
FEATURE [App::DocumentObjectGroupPython] I_element010  label="I_element : 006"  # scripted group (container) (typed FeaturePython)
  n = 1
  ref = I_element
FEATURE [App::DocumentObjectGroupPython] G4_I  # scripted group (container) (typed FeaturePython)
  Dunit = g/cm3
  Dvalue = 4.93
  Group = -> [I_element010]
  conduct = 2
  density = 1
  expand = 3
  formula = I
  name = G4_I
  specific = 4
FEATURE [App::DocumentObjectGroupPython] Xe_element001  label="Xe_element : 1"  # scripted group (container) (typed FeaturePython)
  n = 1
  ref = Xe_element
FEATURE [App::DocumentObjectGroupPython] G4_Xe  # scripted group (container) (typed FeaturePython)
  Dunit = g/cm3
  Dvalue = 0.00548536
  Group = -> [Xe_element001]
  conduct = 2
  density = 1
  expand = 3
  formula = Xe
  name = G4_Xe
  specific = 4
FEATURE [App::DocumentObjectGroupPython] Cs_element003  label="Cs_element : 003"  # scripted group (container) (typed FeaturePython)
  n = 1
  ref = Cs_element
FEATURE [App::DocumentObjectGroupPython] G4_Cs  # scripted group (container) (typed FeaturePython)
  Dunit = g/cm3
  Dvalue = 1.873
  Group = -> [Cs_element003]
  conduct = 2
  density = 1
  expand = 3
  formula = Cs
  name = G4_Cs
  specific = 4
FEATURE [App::DocumentObjectGroupPython] Ba_element003  label="Ba_element : 003"  # scripted group (container) (typed FeaturePython)
  n = 1
  ref = Ba_element
FEATURE [App::DocumentObjectGroupPython] G4_Ba  # scripted group (container) (typed FeaturePython)
  Dunit = g/cm3
  Dvalue = 3.5
  Group = -> [Ba_element003]
  conduct = 2
  density = 1
  expand = 3
  formula = Ba
  name = G4_Ba
  specific = 4
FEATURE [App::DocumentObjectGroupPython] La_element003  label="La_element : 003"  # scripted group (container) (typed FeaturePython)
  n = 1
  ref = La_element
FEATURE [App::DocumentObjectGroupPython] G4_La  # scripted group (container) (typed FeaturePython)
  Dunit = g/cm3
  Dvalue = 6.154
  Group = -> [La_element003]
  conduct = 2
  density = 1
  expand = 3
  formula = La
  name = G4_La
  specific = 4
FEATURE [App::DocumentObjectGroupPython] Ce_element002  label="Ce_element : 1"  # scripted group (container) (typed FeaturePython)
  n = 1
  ref = Ce_element
FEATURE [App::DocumentObjectGroupPython] G4_Ce  # scripted group (container) (typed FeaturePython)
  Dunit = g/cm3
  Dvalue = 6.657
  Group = -> [Ce_element002]
  conduct = 2
  density = 1
  expand = 3
  formula = Ce
  name = G4_Ce
  specific = 4
FEATURE [App::DocumentObjectGroupPython] Pr_element001  label="Pr_element : 1"  # scripted group (container) (typed FeaturePython)
  n = 1
  ref = Pr_element
FEATURE [App::DocumentObjectGroupPython] G4_Pr  # scripted group (container) (typed FeaturePython)
  Dunit = g/cm3
  Dvalue = 6.71
  Group = -> [Pr_element001]
  conduct = 2
  density = 1
  expand = 3
  formula = Pr
  name = G4_Pr
  specific = 4
FEATURE [App::DocumentObjectGroupPython] Nd_element001  label="Nd_element : 1"  # scripted group (container) (typed FeaturePython)
  n = 1
  ref = Nd_element
FEATURE [App::DocumentObjectGroupPython] G4_Nd  # scripted group (container) (typed FeaturePython)
  Dunit = g/cm3
  Dvalue = 6.9
  Group = -> [Nd_element001]
  conduct = 2
  density = 1
  expand = 3
  formula = Nd
  name = G4_Nd
  specific = 4
FEATURE [App::DocumentObjectGroupPython] Pm_element001  label="Pm_element : 1"  # scripted group (container) (typed FeaturePython)
  n = 1
  ref = Pm_element
FEATURE [App::DocumentObjectGroupPython] G4_Pm  # scripted group (container) (typed FeaturePython)
  Dunit = g/cm3
  Dvalue = 7.22
  Group = -> [Pm_element001]
  conduct = 2
  density = 1
  expand = 3
  formula = Pm
  name = G4_Pm
  specific = 4
FEATURE [App::DocumentObjectGroupPython] Sm_element001  label="Sm_element : 1"  # scripted group (container) (typed FeaturePython)
  n = 1
  ref = Sm_element
FEATURE [App::DocumentObjectGroupPython] G4_Sm  # scripted group (container) (typed FeaturePython)
  Dunit = g/cm3
  Dvalue = 7.46
  Group = -> [Sm_element001]
  conduct = 2
  density = 1
  expand = 3
  formula = Sm
  name = G4_Sm
  specific = 4
FEATURE [App::DocumentObjectGroupPython] Eu_element001  label="Eu_element : 1"  # scripted group (container) (typed FeaturePython)
  n = 1
  ref = Eu_element
FEATURE [App::DocumentObjectGroupPython] G4_Eu  # scripted group (container) (typed FeaturePython)
  Dunit = g/cm3
  Dvalue = 5.243
  Group = -> [Eu_element001]
  conduct = 2
  density = 1
  expand = 3
  formula = Eu
  name = G4_Eu
  specific = 4
FEATURE [App::DocumentObjectGroupPython] Gd_element002  label="Gd_element : 1"  # scripted group (container) (typed FeaturePython)
  n = 1
  ref = Gd_element
FEATURE [App::DocumentObjectGroupPython] G4_Gd  # scripted group (container) (typed FeaturePython)
  Dunit = g/cm3
  Dvalue = 7.9004
  Group = -> [Gd_element002]
  conduct = 2
  density = 1
  expand = 3
  formula = Gd
  name = G4_Gd
  specific = 4
FEATURE [App::DocumentObjectGroupPython] Tb_element001  label="Tb_element : 1"  # scripted group (container) (typed FeaturePython)
  n = 1
  ref = Tb_element
FEATURE [App::DocumentObjectGroupPython] G4_Tb  # scripted group (container) (typed FeaturePython)
  Dunit = g/cm3
  Dvalue = 8.229
  Group = -> [Tb_element001]
  conduct = 2
  density = 1
  expand = 3
  formula = Tb
  name = G4_Tb
  specific = 4
FEATURE [App::DocumentObjectGroupPython] Dy_element001  label="Dy_element : 1"  # scripted group (container) (typed FeaturePython)
  n = 1
  ref = Dy_element
FEATURE [App::DocumentObjectGroupPython] G4_Dy  # scripted group (container) (typed FeaturePython)
  Dunit = g/cm3
  Dvalue = 8.55
  Group = -> [Dy_element001]
  conduct = 2
  density = 1
  expand = 3
  formula = Dy
  name = G4_Dy
  specific = 4
FEATURE [App::DocumentObjectGroupPython] Ho_element001  label="Ho_element : 1"  # scripted group (container) (typed FeaturePython)
  n = 1
  ref = Ho_element
FEATURE [App::DocumentObjectGroupPython] G4_Ho  # scripted group (container) (typed FeaturePython)
  Dunit = g/cm3
  Dvalue = 8.795
  Group = -> [Ho_element001]
  conduct = 2
  density = 1
  expand = 3
  formula = Ho
  name = G4_Ho
  specific = 4
FEATURE [App::DocumentObjectGroupPython] Er_element001  label="Er_element : 1"  # scripted group (container) (typed FeaturePython)
  n = 1
  ref = Er_element
FEATURE [App::DocumentObjectGroupPython] G4_Er  # scripted group (container) (typed FeaturePython)
  Dunit = g/cm3
  Dvalue = 9.066
  Group = -> [Er_element001]
  conduct = 2
  density = 1
  expand = 3
  formula = Er
  name = G4_Er
  specific = 4
FEATURE [App::DocumentObjectGroupPython] Tm_element001  label="Tm_element : 1"  # scripted group (container) (typed FeaturePython)
  n = 1
  ref = Tm_element
FEATURE [App::DocumentObjectGroupPython] G4_Tm  # scripted group (container) (typed FeaturePython)
  Dunit = g/cm3
  Dvalue = 9.321
  Group = -> [Tm_element001]
  conduct = 2
  density = 1
  expand = 3
  formula = Tm
  name = G4_Tm
  specific = 4
FEATURE [App::DocumentObjectGroupPython] Yb_element001  label="Yb_element : 1"  # scripted group (container) (typed FeaturePython)
  n = 1
  ref = Yb_element
FEATURE [App::DocumentObjectGroupPython] G4_Yb  # scripted group (container) (typed FeaturePython)
  Dunit = g/cm3
  Dvalue = 6.73
  Group = -> [Yb_element001]
  conduct = 2
  density = 1
  expand = 3
  formula = Yb
  name = G4_Yb
  specific = 4
FEATURE [App::DocumentObjectGroupPython] Lu_element001  label="Lu_element : 1"  # scripted group (container) (typed FeaturePython)
  n = 1
  ref = Lu_element
FEATURE [App::DocumentObjectGroupPython] G4_Lu  # scripted group (container) (typed FeaturePython)
  Dunit = g/cm3
  Dvalue = 9.84
  Group = -> [Lu_element001]
  conduct = 2
  density = 1
  expand = 3
  formula = Lu
  name = G4_Lu
  specific = 4
FEATURE [App::DocumentObjectGroupPython] Hf_element001  label="Hf_element : 1"  # scripted group (container) (typed FeaturePython)
  n = 1
  ref = Hf_element
FEATURE [App::DocumentObjectGroupPython] G4_Hf  # scripted group (container) (typed FeaturePython)
  Dunit = g/cm3
  Dvalue = 13.31
  Group = -> [Hf_element001]
  conduct = 2
  density = 1
  expand = 3
  formula = Hf
  name = G4_Hf
  specific = 4
FEATURE [App::DocumentObjectGroupPython] Ta_element001  label="Ta_element : 1"  # scripted group (container) (typed FeaturePython)
  n = 1
  ref = Ta_element
FEATURE [App::DocumentObjectGroupPython] G4_Ta  # scripted group (container) (typed FeaturePython)
  Dunit = g/cm3
  Dvalue = 16.654
  Group = -> [Ta_element001]
  conduct = 2
  density = 1
  expand = 3
  formula = Ta
  name = G4_Ta
  specific = 4
FEATURE [App::DocumentObjectGroupPython] W_element004  label="W_element : 004"  # scripted group (container) (typed FeaturePython)
  n = 1
  ref = W_element
FEATURE [App::DocumentObjectGroupPython] G4_W  # scripted group (container) (typed FeaturePython)
  Dunit = g/cm3
  Dvalue = 19.3
  Group = -> [W_element004]
  conduct = 2
  density = 1
  expand = 3
  formula = W
  name = G4_W
  specific = 4
FEATURE [App::DocumentObjectGroupPython] Re_element001  label="Re_element : 1"  # scripted group (container) (typed FeaturePython)
  n = 1
  ref = Re_element
FEATURE [App::DocumentObjectGroupPython] G4_Re  # scripted group (container) (typed FeaturePython)
  Dunit = g/cm3
  Dvalue = 21.02
  Group = -> [Re_element001]
  conduct = 2
  density = 1
  expand = 3
  formula = Re
  name = G4_Re
  specific = 4
FEATURE [App::DocumentObjectGroupPython] Os_element001  label="Os_element : 1"  # scripted group (container) (typed FeaturePython)
  n = 1
  ref = Os_element
FEATURE [App::DocumentObjectGroupPython] G4_Os  # scripted group (container) (typed FeaturePython)
  Dunit = g/cm3
  Dvalue = 22.57
  Group = -> [Os_element001]
  conduct = 2
  density = 1
  expand = 3
  formula = Os
  name = G4_Os
  specific = 4
FEATURE [App::DocumentObjectGroupPython] Ir_element001  label="Ir_element : 1"  # scripted group (container) (typed FeaturePython)
  n = 1
  ref = Ir_element
FEATURE [App::DocumentObjectGroupPython] G4_Ir  # scripted group (container) (typed FeaturePython)
  Dunit = g/cm3
  Dvalue = 22.42
  Group = -> [Ir_element001]
  conduct = 2
  density = 1
  expand = 3
  formula = Ir
  name = G4_Ir
  specific = 4
FEATURE [App::DocumentObjectGroupPython] Pt_element001  label="Pt_element : 1"  # scripted group (container) (typed FeaturePython)
  n = 1
  ref = Pt_element
FEATURE [App::DocumentObjectGroupPython] G4_Pt  # scripted group (container) (typed FeaturePython)
  Dunit = g/cm3
  Dvalue = 21.45
  Group = -> [Pt_element001]
  conduct = 2
  density = 1
  expand = 3
  formula = Pt
  name = G4_Pt
  specific = 4
FEATURE [App::DocumentObjectGroupPython] Au_element001  label="Au_element : 1"  # scripted group (container) (typed FeaturePython)
  n = 1
  ref = Au_element
FEATURE [App::DocumentObjectGroupPython] G4_Au  # scripted group (container) (typed FeaturePython)
  Dunit = g/cm3
  Dvalue = 19.32
  Group = -> [Au_element001]
  conduct = 2
  density = 1
  expand = 3
  formula = Au
  name = G4_Au
  specific = 4
FEATURE [App::DocumentObjectGroupPython] Hg_element002  label="Hg_element : 002"  # scripted group (container) (typed FeaturePython)
  n = 1
  ref = Hg_element
FEATURE [App::DocumentObjectGroupPython] G4_Hg  # scripted group (container) (typed FeaturePython)
  Dunit = g/cm3
  Dvalue = 13.546
  Group = -> [Hg_element002]
  conduct = 2
  density = 1
  expand = 3
  formula = Hg
  name = G4_Hg
  specific = 4
FEATURE [App::DocumentObjectGroupPython] Tl_element002  label="Tl_element : 002"  # scripted group (container) (typed FeaturePython)
  n = 1
  ref = Tl_element
FEATURE [App::DocumentObjectGroupPython] G4_Tl  # scripted group (container) (typed FeaturePython)
  Dunit = g/cm3
  Dvalue = 11.72
  Group = -> [Tl_element002]
  conduct = 2
  density = 1
  expand = 3
  formula = Tl
  name = G4_Tl
  specific = 4
FEATURE [App::DocumentObjectGroupPython] Pb_element003  label="Pb_element : 1"  # scripted group (container) (typed FeaturePython)
  n = 1
  ref = Pb_element
FEATURE [App::DocumentObjectGroupPython] G4_Pb  # scripted group (container) (typed FeaturePython)
  Dunit = g/cm3
  Dvalue = 11.35
  Group = -> [Pb_element003]
  conduct = 2
  density = 1
  expand = 3
  formula = Pb
  name = G4_Pb
  specific = 4
FEATURE [App::DocumentObjectGroupPython] Bi_element002  label="Bi_element : 1"  # scripted group (container) (typed FeaturePython)
  n = 1
  ref = Bi_element
FEATURE [App::DocumentObjectGroupPython] G4_Bi  # scripted group (container) (typed FeaturePython)
  Dunit = g/cm3
  Dvalue = 9.747
  Group = -> [Bi_element002]
  conduct = 2
  density = 1
  expand = 3
  formula = Bi
  name = G4_Bi
  specific = 4
FEATURE [App::DocumentObjectGroupPython] Po_element001  label="Po_element : 1"  # scripted group (container) (typed FeaturePython)
  n = 1
  ref = Po_element
FEATURE [App::DocumentObjectGroupPython] G4_Po  # scripted group (container) (typed FeaturePython)
  Dunit = g/cm3
  Dvalue = 9.32
  Group = -> [Po_element001]
  conduct = 2
  density = 1
  expand = 3
  formula = Po
  name = G4_Po
  specific = 4
FEATURE [App::DocumentObjectGroupPython] At_element001  label="At_element : 1"  # scripted group (container) (typed FeaturePython)
  n = 1
  ref = At_element
FEATURE [App::DocumentObjectGroupPython] G4_At  # scripted group (container) (typed FeaturePython)
  Dunit = g/cm3
  Dvalue = 9.32
  Group = -> [At_element001]
  conduct = 2
  density = 1
  expand = 3
  formula = At
  name = G4_At
  specific = 4
FEATURE [App::DocumentObjectGroupPython] Rn_element001  label="Rn_element : 1"  # scripted group (container) (typed FeaturePython)
  n = 1
  ref = Rn_element
FEATURE [App::DocumentObjectGroupPython] G4_Rn  # scripted group (container) (typed FeaturePython)
  Dunit = g/cm3
  Dvalue = 0.00900662
  Group = -> [Rn_element001]
  conduct = 2
  density = 1
  expand = 3
  formula = Rn
  name = G4_Rn
  specific = 4
FEATURE [App::DocumentObjectGroupPython] Fr_element001  label="Fr_element : 1"  # scripted group (container) (typed FeaturePython)
  n = 1
  ref = Fr_element
FEATURE [App::DocumentObjectGroupPython] G4_Fr  # scripted group (container) (typed FeaturePython)
  Dunit = g/cm3
  Dvalue = 1
  Group = -> [Fr_element001]
  conduct = 2
  density = 1
  expand = 3
  formula = Fr
  name = G4_Fr
  specific = 4
FEATURE [App::DocumentObjectGroupPython] Ra_element001  label="Ra_element : 1"  # scripted group (container) (typed FeaturePython)
  n = 1
  ref = Ra_element
FEATURE [App::DocumentObjectGroupPython] G4_Ra  # scripted group (container) (typed FeaturePython)
  Dunit = g/cm3
  Dvalue = 5
  Group = -> [Ra_element001]
  conduct = 2
  density = 1
  expand = 3
  formula = Ra
  name = G4_Ra
  specific = 4
FEATURE [App::DocumentObjectGroupPython] Ac_element001  label="Ac_element : 1"  # scripted group (container) (typed FeaturePython)
  n = 1
  ref = Ac_element
FEATURE [App::DocumentObjectGroupPython] G4_Ac  # scripted group (container) (typed FeaturePython)
  Dunit = g/cm3
  Dvalue = 10.07
  Group = -> [Ac_element001]
  conduct = 2
  density = 1
  expand = 3
  formula = Ac
  name = G4_Ac
  specific = 4
FEATURE [App::DocumentObjectGroupPython] Th_element001  label="Th_element : 1"  # scripted group (container) (typed FeaturePython)
  n = 1
  ref = Th_element
FEATURE [App::DocumentObjectGroupPython] G4_Th  # scripted group (container) (typed FeaturePython)
  Dunit = g/cm3
  Dvalue = 11.72
  Group = -> [Th_element001]
  conduct = 2
  density = 1
  expand = 3
  formula = Th
  name = G4_Th
  specific = 4
FEATURE [App::DocumentObjectGroupPython] Pa_element001  label="Pa_element : 1"  # scripted group (container) (typed FeaturePython)
  n = 1
  ref = Pa_element
FEATURE [App::DocumentObjectGroupPython] G4_Pa  # scripted group (container) (typed FeaturePython)
  Dunit = g/cm3
  Dvalue = 15.37
  Group = -> [Pa_element001]
  conduct = 2
  density = 1
  expand = 3
  formula = Pa
  name = G4_Pa
  specific = 4
FEATURE [App::DocumentObjectGroupPython] U_element004  label="U_element : 004"  # scripted group (container) (typed FeaturePython)
  n = 1
  ref = U_element
FEATURE [App::DocumentObjectGroupPython] G4_U  # scripted group (container) (typed FeaturePython)
  Dunit = g/cm3
  Dvalue = 18.95
  Group = -> [U_element004]
  conduct = 2
  density = 1
  expand = 3
  formula = U
  name = G4_U
  specific = 4
FEATURE [App::DocumentObjectGroupPython] Np_element001  label="Np_element : 1"  # scripted group (container) (typed FeaturePython)
  n = 1
  ref = Np_element
FEATURE [App::DocumentObjectGroupPython] G4_Np  # scripted group (container) (typed FeaturePython)
  Dunit = g/cm3
  Dvalue = 20.25
  Group = -> [Np_element001]
  conduct = 2
  density = 1
  expand = 3
  formula = Np
  name = G4_Np
  specific = 4
FEATURE [App::DocumentObjectGroupPython] Pu_element002  label="Pu_element : 002"  # scripted group (container) (typed FeaturePython)
  n = 1
  ref = Pu_element
FEATURE [App::DocumentObjectGroupPython] G4_Pu  # scripted group (container) (typed FeaturePython)
  Dunit = g/cm3
  Dvalue = 19.84
  Group = -> [Pu_element002]
  conduct = 2
  density = 1
  expand = 3
  formula = Pu
  name = G4_Pu
  specific = 4
FEATURE [App::DocumentObjectGroupPython] Am_element001  label="Am_element : 1"  # scripted group (container) (typed FeaturePython)
  n = 1
  ref = Am_element
FEATURE [App::DocumentObjectGroupPython] G4_Am  # scripted group (container) (typed FeaturePython)
  Dunit = g/cm3
  Dvalue = 13.67
  Group = -> [Am_element001]
  conduct = 2
  density = 1
  expand = 3
  formula = Am
  name = G4_Am
  specific = 4
FEATURE [App::DocumentObjectGroupPython] Cm_element001  label="Cm_element : 1"  # scripted group (container) (typed FeaturePython)
  n = 1
  ref = Cm_element
FEATURE [App::DocumentObjectGroupPython] G4_Cm  # scripted group (container) (typed FeaturePython)
  Dunit = g/cm3
  Dvalue = 13.51
  Group = -> [Cm_element001]
  conduct = 2
  density = 1
  expand = 3
  formula = Cm
  name = G4_Cm
  specific = 4
FEATURE [App::DocumentObjectGroupPython] Bk_element001  label="Bk_element : 1"  # scripted group (container) (typed FeaturePython)
  n = 1
  ref = Bk_element
FEATURE [App::DocumentObjectGroupPython] G4_Bk  # scripted group (container) (typed FeaturePython)
  Dunit = g/cm3
  Dvalue = 14
  Group = -> [Bk_element001]
  conduct = 2
  density = 1
  expand = 3
  formula = Bk
  name = G4_Bk
  specific = 4
FEATURE [App::DocumentObjectGroupPython] Cf_element001  label="Cf_element : 1"  # scripted group (container) (typed FeaturePython)
  n = 1
  ref = Cf_element
FEATURE [App::DocumentObjectGroupPython] G4_Cf  # scripted group (container) (typed FeaturePython)
  Dunit = g/cm3
  Dvalue = 10
  Group = -> [Cf_element001]
  conduct = 2
  density = 1
  expand = 3
  formula = Cf
  name = G4_Cf
  specific = 4
FEATURE [App::DocumentObjectGroupPython] Element  # scripted group (container) (typed FeaturePython)
  Group = -> [G4_H,G4_He,G4_Li,G4_Be,G4_B,G4_C,G4_N,G4_O,G4_F,G4_Ne,G4_Na,G4_Mg,G4_Al,G4_Si,G4_P,G4_S,G4_Cl,G4_Ar,G4_K,G4_Ca,G4_Sc,G4_Ti,G4_V,G4_Cr,G4_Mn,G4_Fe,G4_Co,G4_Ni,G4_Cu,G4_Zn,G4_Ga,G4_Ge,G4_As,G4_Se,G4_Br,G4_Kr,G4_Rb,G4_Sr,G4_Y,G4_Zr,G4_Nb,G4_Mo,G4_Tc,G4_Ru,G4_Rh,G4_Pd,G4_Ag,G4_Cd,G4_In,G4_Sn,G4_Sb,G4_Te,G4_I,G4_Xe,G4_Cs,G4_Ba,G4_La,G4_Ce,G4_Pr,G4_Nd,G4_Pm,G4_Sm,G4_Eu,G4_Gd,G4_Tb,G4_Dy,G4_Ho,G4_Er,+30 more]
FEATURE [App::DocumentObjectGroupPython] H_element114  label="H_element : 063"  # scripted group (container) (typed FeaturePython)
  n = 2
  ref = H_element
FEATURE [App::DocumentObjectGroupPython] G4_lH2  # scripted group (container) (typed FeaturePython)
  Dunit = g/cm3
  Dvalue = 0.0708
  Group = -> [H_element114]
  conduct = 2
  density = 1
  expand = 3
  formula = G4_lH2
  name = G4_lH2
  specific = 4
FEATURE [App::DocumentObjectGroupPython] N_element049  label="N_element : 022"  # scripted group (container) (typed FeaturePython)
  n = 2
  ref = N_element
FEATURE [App::DocumentObjectGroupPython] G4_lN2  # scripted group (container) (typed FeaturePython)
  Dunit = g/cm3
  Dvalue = 0.807
  Group = -> [N_element049]
  conduct = 2
  density = 1
  expand = 3
  formula = G4_lN2
  name = G4_lN2
  specific = 4
FEATURE [App::DocumentObjectGroupPython] O_element106  label="O_element : 060"  # scripted group (container) (typed FeaturePython)
  n = 2
  ref = O_element
FEATURE [App::DocumentObjectGroupPython] G4_lO2  # scripted group (container) (typed FeaturePython)
  Dunit = g/cm3
  Dvalue = 1.141
  Group = -> [O_element106]
  conduct = 2
  density = 1
  expand = 3
  formula = G4_lO2
  name = G4_lO2
  specific = 4
FEATURE [App::DocumentObjectGroupPython] Ar  label="Ar : 1"  # scripted group (container) (typed FeaturePython)
  n = 1
  ref = Ar
FEATURE [App::DocumentObjectGroupPython] G4_lAr  # scripted group (container) (typed FeaturePython)
  Dunit = g/cm3
  Dvalue = 1.396
  Group = -> [Ar]
  conduct = 2
  density = 1
  expand = 3
  formula = G4_lAr
  name = G4_lAr
  specific = 4
FEATURE [App::DocumentObjectGroupPython] Br  label="Br : 1"  # scripted group (container) (typed FeaturePython)
  n = 1
  ref = Br
FEATURE [App::DocumentObjectGroupPython] G4_lBr  # scripted group (container) (typed FeaturePython)
  Dunit = g/cm3
  Dvalue = 3.1028
  Group = -> [Br]
  conduct = 2
  density = 1
  expand = 3
  formula = G4_lBr
  name = G4_lBr
  specific = 4
FEATURE [App::DocumentObjectGroupPython] Kr  label="Kr : 1"  # scripted group (container) (typed FeaturePython)
  n = 1
  ref = Kr
FEATURE [App::DocumentObjectGroupPython] G4_lKr  # scripted group (container) (typed FeaturePython)
  Dunit = g/cm3
  Dvalue = 2.418
  Group = -> [Kr]
  conduct = 2
  density = 1
  expand = 3
  formula = G4_lKr
  name = G4_lKr
  specific = 4
FEATURE [App::DocumentObjectGroupPython] Xe  label="Xe : 1"  # scripted group (container) (typed FeaturePython)
  n = 1
  ref = Xe
FEATURE [App::DocumentObjectGroupPython] G4_lXe  # scripted group (container) (typed FeaturePython)
  Dunit = g/cm3
  Dvalue = 2.953
  Group = -> [Xe]
  conduct = 2
  density = 1
  expand = 3
  formula = G4_lXe
  name = G4_lXe
  specific = 4
FEATURE [App::DocumentObjectGroupPython] O_element107  label="O_element : 061"  # scripted group (container) (typed FeaturePython)
  n = 4
  ref = O_element
FEATURE [App::DocumentObjectGroupPython] Pb_element004  label="Pb_element : 002"  # scripted group (container) (typed FeaturePython)
  n = 1
  ref = Pb_element
FEATURE [App::DocumentObjectGroupPython] W_element005  label="W_element : 005"  # scripted group (container) (typed FeaturePython)
  n = 1
  ref = W_element
FEATURE [App::DocumentObjectGroupPython] G4_PbWO4  # scripted group (container) (typed FeaturePython)
  Dunit = g/cm3
  Dvalue = 8.28
  Group = -> [O_element107,Pb_element004,W_element005]
  conduct = 2
  density = 1
  expand = 3
  formula = G4_PbWO4
  name = G4_PbWO4
  specific = 4
FEATURE [App::DocumentObjectGroupPython] alactic  label="alactic : 1"  # scripted group (container) (typed FeaturePython)
  n = 1
  ref = alactic
FEATURE [App::DocumentObjectGroupPython] G4_Galactic  # scripted group (container) (typed FeaturePython)
  Dunit = g/cm3
  Dvalue = 0
  Group = -> [alactic]
  conduct = 2
  density = 1
  expand = 3
  formula = G4_Galactic
  name = G4_Galactic
  specific = 4
FEATURE [App::DocumentObjectGroupPython] RAPHITE_POROUS  label="RAPHITE_POROUS : 1"  # scripted group (container) (typed FeaturePython)
  n = 1
  ref = RAPHITE_POROUS
FEATURE [App::DocumentObjectGroupPython] G4_GRAPHITE_POROUS  # scripted group (container) (typed FeaturePython)
  Dunit = g/cm3
  Dvalue = 1.7
  Group = -> [RAPHITE_POROUS]
  conduct = 2
  density = 1
  expand = 3
  formula = G4_GRAPHITE_POROUS
  name = G4_GRAPHITE_POROUS
  specific = 4
FEATURE [App::DocumentObjectGroupPython] H_element115  label="H_element : 0.150"  # scripted group (container) (typed FeaturePython)
  n = 0.080538
FEATURE [App::DocumentObjectGroupPython] C_element125  label="C_element : 0.600"  # scripted group (container) (typed FeaturePython)
  n = 0.599848
FEATURE [App::DocumentObjectGroupPython] O_element108  label="O_element : 0.320"  # scripted group (container) (typed FeaturePython)
  n = 0.319614
FEATURE [App::DocumentObjectGroupPython] G4_LUCITE  # scripted group (container) (typed FeaturePython)
  Dunit = g/cm3
  Dvalue = 1.19
  Group = -> [H_element115,C_element125,O_element108]
  conduct = 2
  density = 1
  expand = 3
  formula = G4_LUCITE
  name = G4_LUCITE
  specific = 4
FEATURE [App::DocumentObjectGroupPython] Cu_element002  label="Cu_element : 62"  # scripted group (container) (typed FeaturePython)
  n = 62
  ref = Cu_element
FEATURE [App::DocumentObjectGroupPython] Zn_element002  label="Zn_element : 35"  # scripted group (container) (typed FeaturePython)
  n = 35
  ref = Zn_element
FEATURE [App::DocumentObjectGroupPython] Pb_element005  label="Pb_element : 3"  # scripted group (container) (typed FeaturePython)
  n = 3
  ref = Pb_element
FEATURE [App::DocumentObjectGroupPython] G4_BRASS  # scripted group (container) (typed FeaturePython)
  Dunit = g/cm3
  Dvalue = 8.52
  Group = -> [Cu_element002,Zn_element002,Pb_element005]
  conduct = 2
  density = 1
  expand = 3
  formula = G4_BRASS
  name = G4_BRASS
  specific = 4
FEATURE [App::DocumentObjectGroupPython] Cu_element003  label="Cu_element : 89"  # scripted group (container) (typed FeaturePython)
  n = 89
  ref = Cu_element
FEATURE [App::DocumentObjectGroupPython] Zn_element003  label="Zn_element : 9"  # scripted group (container) (typed FeaturePython)
  n = 9
  ref = Zn_element
FEATURE [App::DocumentObjectGroupPython] Pb_element006  label="Pb_element : 2"  # scripted group (container) (typed FeaturePython)
  n = 2
  ref = Pb_element
FEATURE [App::DocumentObjectGroupPython] G4_BRONZE  # scripted group (container) (typed FeaturePython)
  Dunit = g/cm3
  Dvalue = 8.82
  Group = -> [Cu_element003,Zn_element003,Pb_element006]
  conduct = 2
  density = 1
  expand = 3
  formula = G4_BRONZE
  name = G4_BRONZE
  specific = 4
FEATURE [App::DocumentObjectGroupPython] Fe_element008  label="Fe_element : 74"  # scripted group (container) (typed FeaturePython)
  n = 74
  ref = Fe_element
FEATURE [App::DocumentObjectGroupPython] Cr_element002  label="Cr_element : 18"  # scripted group (container) (typed FeaturePython)
  n = 18
  ref = Cr_element
FEATURE [App::DocumentObjectGroupPython] Ni_element002  label="Ni_element : 8"  # scripted group (container) (typed FeaturePython)
  n = 8
  ref = Ni_element
FEATURE [App::DocumentObjectGroupPython] G4_STAINLESS_STEEL  label="G4_STAINLESS-STEEL"  # scripted group (container) (typed FeaturePython)
  Dunit = g/cm3
  Dvalue = 8
  Group = -> [Fe_element008,Cr_element002,Ni_element002]
  conduct = 2
  density = 1
  expand = 3
  formula = G4_STAINLESS-STEEL
  name = G4_STAINLESS-STEEL
  specific = 4
FEATURE [App::DocumentObjectGroupPython] H_element116  label="H_element : 064"  # scripted group (container) (typed FeaturePython)
  n = 18
  ref = H_element
FEATURE [App::DocumentObjectGroupPython] C_element126  label="C_element : 071"  # scripted group (container) (typed FeaturePython)
  n = 12
  ref = C_element
FEATURE [App::DocumentObjectGroupPython] O_element109  label="O_element : 062"  # scripted group (container) (typed FeaturePython)
  n = 7
  ref = O_element
FEATURE [App::DocumentObjectGroupPython] G4_CR39  # scripted group (container) (typed FeaturePython)
  Dunit = g/cm3
  Dvalue = 1.32
  Group = -> [H_element116,C_element126,O_element109]
  conduct = 2
  density = 1
  expand = 3
  formula = G4_CR39
  name = G4_CR39
  specific = 4
FEATURE [App::DocumentObjectGroupPython] H_element117  label="H_element : 38"  # scripted group (container) (typed FeaturePython)
  n = 38
  ref = H_element
FEATURE [App::DocumentObjectGroupPython] C_element127  label="C_element : 072"  # scripted group (container) (typed FeaturePython)
  n = 18
  ref = C_element
FEATURE [App::DocumentObjectGroupPython] O_element110  label="O_element : 063"  # scripted group (container) (typed FeaturePython)
  n = 1
  ref = O_element
FEATURE [App::DocumentObjectGroupPython] G4_OCTADECANOL  # scripted group (container) (typed FeaturePython)
  Dunit = g/cm3
  Dvalue = 0.812
  Group = -> [H_element117,C_element127,O_element110]
  conduct = 2
  density = 1
  expand = 3
  formula = G4_OCTADECANOL
  name = G4_OCTADECANOL
  specific = 4
FEATURE [App::DocumentObjectGroupPython] HEP  # scripted group (container) (typed FeaturePython)
  Group = -> [G4_lH2,G4_lN2,G4_lO2,G4_lAr,G4_lBr,G4_lKr,G4_lXe,G4_PbWO4,G4_Galactic,G4_GRAPHITE_POROUS,G4_LUCITE,G4_BRASS,G4_BRONZE,G4_STAINLESS_STEEL,G4_CR39,G4_OCTADECANOL]
FEATURE [App::DocumentObjectGroupPython] C_element128  label="C_element : 073"  # scripted group (container) (typed FeaturePython)
  n = 14
  ref = C_element
FEATURE [App::DocumentObjectGroupPython] H_element118  label="H_element : 065"  # scripted group (container) (typed FeaturePython)
  n = 10
  ref = H_element
FEATURE [App::DocumentObjectGroupPython] O_element111  label="O_element : 064"  # scripted group (container) (typed FeaturePython)
  n = 2
  ref = O_element
FEATURE [App::DocumentObjectGroupPython] N_element050  label="N_element : 023"  # scripted group (container) (typed FeaturePython)
  n = 2
  ref = N_element
FEATURE [App::DocumentObjectGroupPython] G4_KEVLAR  # scripted group (container) (typed FeaturePython)
  Dunit = g/cm3
  Dvalue = 1.44
  Group = -> [C_element128,H_element118,O_element111,N_element050]
  conduct = 2
  density = 1
  expand = 3
  formula = G4_KEVLAR
  name = G4_KEVLAR
  specific = 4
FEATURE [App::DocumentObjectGroupPython] C_element129  label="C_element : 074"  # scripted group (container) (typed FeaturePython)
  n = 10
  ref = C_element
FEATURE [App::DocumentObjectGroupPython] H_element119  label="H_element : 066"  # scripted group (container) (typed FeaturePython)
  n = 8
  ref = H_element
FEATURE [App::DocumentObjectGroupPython] O_element112  label="O_element : 065"  # scripted group (container) (typed FeaturePython)
  n = 4
  ref = O_element
FEATURE [App::DocumentObjectGroupPython] G4_DACRON  # scripted group (container) (typed FeaturePython)
  Dunit = g/cm3
  Dvalue = 1.4
  Group = -> [C_element129,H_element119,O_element112]
  conduct = 2
  density = 1
  expand = 3
  formula = G4_DACRON
  name = G4_DACRON
  specific = 4
FEATURE [App::DocumentObjectGroupPython] C_element130  label="C_element : 075"  # scripted group (container) (typed FeaturePython)
  n = 4
  ref = C_element
FEATURE [App::DocumentObjectGroupPython] H_element120  label="H_element : 067"  # scripted group (container) (typed FeaturePython)
  n = 5
  ref = H_element
FEATURE [App::DocumentObjectGroupPython] Cl_element030  label="Cl_element : 016"  # scripted group (container) (typed FeaturePython)
  n = 1
  ref = Cl_element
FEATURE [App::DocumentObjectGroupPython] G4_NEOPRENE  # scripted group (container) (typed FeaturePython)
  Dunit = g/cm3
  Dvalue = 1.23
  Group = -> [C_element130,H_element120,Cl_element030]
  conduct = 2
  density = 1
  expand = 3
  formula = G4_NEOPRENE
  name = G4_NEOPRENE
  specific = 4
FEATURE [App::DocumentObjectGroupPython] Space  # scripted group (container) (typed FeaturePython)
  Group = -> [G4_KEVLAR,G4_DACRON,G4_NEOPRENE]
FEATURE [App::DocumentObjectGroupPython] H_element121  label="H_element : 068"  # scripted group (container) (typed FeaturePython)
  n = 5
  ref = H_element
FEATURE [App::DocumentObjectGroupPython] C_element131  label="C_element : 076"  # scripted group (container) (typed FeaturePython)
  n = 4
  ref = C_element
FEATURE [App::DocumentObjectGroupPython] N_element051  label="N_element : 3"  # scripted group (container) (typed FeaturePython)
  n = 3
  ref = N_element
FEATURE [App::DocumentObjectGroupPython] O_element113  label="O_element : 066"  # scripted group (container) (typed FeaturePython)
  n = 1
  ref = O_element
FEATURE [App::DocumentObjectGroupPython] G4_CYTOSINE  # scripted group (container) (typed FeaturePython)
  Dunit = g/cm3
  Dvalue = 1.55
  Group = -> [H_element121,C_element131,N_element051,O_element113]
  conduct = 2
  density = 1
  expand = 3
  formula = G4_CYTOSINE
  name = G4_CYTOSINE
  specific = 4
FEATURE [App::DocumentObjectGroupPython] H_element122  label="H_element : 069"  # scripted group (container) (typed FeaturePython)
  n = 6
  ref = H_element
FEATURE [App::DocumentObjectGroupPython] C_element132  label="C_element : 077"  # scripted group (container) (typed FeaturePython)
  n = 5
  ref = C_element
FEATURE [App::DocumentObjectGroupPython] N_element052  label="N_element : 024"  # scripted group (container) (typed FeaturePython)
  n = 2
  ref = N_element
FEATURE [App::DocumentObjectGroupPython] O_element114  label="O_element : 067"  # scripted group (container) (typed FeaturePython)
  n = 2
  ref = O_element
FEATURE [App::DocumentObjectGroupPython] G4_THYMINE  # scripted group (container) (typed FeaturePython)
  Dunit = g/cm3
  Dvalue = 1.23
  Group = -> [H_element122,C_element132,N_element052,O_element114]
  conduct = 2
  density = 1
  expand = 3
  formula = G4_THYMINE
  name = G4_THYMINE
  specific = 4
FEATURE [App::DocumentObjectGroupPython] H_element123  label="H_element : 070"  # scripted group (container) (typed FeaturePython)
  n = 4
  ref = H_element
FEATURE [App::DocumentObjectGroupPython] C_element133  label="C_element : 078"  # scripted group (container) (typed FeaturePython)
  n = 4
  ref = C_element
FEATURE [App::DocumentObjectGroupPython] N_element053  label="N_element : 025"  # scripted group (container) (typed FeaturePython)
  n = 2
  ref = N_element
FEATURE [App::DocumentObjectGroupPython] O_element115  label="O_element : 068"  # scripted group (container) (typed FeaturePython)
  n = 2
  ref = O_element
FEATURE [App::DocumentObjectGroupPython] G4_URACIL  # scripted group (container) (typed FeaturePython)
  Dunit = g/cm3
  Dvalue = 1.32
  Group = -> [H_element123,C_element133,N_element053,O_element115]
  conduct = 2
  density = 1
  expand = 3
  formula = G4_URACIL
  name = G4_URACIL
  specific = 4
FEATURE [App::DocumentObjectGroupPython] H_element124  label="H_element : 071"  # scripted group (container) (typed FeaturePython)
  n = 4
  ref = H_element
FEATURE [App::DocumentObjectGroupPython] C_element134  label="C_element : 079"  # scripted group (container) (typed FeaturePython)
  n = 5
  ref = C_element
FEATURE [App::DocumentObjectGroupPython] N_element054  label="N_element : 026"  # scripted group (container) (typed FeaturePython)
  n = 5
  ref = N_element
FEATURE [App::DocumentObjectGroupPython] G4_DNA_ADENINE  # scripted group (container) (typed FeaturePython)
  Dunit = g/cm3
  Dvalue = 1
  Group = -> [H_element124,C_element134,N_element054]
  conduct = 2
  density = 1
  expand = 3
  formula = G4_DNA_ADENINE
  name = G4_DNA_ADENINE
  specific = 4
FEATURE [App::DocumentObjectGroupPython] H_element125  label="H_element : 072"  # scripted group (container) (typed FeaturePython)
  n = 4
  ref = H_element
FEATURE [App::DocumentObjectGroupPython] C_element135  label="C_element : 080"  # scripted group (container) (typed FeaturePython)
  n = 5
  ref = C_element
FEATURE [App::DocumentObjectGroupPython] N_element055  label="N_element : 027"  # scripted group (container) (typed FeaturePython)
  n = 5
  ref = N_element
FEATURE [App::DocumentObjectGroupPython] O_element116  label="O_element : 069"  # scripted group (container) (typed FeaturePython)
  n = 1
  ref = O_element
FEATURE [App::DocumentObjectGroupPython] G4_DNA_GUANINE  # scripted group (container) (typed FeaturePython)
  Dunit = g/cm3
  Dvalue = 1
  Group = -> [H_element125,C_element135,N_element055,O_element116]
  conduct = 2
  density = 1
  expand = 3
  formula = G4_DNA_GUANINE
  name = G4_DNA_GUANINE
  specific = 4
FEATURE [App::DocumentObjectGroupPython] H_element126  label="H_element : 073"  # scripted group (container) (typed FeaturePython)
  n = 4
  ref = H_element
FEATURE [App::DocumentObjectGroupPython] C_element136  label="C_element : 081"  # scripted group (container) (typed FeaturePython)
  n = 4
  ref = C_element
FEATURE [App::DocumentObjectGroupPython] N_element056  label="N_element : 028"  # scripted group (container) (typed FeaturePython)
  n = 3
  ref = N_element
FEATURE [App::DocumentObjectGroupPython] O_element117  label="O_element : 070"  # scripted group (container) (typed FeaturePython)
  n = 1
  ref = O_element
FEATURE [App::DocumentObjectGroupPython] G4_DNA_CYTOSINE  # scripted group (container) (typed FeaturePython)
  Dunit = g/cm3
  Dvalue = 1
  Group = -> [H_element126,C_element136,N_element056,O_element117]
  conduct = 2
  density = 1
  expand = 3
  formula = G4_DNA_CYTOSINE
  name = G4_DNA_CYTOSINE
  specific = 4
FEATURE [App::DocumentObjectGroupPython] H_element127  label="H_element : 074"  # scripted group (container) (typed FeaturePython)
  n = 5
  ref = H_element
FEATURE [App::DocumentObjectGroupPython] C_element137  label="C_element : 082"  # scripted group (container) (typed FeaturePython)
  n = 5
  ref = C_element
FEATURE [App::DocumentObjectGroupPython] N_element057  label="N_element : 029"  # scripted group (container) (typed FeaturePython)
  n = 2
  ref = N_element
FEATURE [App::DocumentObjectGroupPython] O_element118  label="O_element : 071"  # scripted group (container) (typed FeaturePython)
  n = 2
  ref = O_element
FEATURE [App::DocumentObjectGroupPython] G4_DNA_THYMINE  # scripted group (container) (typed FeaturePython)
  Dunit = g/cm3
  Dvalue = 1
  Group = -> [H_element127,C_element137,N_element057,O_element118]
  conduct = 2
  density = 1
  expand = 3
  formula = G4_DNA_THYMINE
  name = G4_DNA_THYMINE
  specific = 4
FEATURE [App::DocumentObjectGroupPython] H_element128  label="H_element : 075"  # scripted group (container) (typed FeaturePython)
  n = 3
  ref = H_element
FEATURE [App::DocumentObjectGroupPython] C_element138  label="C_element : 083"  # scripted group (container) (typed FeaturePython)
  n = 4
  ref = C_element
FEATURE [App::DocumentObjectGroupPython] N_element058  label="N_element : 030"  # scripted group (container) (typed FeaturePython)
  n = 2
  ref = N_element
FEATURE [App::DocumentObjectGroupPython] O_element119  label="O_element : 072"  # scripted group (container) (typed FeaturePython)
  n = 2
  ref = O_element
FEATURE [App::DocumentObjectGroupPython] G4_DNA_URACIL  # scripted group (container) (typed FeaturePython)
  Dunit = g/cm3
  Dvalue = 1
  Group = -> [H_element128,C_element138,N_element058,O_element119]
  conduct = 2
  density = 1
  expand = 3
  formula = G4_DNA_URACIL
  name = G4_DNA_URACIL
  specific = 4
FEATURE [App::DocumentObjectGroupPython] H_element129  label="H_element : 076"  # scripted group (container) (typed FeaturePython)
  n = 10
  ref = H_element
FEATURE [App::DocumentObjectGroupPython] C_element139  label="C_element : 084"  # scripted group (container) (typed FeaturePython)
  n = 10
  ref = C_element
FEATURE [App::DocumentObjectGroupPython] N_element059  label="N_element : 031"  # scripted group (container) (typed FeaturePython)
  n = 5
  ref = N_element
FEATURE [App::DocumentObjectGroupPython] O_element120  label="O_element : 073"  # scripted group (container) (typed FeaturePython)
  n = 4
  ref = O_element
FEATURE [App::DocumentObjectGroupPython] G4_DNA_ADENOSINE  # scripted group (container) (typed FeaturePython)
  Dunit = g/cm3
  Dvalue = 1
  Group = -> [H_element129,C_element139,N_element059,O_element120]
  conduct = 2
  density = 1
  expand = 3
  formula = G4_DNA_ADENOSINE
  name = G4_DNA_ADENOSINE
  specific = 4
FEATURE [App::DocumentObjectGroupPython] H_element130  label="H_element : 077"  # scripted group (container) (typed FeaturePython)
  n = 10
  ref = H_element
FEATURE [App::DocumentObjectGroupPython] C_element140  label="C_element : 085"  # scripted group (container) (typed FeaturePython)
  n = 10
  ref = C_element
FEATURE [App::DocumentObjectGroupPython] N_element060  label="N_element : 032"  # scripted group (container) (typed FeaturePython)
  n = 5
  ref = N_element
FEATURE [App::DocumentObjectGroupPython] O_element121  label="O_element : 074"  # scripted group (container) (typed FeaturePython)
  n = 5
  ref = O_element
FEATURE [App::DocumentObjectGroupPython] G4_DNA_GUANOSINE  # scripted group (container) (typed FeaturePython)
  Dunit = g/cm3
  Dvalue = 1
  Group = -> [H_element130,C_element140,N_element060,O_element121]
  conduct = 2
  density = 1
  expand = 3
  formula = G4_DNA_GUANOSINE
  name = G4_DNA_GUANOSINE
  specific = 4
FEATURE [App::DocumentObjectGroupPython] H_element131  label="H_element : 078"  # scripted group (container) (typed FeaturePython)
  n = 10
  ref = H_element
FEATURE [App::DocumentObjectGroupPython] C_element141  label="C_element : 086"  # scripted group (container) (typed FeaturePython)
  n = 9
  ref = C_element
FEATURE [App::DocumentObjectGroupPython] N_element061  label="N_element : 033"  # scripted group (container) (typed FeaturePython)
  n = 3
  ref = N_element
FEATURE [App::DocumentObjectGroupPython] O_element122  label="O_element : 075"  # scripted group (container) (typed FeaturePython)
  n = 5
  ref = O_element
FEATURE [App::DocumentObjectGroupPython] G4_DNA_CYTIDINE  # scripted group (container) (typed FeaturePython)
  Dunit = g/cm3
  Dvalue = 1
  Group = -> [H_element131,C_element141,N_element061,O_element122]
  conduct = 2
  density = 1
  expand = 3
  formula = G4_DNA_CYTIDINE
  name = G4_DNA_CYTIDINE
  specific = 4
FEATURE [App::DocumentObjectGroupPython] H_element132  label="H_element : 079"  # scripted group (container) (typed FeaturePython)
  n = 9
  ref = H_element
FEATURE [App::DocumentObjectGroupPython] C_element142  label="C_element : 087"  # scripted group (container) (typed FeaturePython)
  n = 9
  ref = C_element
FEATURE [App::DocumentObjectGroupPython] N_element062  label="N_element : 034"  # scripted group (container) (typed FeaturePython)
  n = 2
  ref = N_element
FEATURE [App::DocumentObjectGroupPython] O_element123  label="O_element : 076"  # scripted group (container) (typed FeaturePython)
  n = 6
  ref = O_element
FEATURE [App::DocumentObjectGroupPython] G4_DNA_URIDINE  # scripted group (container) (typed FeaturePython)
  Dunit = g/cm3
  Dvalue = 1
  Group = -> [H_element132,C_element142,N_element062,O_element123]
  conduct = 2
  density = 1
  expand = 3
  formula = G4_DNA_URIDINE
  name = G4_DNA_URIDINE
  specific = 4
FEATURE [App::DocumentObjectGroupPython] H_element133  label="H_element : 080"  # scripted group (container) (typed FeaturePython)
  n = 11
  ref = H_element
FEATURE [App::DocumentObjectGroupPython] C_element143  label="C_element : 088"  # scripted group (container) (typed FeaturePython)
  n = 10
  ref = C_element
FEATURE [App::DocumentObjectGroupPython] N_element063  label="N_element : 035"  # scripted group (container) (typed FeaturePython)
  n = 2
  ref = N_element
FEATURE [App::DocumentObjectGroupPython] O_element124  label="O_element : 077"  # scripted group (container) (typed FeaturePython)
  n = 6
  ref = O_element
FEATURE [App::DocumentObjectGroupPython] G4_DNA_METHYLURIDINE  # scripted group (container) (typed FeaturePython)
  Dunit = g/cm3
  Dvalue = 1
  Group = -> [H_element133,C_element143,N_element063,O_element124]
  conduct = 2
  density = 1
  expand = 3
  formula = G4_DNA_METHYLURIDINE
  name = G4_DNA_METHYLURIDINE
  specific = 4
FEATURE [App::DocumentObjectGroupPython] P_element014  label="P_element : 003"  # scripted group (container) (typed FeaturePython)
  n = 1
  ref = P_element
FEATURE [App::DocumentObjectGroupPython] O_element125  label="O_element : 078"  # scripted group (container) (typed FeaturePython)
  n = 3
  ref = O_element
FEATURE [App::DocumentObjectGroupPython] G4_DNA_MONOPHOSPHATE  # scripted group (container) (typed FeaturePython)
  Dunit = g/cm3
  Dvalue = 1
  Group = -> [P_element014,O_element125]
  conduct = 2
  density = 1
  expand = 3
  formula = G4_DNA_MONOPHOSPHATE
  name = G4_DNA_MONOPHOSPHATE
  specific = 4
FEATURE [App::DocumentObjectGroupPython] H_element134  label="H_element : 081"  # scripted group (container) (typed FeaturePython)
  n = 10
  ref = H_element
FEATURE [App::DocumentObjectGroupPython] C_element144  label="C_element : 089"  # scripted group (container) (typed FeaturePython)
  n = 10
  ref = C_element
FEATURE [App::DocumentObjectGroupPython] N_element064  label="N_element : 036"  # scripted group (container) (typed FeaturePython)
  n = 5
  ref = N_element
FEATURE [App::DocumentObjectGroupPython] O_element126  label="O_element : 079"  # scripted group (container) (typed FeaturePython)
  n = 7
  ref = O_element
FEATURE [App::DocumentObjectGroupPython] P_element015  label="P_element : 004"  # scripted group (container) (typed FeaturePython)
  n = 1
  ref = P_element
FEATURE [App::DocumentObjectGroupPython] G4_DNA_A  # scripted group (container) (typed FeaturePython)
  Dunit = g/cm3
  Dvalue = 1
  Group = -> [H_element134,C_element144,N_element064,O_element126,P_element015]
  conduct = 2
  density = 1
  expand = 3
  formula = G4_DNA_A
  name = G4_DNA_A
  specific = 4
FEATURE [App::DocumentObjectGroupPython] H_element135  label="H_element : 082"  # scripted group (container) (typed FeaturePython)
  n = 10
  ref = H_element
FEATURE [App::DocumentObjectGroupPython] C_element145  label="C_element : 090"  # scripted group (container) (typed FeaturePython)
  n = 10
  ref = C_element
FEATURE [App::DocumentObjectGroupPython] N_element065  label="N_element : 037"  # scripted group (container) (typed FeaturePython)
  n = 5
  ref = N_element
FEATURE [App::DocumentObjectGroupPython] O_element127  label="O_element : 8"  # scripted group (container) (typed FeaturePython)
  n = 8
  ref = O_element
FEATURE [App::DocumentObjectGroupPython] P_element016  label="P_element : 005"  # scripted group (container) (typed FeaturePython)
  n = 1
  ref = P_element
FEATURE [App::DocumentObjectGroupPython] G4_DNA_G  # scripted group (container) (typed FeaturePython)
  Dunit = g/cm3
  Dvalue = 1
  Group = -> [H_element135,C_element145,N_element065,O_element127,P_element016]
  conduct = 2
  density = 1
  expand = 3
  formula = G4_DNA_G
  name = G4_DNA_G
  specific = 4
FEATURE [App::DocumentObjectGroupPython] H_element136  label="H_element : 083"  # scripted group (container) (typed FeaturePython)
  n = 10
  ref = H_element
FEATURE [App::DocumentObjectGroupPython] C_element146  label="C_element : 091"  # scripted group (container) (typed FeaturePython)
  n = 9
  ref = C_element
FEATURE [App::DocumentObjectGroupPython] N_element066  label="N_element : 038"  # scripted group (container) (typed FeaturePython)
  n = 3
  ref = N_element
FEATURE [App::DocumentObjectGroupPython] O_element128  label="O_element : 080"  # scripted group (container) (typed FeaturePython)
  n = 8
  ref = O_element
FEATURE [App::DocumentObjectGroupPython] P_element017  label="P_element : 006"  # scripted group (container) (typed FeaturePython)
  n = 1
  ref = P_element
FEATURE [App::DocumentObjectGroupPython] G4_DNA_C  # scripted group (container) (typed FeaturePython)
  Dunit = g/cm3
  Dvalue = 1
  Group = -> [H_element136,C_element146,N_element066,O_element128,P_element017]
  conduct = 2
  density = 1
  expand = 3
  formula = G4_DNA_C
  name = G4_DNA_C
  specific = 4
FEATURE [App::DocumentObjectGroupPython] H_element137  label="H_element : 084"  # scripted group (container) (typed FeaturePython)
  n = 9
  ref = H_element
FEATURE [App::DocumentObjectGroupPython] C_element147  label="C_element : 092"  # scripted group (container) (typed FeaturePython)
  n = 9
  ref = C_element
FEATURE [App::DocumentObjectGroupPython] N_element067  label="N_element : 039"  # scripted group (container) (typed FeaturePython)
  n = 2
  ref = N_element
FEATURE [App::DocumentObjectGroupPython] O_element129  label="O_element : 9"  # scripted group (container) (typed FeaturePython)
  n = 9
  ref = O_element
FEATURE [App::DocumentObjectGroupPython] P_element018  label="P_element : 007"  # scripted group (container) (typed FeaturePython)
  n = 1
  ref = P_element
FEATURE [App::DocumentObjectGroupPython] G4_DNA_U  # scripted group (container) (typed FeaturePython)
  Dunit = g/cm3
  Dvalue = 1
  Group = -> [H_element137,C_element147,N_element067,O_element129,P_element018]
  conduct = 2
  density = 1
  expand = 3
  formula = G4_DNA_U
  name = G4_DNA_U
  specific = 4
FEATURE [App::DocumentObjectGroupPython] H_element138  label="H_element : 085"  # scripted group (container) (typed FeaturePython)
  n = 11
  ref = H_element
FEATURE [App::DocumentObjectGroupPython] C_element148  label="C_element : 093"  # scripted group (container) (typed FeaturePython)
  n = 10
  ref = C_element
FEATURE [App::DocumentObjectGroupPython] N_element068  label="N_element : 040"  # scripted group (container) (typed FeaturePython)
  n = 2
  ref = N_element
FEATURE [App::DocumentObjectGroupPython] O_element130  label="O_element : 081"  # scripted group (container) (typed FeaturePython)
  n = 9
  ref = O_element
FEATURE [App::DocumentObjectGroupPython] P_element019  label="P_element : 008"  # scripted group (container) (typed FeaturePython)
  n = 1
  ref = P_element
FEATURE [App::DocumentObjectGroupPython] G4_DNA_MU  # scripted group (container) (typed FeaturePython)
  Dunit = g/cm3
  Dvalue = 1
  Group = -> [H_element138,C_element148,N_element068,O_element130,P_element019]
  conduct = 2
  density = 1
  expand = 3
  formula = G4_DNA_MU
  name = G4_DNA_MU
  specific = 4
FEATURE [App::DocumentObjectGroupPython] BioChemical  # scripted group (container) (typed FeaturePython)
  Group = -> [G4_CYTOSINE,G4_THYMINE,G4_URACIL,G4_DNA_ADENINE,G4_DNA_GUANINE,G4_DNA_CYTOSINE,G4_DNA_THYMINE,G4_DNA_URACIL,G4_DNA_ADENOSINE,G4_DNA_GUANOSINE,G4_DNA_CYTIDINE,G4_DNA_URIDINE,G4_DNA_METHYLURIDINE,G4_DNA_MONOPHOSPHATE,G4_DNA_A,G4_DNA_G,G4_DNA_C,G4_DNA_U,G4_DNA_MU]
FEATURE [App::DocumentObjectGroupPython] G4Materials  # scripted group (container) (typed FeaturePython)
  Group = -> [NIST,Element,HEP,Space,BioChemical]
  version = 1
FEATURE [App::DocumentObjectGroupPython] Geant4  # scripted group (container) (typed FeaturePython)
  Group = -> [G4Isotopes,G4Elements,G4Materials]
FEATURE [App::DocumentObjectGroupPython] Materials  # scripted group (container) (typed FeaturePython)
  Group = -> [Geant4]
FEATURE [Part::FeaturePython] GDMLBox_WorldBox  # WARN: FeaturePython — macro-defined, semantics opaque (R4)
  lunit = 3
  material = 288
  x = 500
  y = 500
  z = 1200
FEATURE [Sketcher::SketchObject] Sketch001
  FullyConstrained = false
  MapMode = 5
  Placement = pos=(0,0,0) rot=(0.57735,0.57735,0.57735;2.0944rad)
  Support = -> [YZ_Plane001]
  sketch-geometry (36):
    g0: LineSegment StartX=345.196 StartY=1207.39 StartZ=0 EndX=345.196 EndY=4779.1 EndZ=0
    g1: LineSegment StartX=910.487 StartY=4896.42 StartZ=0 EndX=910.487 EndY=5006.42 EndZ=0
    g2: LineSegment StartX=435.196 StartY=4869.1 StartZ=0 EndX=445.196 EndY=4869.1 EndZ=0
    g3: LineSegment StartX=445.196 StartY=4869.1 StartZ=0 EndX=445.196 EndY=4896.42 EndZ=0
    g4: LineSegment StartX=445.196 StartY=4896.42 StartZ=0 EndX=910.487 EndY=4896.42 EndZ=0
    g5: LineSegment StartX=318.538 StartY=5006.42 StartZ=0 EndX=910.487 EndY=5006.42 EndZ=0
    g6: LineSegment StartX=175.531 StartY=1234.96 StartZ=0 EndX=318.538 EndY=1234.96 EndZ=0
    g7: LineSegment StartX=318.538 StartY=5006.42 StartZ=0 EndX=318.538 EndY=1234.96 EndZ=0
    g8: LineSegment StartX=0 StartY=39.215 StartZ=0 EndX=0 EndY=0 EndZ=0
    g9-g16: Circle x8 (B-spline internal-alignment scaffolding for g17; pole/knot coordinates omitted)
    g17: BSplineCurve PolesCount=8 KnotsCount=6 Degree=3 IsPeriodic=0
    g18-g23: GeomPoint x6 (B-spline internal-alignment scaffolding for g17; pole/knot coordinates omitted)
    g24: LineSegment StartX=175.531 StartY=1234.96 StartZ=0 EndX=175.531 EndY=838.896 EndZ=0
    g25-g29: Circle x5 (B-spline internal-alignment scaffolding for g30; pole/knot coordinates omitted)
    g30: BSplineCurve PolesCount=5 KnotsCount=3 Degree=3 IsPeriodic=0
    g31: GeomPoint X=175.531 Y=838.896 Z=0
    g32: GeomPoint X=165.058 Y=242.363 Z=0
    g33: GeomPoint X=0 Y=39.215 Z=0
    g34: ArcOfCircle CenterX=435.196 CenterY=4779.1 CenterZ=0 NormalX=0 NormalY=0 NormalZ=1 AngleXU=0 Radius=90 StartAngle=1.5708 EndAngle=3.14159
    g35: GeomPoint X=345.196 Y=4869.1 Z=0
  constraints (38):
    c: Vertical(g1)
    c: Horizontal(g2)
    c: Coincident(g2,g3)
    c: Vertical(g3)
    c: Coincident(g3,g4)
    c: Coincident(g4,g1)
    c: Horizontal(g4)
    c: Coincident(g5,g1)
    c: Horizontal(g5)
    c: Horizontal(g6)
    c: Coincident(g7,g5)
    c: Coincident(g7,g6)
    c: Vertical(g7)
    c: DistanceX(g35,g2) = 100
    c: Vertical(g8)
    c: Vertical(g0)
    c: Coincident(g17,g0)
    c: Weight(g9) = 1
    c: Equal(g9, g10-g16) x7
    c: Coincident(g17,g8)
    c: InternalAlignment(g9-g16 -> g17) x8
    c: InternalAlignment(g18-g23 -> g17) x6
    c: Coincident(g24,g6)
    c: Vertical(g24)
    c: Coincident(g30,g24)
    c: Weight(g25) = 1
    c: Equal(g25, g26-g29) x4
    c: Coincident(g30,g8)
    c: InternalAlignment(g25-g29 -> g30) x5
    c: InternalAlignment(g31,g30)
    c: InternalAlignment(g32,g30)
    c: InternalAlignment(g33,g30)
    c: Coincident(g8,g-1)
    c: PointOnObject(g35,g2)
    c: PointOnObject(g35,g0)
    c: Tangent(g2,g34) = 1.5708
    c: Tangent(g0,g34) = 1.5708
    c: Radius(g34) = 90
FEATURE [Part::Revolution] Revolve
  Angle = 360
  Axis = (0,0,1)
  Base = (0,0,0)
  FaceMakerClass = Part::FaceMakerBullseye
  Solid = true
  Source = -> Sketch001
  Symmetric = false
  material = 176
FEATURE [Part::Cylinder] Cylinder
  Angle = 360
  AttacherType = Attacher::AttachEngine3D
  FirstAngle = 0
  Height = 200
  Placement = pos=(474,0,4850) rot=(0,0,1;0rad)
  Radius = 60
  SecondAngle = 0
FEATURE [Part::FeaturePython] Array  # Draft array (typed FeaturePython)
  Angle = 360
  ArrayType = 1
  Axis = (0,0,1)
  Base = -> Cylinder
  Center = (0,0,0)
  Count = 6
  Fuse = false
  IntervalAxis = (0,0,0)
  IntervalX = (50,0,0)
  IntervalY = (0,50,0)
  IntervalZ = (0,0,50)
  NumberCircles = 3
  NumberPolar = 6
  NumberX = 2
  NumberY = 2
  NumberZ = 1
  RadialDistance = 50
  Symmetry = 1
  TangentialDistance = 25
FEATURE [Part::Cut] Cut
  Base = -> Revolve
  Tool = -> Array
FEATURE [App::Part] Bool_Cut
  Group = -> [Revolve,Cylinder,Sketch001,Array,Cut]
  Origin = -> Origin004
FEATURE [App::Part] worldVOL
  Group = -> [GDMLBox_WorldBox,Bool_Cut]
  Origin = -> Origin
